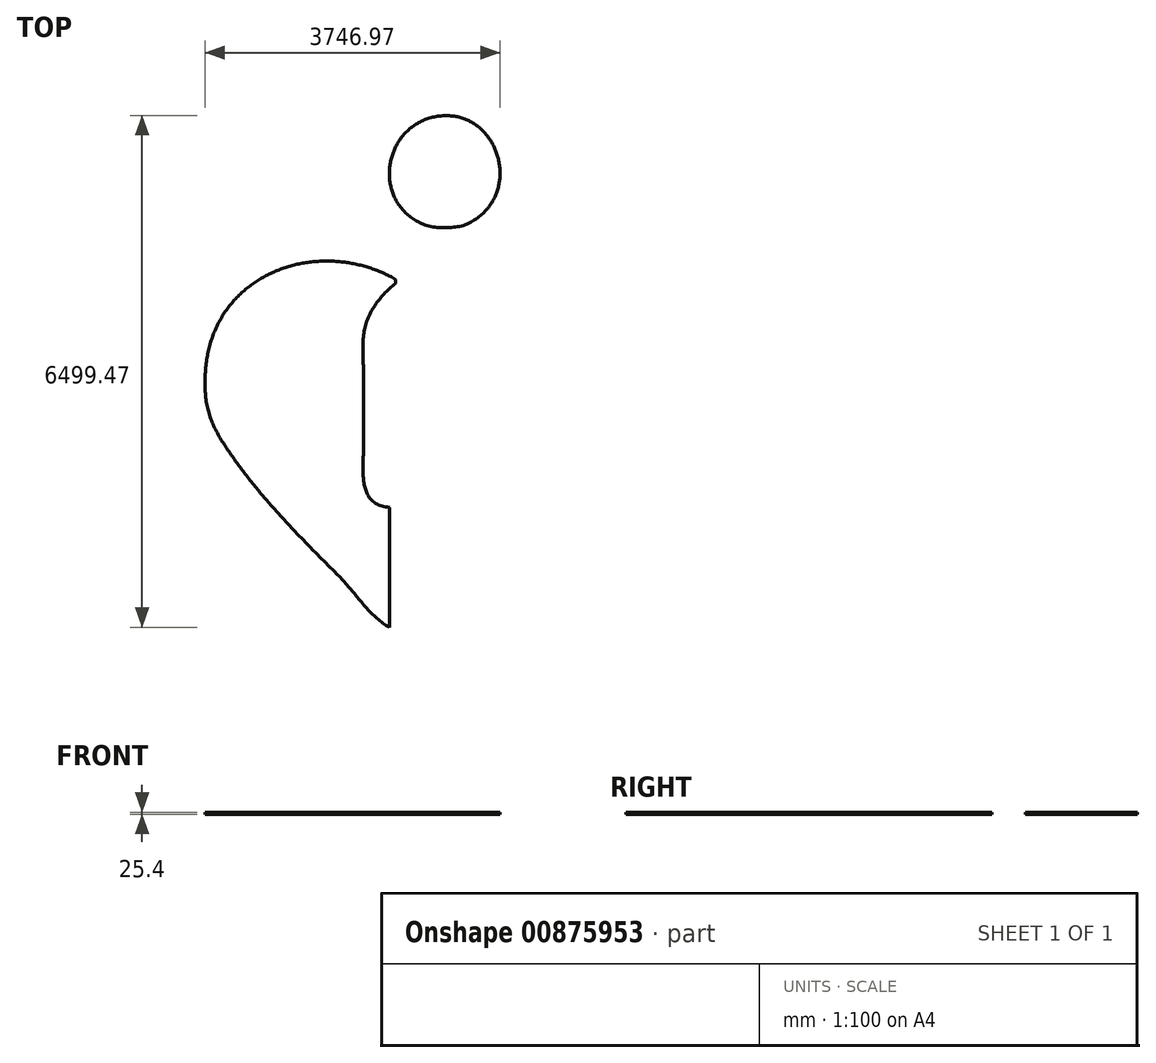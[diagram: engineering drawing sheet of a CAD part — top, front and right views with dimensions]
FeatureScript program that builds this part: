
annotation { "Feature Type Name" : "Feature", "Feature Type Description" : "" }
export const myFeature = defineFeature(function(context is Context, id is Id, definition is map)
    precondition{}
    {
        {
            var Q0;
            Q0=qCreatedBy(makeId("Top.planeOp"),FACE);
            var sketch = newSketch(context, id + "F0", { "sketchPlane" : qUnion([Q0])});
            skLineSegment(sketch, "E0", {"start": v(-84.52, 3774.14) * mm, "end": v(-106.58, 3770.53) * mm});
            skLineSegment(sketch, "E1", {"start": v(-106.58, 3770.53) * mm, "end": v(-128.27, 3766.32) * mm});
            skLineSegment(sketch, "E2", {"start": v(-128.27, 3766.32) * mm, "end": v(-149.6, 3761.53) * mm});
            skLineSegment(sketch, "E3", {"start": v(-149.6, 3761.53) * mm, "end": v(-170.55, 3756.17) * mm});
            skLineSegment(sketch, "E4", {"start": v(-170.55, 3756.17) * mm, "end": v(-191.14, 3750.25) * mm});
            skLineSegment(sketch, "E5", {"start": v(-191.14, 3750.25) * mm, "end": v(-211.36, 3743.78) * mm});
            skLineSegment(sketch, "E6", {"start": v(-211.36, 3743.78) * mm, "end": v(-231.2, 3736.77) * mm});
            skLineSegment(sketch, "E7", {"start": v(-231.2, 3736.77) * mm, "end": v(-250.65, 3729.24) * mm});
            skLineSegment(sketch, "E8", {"start": v(-250.65, 3729.24) * mm, "end": v(-269.73, 3721.19) * mm});
            skLineSegment(sketch, "E9", {"start": v(-269.73, 3721.19) * mm, "end": v(-288.43, 3712.64) * mm});
            skLineSegment(sketch, "E10", {"start": v(-288.43, 3712.64) * mm, "end": v(-306.74, 3703.6) * mm});
            skLineSegment(sketch, "E11", {"start": v(-306.74, 3703.6) * mm, "end": v(-324.67, 3694.08) * mm});
            skLineSegment(sketch, "E12", {"start": v(-324.67, 3694.08) * mm, "end": v(-342.2, 3684.1) * mm});
            skLineSegment(sketch, "E13", {"start": v(-342.2, 3684.1) * mm, "end": v(-359.34, 3673.65) * mm});
            skLineSegment(sketch, "E14", {"start": v(-359.34, 3673.65) * mm, "end": v(-376.09, 3662.76) * mm});
            skLineSegment(sketch, "E15", {"start": v(-376.09, 3662.76) * mm, "end": v(-392.44, 3651.45) * mm});
            skLineSegment(sketch, "E16", {"start": v(-392.44, 3651.45) * mm, "end": v(-408.39, 3639.7) * mm});
            skLineSegment(sketch, "E17", {"start": v(-408.39, 3639.7) * mm, "end": v(-423.94, 3627.56) * mm});
            skLineSegment(sketch, "E18", {"start": v(-423.94, 3627.56) * mm, "end": v(-439.08, 3615.01) * mm});
            skLineSegment(sketch, "E19", {"start": v(-439.08, 3615.01) * mm, "end": v(-453.82, 3602.09) * mm});
            skLineSegment(sketch, "E20", {"start": v(-453.82, 3602.09) * mm, "end": v(-468.14, 3588.78) * mm});
            skLineSegment(sketch, "E21", {"start": v(-468.14, 3588.78) * mm, "end": v(-482.06, 3575.11) * mm});
            skLineSegment(sketch, "E22", {"start": v(-482.06, 3575.11) * mm, "end": v(-495.57, 3561.1) * mm});
            skLineSegment(sketch, "E23", {"start": v(-495.57, 3561.1) * mm, "end": v(-508.65, 3546.74) * mm});
            skLineSegment(sketch, "E24", {"start": v(-508.65, 3546.74) * mm, "end": v(-521.32, 3532.06) * mm});
            skLineSegment(sketch, "E25", {"start": v(-521.32, 3532.06) * mm, "end": v(-533.57, 3517.06) * mm});
            skLineSegment(sketch, "E26", {"start": v(-533.57, 3517.06) * mm, "end": v(-545.4, 3501.75) * mm});
            skLineSegment(sketch, "E27", {"start": v(-545.4, 3501.75) * mm, "end": v(-556.8, 3486.16) * mm});
            skLineSegment(sketch, "E28", {"start": v(-556.8, 3486.16) * mm, "end": v(-567.76, 3470.28) * mm});
            skLineSegment(sketch, "E29", {"start": v(-567.76, 3470.28) * mm, "end": v(-578.3, 3454.14) * mm});
            skLineSegment(sketch, "E30", {"start": v(-578.3, 3454.14) * mm, "end": v(-588.41, 3437.73) * mm});
            skLineSegment(sketch, "E31", {"start": v(-588.41, 3437.73) * mm, "end": v(-598.09, 3421.08) * mm});
            skLineSegment(sketch, "E32", {"start": v(-598.09, 3421.08) * mm, "end": v(-607.32, 3404.2) * mm});
            skLineSegment(sketch, "E33", {"start": v(-607.32, 3404.2) * mm, "end": v(-616.12, 3387.1) * mm});
            skLineSegment(sketch, "E34", {"start": v(-616.12, 3387.1) * mm, "end": v(-624.47, 3369.78) * mm});
            skLineSegment(sketch, "E35", {"start": v(-624.47, 3369.78) * mm, "end": v(-632.38, 3352.26) * mm});
            skLineSegment(sketch, "E36", {"start": v(-632.38, 3352.26) * mm, "end": v(-639.84, 3334.56) * mm});
            skLineSegment(sketch, "E37", {"start": v(-639.84, 3334.56) * mm, "end": v(-646.85, 3316.68) * mm});
            skLineSegment(sketch, "E38", {"start": v(-646.85, 3316.68) * mm, "end": v(-653.41, 3298.64) * mm});
            skLineSegment(sketch, "E39", {"start": v(-653.41, 3298.64) * mm, "end": v(-659.52, 3280.45) * mm});
            skLineSegment(sketch, "E40", {"start": v(-659.52, 3280.45) * mm, "end": v(-665.17, 3262.1) * mm});
            skLineSegment(sketch, "E41", {"start": v(-665.17, 3262.1) * mm, "end": v(-670.36, 3243.65) * mm});
            skLineSegment(sketch, "E42", {"start": v(-670.36, 3243.65) * mm, "end": v(-675.09, 3225.06) * mm});
            skLineSegment(sketch, "E43", {"start": v(-675.09, 3225.06) * mm, "end": v(-679.36, 3206.37) * mm});
            skLineSegment(sketch, "E44", {"start": v(-679.36, 3206.37) * mm, "end": v(-683.16, 3187.6) * mm});
            skLineSegment(sketch, "E45", {"start": v(-683.16, 3187.6) * mm, "end": v(-686.49, 3168.73) * mm});
            skLineSegment(sketch, "E46", {"start": v(-686.49, 3168.73) * mm, "end": v(-689.35, 3149.8) * mm});
            skLineSegment(sketch, "E47", {"start": v(-689.35, 3149.8) * mm, "end": v(-691.74, 3130.8) * mm});
            skLineSegment(sketch, "E48", {"start": v(-691.74, 3130.8) * mm, "end": v(-693.65, 3111.75) * mm});
            skLineSegment(sketch, "E49", {"start": v(-693.65, 3111.75) * mm, "end": v(-695.08, 3092.68) * mm});
            skLineSegment(sketch, "E50", {"start": v(-695.08, 3092.68) * mm, "end": v(-696.04, 3073.57) * mm});
            skLineSegment(sketch, "E51", {"start": v(-696.04, 3073.57) * mm, "end": v(-696.5, 3054.46) * mm});
            skLineSegment(sketch, "E52", {"start": v(-696.5, 3054.46) * mm, "end": v(-696.5, 3035.34) * mm});
            skLineSegment(sketch, "E53", {"start": v(-696.5, 3035.34) * mm, "end": v(-696, 3016.23) * mm});
            skLineSegment(sketch, "E54", {"start": v(-696, 3016.23) * mm, "end": v(-695, 2997.15) * mm});
            skLineSegment(sketch, "E55", {"start": v(-695, 2997.15) * mm, "end": v(-693.52, 2978.1) * mm});
            skLineSegment(sketch, "E56", {"start": v(-693.52, 2978.1) * mm, "end": v(-691.54, 2959.1) * mm});
            skLineSegment(sketch, "E57", {"start": v(-691.54, 2959.1) * mm, "end": v(-689.07, 2940.15) * mm});
            skLineSegment(sketch, "E58", {"start": v(-689.07, 2940.15) * mm, "end": v(-686.1, 2921.28) * mm});
            skLineSegment(sketch, "E59", {"start": v(-686.1, 2921.28) * mm, "end": v(-682.62, 2902.48) * mm});
            skLineSegment(sketch, "E60", {"start": v(-682.62, 2902.48) * mm, "end": v(-678.64, 2883.78) * mm});
            skLineSegment(sketch, "E61", {"start": v(-678.64, 2883.78) * mm, "end": v(-674.15, 2865.18) * mm});
            skLineSegment(sketch, "E62", {"start": v(-674.15, 2865.18) * mm, "end": v(-669.16, 2846.7) * mm});
            skLineSegment(sketch, "E63", {"start": v(-669.16, 2846.7) * mm, "end": v(-663.65, 2828.34) * mm});
            skLineSegment(sketch, "E64", {"start": v(-663.65, 2828.34) * mm, "end": v(-657.63, 2810.12) * mm});
            skLineSegment(sketch, "E65", {"start": v(-657.63, 2810.12) * mm, "end": v(-651.1, 2792.05) * mm});
            skLineSegment(sketch, "E66", {"start": v(-651.1, 2792.05) * mm, "end": v(-644.04, 2774.14) * mm});
            skLineSegment(sketch, "E67", {"start": v(-644.04, 2774.14) * mm, "end": v(-636.47, 2756.41) * mm});
            skLineSegment(sketch, "E68", {"start": v(-636.47, 2756.41) * mm, "end": v(-628.38, 2738.87) * mm});
            skLineSegment(sketch, "E69", {"start": v(-628.38, 2738.87) * mm, "end": v(-619.75, 2721.52) * mm});
            skLineSegment(sketch, "E70", {"start": v(-619.75, 2721.52) * mm, "end": v(-610.6, 2704.38) * mm});
            skLineSegment(sketch, "E71", {"start": v(-610.6, 2704.38) * mm, "end": v(-600.92, 2687.46) * mm});
            skLineSegment(sketch, "E72", {"start": v(-600.92, 2687.46) * mm, "end": v(-590.7, 2670.77) * mm});
            skLineSegment(sketch, "E73", {"start": v(-590.7, 2670.77) * mm, "end": v(-579.96, 2654.33) * mm});
            skLineSegment(sketch, "E74", {"start": v(-579.96, 2654.33) * mm, "end": v(-568.68, 2638.14) * mm});
            skLineSegment(sketch, "E75", {"start": v(-568.68, 2638.14) * mm, "end": v(-556.85, 2622.22) * mm});
            skLineSegment(sketch, "E76", {"start": v(-556.85, 2622.22) * mm, "end": v(-544.48, 2606.58) * mm});
            skLineSegment(sketch, "E77", {"start": v(-544.48, 2606.58) * mm, "end": v(-531.57, 2591.23) * mm});
            skLineSegment(sketch, "E78", {"start": v(-531.57, 2591.23) * mm, "end": v(-518.11, 2576.18) * mm});
            skLineSegment(sketch, "E79", {"start": v(-518.11, 2576.18) * mm, "end": v(-504.1, 2561.45) * mm});
            skLineSegment(sketch, "E80", {"start": v(-504.1, 2561.45) * mm, "end": v(-489.55, 2547.04) * mm});
            skLineSegment(sketch, "E81", {"start": v(-489.55, 2547.04) * mm, "end": v(-474.44, 2532.97) * mm});
            skLineSegment(sketch, "E82", {"start": v(-474.44, 2532.97) * mm, "end": v(-458.77, 2519.24) * mm});
            skLineSegment(sketch, "E83", {"start": v(-458.77, 2519.24) * mm, "end": v(-442.54, 2505.88) * mm});
            skLineSegment(sketch, "E84", {"start": v(-442.54, 2505.88) * mm, "end": v(-425.75, 2492.89) * mm});
            skLineSegment(sketch, "E85", {"start": v(-425.75, 2492.89) * mm, "end": v(-408.4, 2480.28) * mm});
            skLineSegment(sketch, "E86", {"start": v(-408.4, 2480.28) * mm, "end": v(-390.48, 2468.07) * mm});
            skLineSegment(sketch, "E87", {"start": v(-390.48, 2468.07) * mm, "end": v(-372, 2456.26) * mm});
            skLineSegment(sketch, "E88", {"start": v(-372, 2456.26) * mm, "end": v(-352.94, 2444.88) * mm});
            skLineSegment(sketch, "E89", {"start": v(-352.94, 2444.88) * mm, "end": v(-333.3, 2433.92) * mm});
            skLineSegment(sketch, "E90", {"start": v(-333.3, 2433.92) * mm, "end": v(-313.1, 2423.41) * mm});
            skLineSegment(sketch, "E91", {"start": v(-313.1, 2423.41) * mm, "end": v(-290.23, 2412.64) * mm});
            skLineSegment(sketch, "E92", {"start": v(-290.23, 2412.64) * mm, "end": v(-266.73, 2402.93) * mm});
            skLineSegment(sketch, "E93", {"start": v(-266.73, 2402.93) * mm, "end": v(-242.68, 2394.27) * mm});
            skLineSegment(sketch, "E94", {"start": v(-242.68, 2394.27) * mm, "end": v(-218.13, 2386.6) * mm});
            skLineSegment(sketch, "E95", {"start": v(-218.13, 2386.6) * mm, "end": v(-193.14, 2379.92) * mm});
            skLineSegment(sketch, "E96", {"start": v(-193.14, 2379.92) * mm, "end": v(-167.76, 2374.18) * mm});
            skLineSegment(sketch, "E97", {"start": v(-167.76, 2374.18) * mm, "end": v(-142.07, 2369.34) * mm});
            skLineSegment(sketch, "E98", {"start": v(-142.07, 2369.34) * mm, "end": v(-116.12, 2365.39) * mm});
            skLineSegment(sketch, "E99", {"start": v(-116.12, 2365.39) * mm, "end": v(-89.97, 2362.28) * mm});
            skLineSegment(sketch, "E100", {"start": v(-89.97, 2362.28) * mm, "end": v(-63.68, 2359.98) * mm});
            skLineSegment(sketch, "E101", {"start": v(-63.68, 2359.98) * mm, "end": v(-37.3, 2358.47) * mm});
            skLineSegment(sketch, "E102", {"start": v(-37.3, 2358.47) * mm, "end": v(-10.9, 2357.7) * mm});
            skLineSegment(sketch, "E103", {"start": v(-10.9, 2357.7) * mm, "end": v(15.46, 2357.67) * mm});
            skLineSegment(sketch, "E104", {"start": v(15.46, 2357.67) * mm, "end": v(41.72, 2358.31) * mm});
            skLineSegment(sketch, "E105", {"start": v(41.72, 2358.31) * mm, "end": v(67.83, 2359.61) * mm});
            skLineSegment(sketch, "E106", {"start": v(67.83, 2359.61) * mm, "end": v(93.71, 2361.54) * mm});
            skLineSegment(sketch, "E107", {"start": v(93.71, 2361.54) * mm, "end": v(119.33, 2364.05) * mm});
            skLineSegment(sketch, "E108", {"start": v(119.33, 2364.05) * mm, "end": v(144.6, 2367.13) * mm});
            skLineSegment(sketch, "E109", {"start": v(144.6, 2367.13) * mm, "end": v(169.48, 2370.73) * mm});
            skLineSegment(sketch, "E110", {"start": v(169.48, 2370.73) * mm, "end": v(194.99, 2375.43) * mm});
            skLineSegment(sketch, "E111", {"start": v(194.99, 2375.43) * mm, "end": v(219.93, 2381.44) * mm});
            skLineSegment(sketch, "E112", {"start": v(219.93, 2381.44) * mm, "end": v(244.35, 2388.67) * mm});
            skLineSegment(sketch, "E113", {"start": v(244.35, 2388.67) * mm, "end": v(268.25, 2397.1) * mm});
            skLineSegment(sketch, "E114", {"start": v(268.25, 2397.1) * mm, "end": v(291.68, 2406.63) * mm});
            skLineSegment(sketch, "E115", {"start": v(291.68, 2406.63) * mm, "end": v(314.64, 2417.23) * mm});
            skLineSegment(sketch, "E116", {"start": v(314.64, 2417.23) * mm, "end": v(337.17, 2428.83) * mm});
            skLineSegment(sketch, "E117", {"start": v(337.17, 2428.83) * mm, "end": v(359.3, 2441.37) * mm});
            skLineSegment(sketch, "E118", {"start": v(359.3, 2441.37) * mm, "end": v(381.03, 2454.79) * mm});
            skLineSegment(sketch, "E119", {"start": v(381.03, 2454.79) * mm, "end": v(402.41, 2469.03) * mm});
            skLineSegment(sketch, "E120", {"start": v(402.41, 2469.03) * mm, "end": v(423.46, 2484.03) * mm});
            skLineSegment(sketch, "E121", {"start": v(423.46, 2484.03) * mm, "end": v(440.87, 2497.23) * mm});
            skLineSegment(sketch, "E122", {"start": v(440.87, 2497.23) * mm, "end": v(457.7, 2510.77) * mm});
            skLineSegment(sketch, "E123", {"start": v(457.7, 2510.77) * mm, "end": v(473.94, 2524.64) * mm});
            skLineSegment(sketch, "E124", {"start": v(473.94, 2524.64) * mm, "end": v(489.6, 2538.84) * mm});
            skLineSegment(sketch, "E125", {"start": v(489.6, 2538.84) * mm, "end": v(504.7, 2553.35) * mm});
            skLineSegment(sketch, "E126", {"start": v(504.7, 2553.35) * mm, "end": v(519.21, 2568.16) * mm});
            skLineSegment(sketch, "E127", {"start": v(519.21, 2568.16) * mm, "end": v(533.16, 2583.25) * mm});
            skLineSegment(sketch, "E128", {"start": v(533.16, 2583.25) * mm, "end": v(546.55, 2598.63) * mm});
            skLineSegment(sketch, "E129", {"start": v(546.55, 2598.63) * mm, "end": v(559.38, 2614.28) * mm});
            skLineSegment(sketch, "E130", {"start": v(559.38, 2614.28) * mm, "end": v(571.64, 2630.19) * mm});
            skLineSegment(sketch, "E131", {"start": v(571.64, 2630.19) * mm, "end": v(583.36, 2646.34) * mm});
            skLineSegment(sketch, "E132", {"start": v(583.36, 2646.34) * mm, "end": v(594.53, 2662.73) * mm});
            skLineSegment(sketch, "E133", {"start": v(594.53, 2662.73) * mm, "end": v(605.15, 2679.34) * mm});
            skLineSegment(sketch, "E134", {"start": v(605.15, 2679.34) * mm, "end": v(615.23, 2696.16) * mm});
            skLineSegment(sketch, "E135", {"start": v(615.23, 2696.16) * mm, "end": v(624.77, 2713.2) * mm});
            skLineSegment(sketch, "E136", {"start": v(624.77, 2713.2) * mm, "end": v(633.77, 2730.42) * mm});
            skLineSegment(sketch, "E137", {"start": v(633.77, 2730.42) * mm, "end": v(642.24, 2747.83) * mm});
            skLineSegment(sketch, "E138", {"start": v(642.24, 2747.83) * mm, "end": v(650.19, 2765.4) * mm});
            skLineSegment(sketch, "E139", {"start": v(650.19, 2765.4) * mm, "end": v(657.6, 2783.14) * mm});
            skLineSegment(sketch, "E140", {"start": v(657.6, 2783.14) * mm, "end": v(664.5, 2801.03) * mm});
            skLineSegment(sketch, "E141", {"start": v(664.5, 2801.03) * mm, "end": v(670.89, 2819.06) * mm});
            skLineSegment(sketch, "E142", {"start": v(670.89, 2819.06) * mm, "end": v(676.76, 2837.21) * mm});
            skLineSegment(sketch, "E143", {"start": v(676.76, 2837.21) * mm, "end": v(682.11, 2855.49) * mm});
            skLineSegment(sketch, "E144", {"start": v(682.11, 2855.49) * mm, "end": v(686.97, 2873.87) * mm});
            skLineSegment(sketch, "E145", {"start": v(686.97, 2873.87) * mm, "end": v(691.31, 2892.34) * mm});
            skLineSegment(sketch, "E146", {"start": v(691.31, 2892.34) * mm, "end": v(695.16, 2910.9) * mm});
            skLineSegment(sketch, "E147", {"start": v(695.16, 2910.9) * mm, "end": v(698.52, 2929.53) * mm});
            skLineSegment(sketch, "E148", {"start": v(698.52, 2929.53) * mm, "end": v(701.38, 2948.23) * mm});
            skLineSegment(sketch, "E149", {"start": v(701.38, 2948.23) * mm, "end": v(703.75, 2966.98) * mm});
            skLineSegment(sketch, "E150", {"start": v(703.75, 2966.98) * mm, "end": v(705.63, 2985.77) * mm});
            skLineSegment(sketch, "E151", {"start": v(705.63, 2985.77) * mm, "end": v(707.04, 3004.6) * mm});
            skLineSegment(sketch, "E152", {"start": v(707.04, 3004.6) * mm, "end": v(707.97, 3023.44) * mm});
            skLineSegment(sketch, "E153", {"start": v(707.97, 3023.44) * mm, "end": v(708.42, 3042.3) * mm});
            skLineSegment(sketch, "E154", {"start": v(708.42, 3042.3) * mm, "end": v(708.4, 3061.14) * mm});
            skLineSegment(sketch, "E155", {"start": v(708.4, 3061.14) * mm, "end": v(707.92, 3079.98) * mm});
            skLineSegment(sketch, "E156", {"start": v(707.92, 3079.98) * mm, "end": v(706.98, 3098.8) * mm});
            skLineSegment(sketch, "E157", {"start": v(706.98, 3098.8) * mm, "end": v(705.57, 3117.58) * mm});
            skLineSegment(sketch, "E158", {"start": v(705.57, 3117.58) * mm, "end": v(703.7, 3136.31) * mm});
            skLineSegment(sketch, "E159", {"start": v(703.7, 3136.31) * mm, "end": v(701.4, 3155) * mm});
            skLineSegment(sketch, "E160", {"start": v(701.4, 3155) * mm, "end": v(698.62, 3173.6) * mm});
            skLineSegment(sketch, "E161", {"start": v(698.62, 3173.6) * mm, "end": v(695.41, 3192.15) * mm});
            skLineSegment(sketch, "E162", {"start": v(695.41, 3192.15) * mm, "end": v(691.76, 3210.6) * mm});
            skLineSegment(sketch, "E163", {"start": v(691.76, 3210.6) * mm, "end": v(687.67, 3228.95) * mm});
            skLineSegment(sketch, "E164", {"start": v(687.67, 3228.95) * mm, "end": v(683.15, 3247.2) * mm});
            skLineSegment(sketch, "E165", {"start": v(683.15, 3247.2) * mm, "end": v(678.2, 3265.31) * mm});
            skLineSegment(sketch, "E166", {"start": v(678.2, 3265.31) * mm, "end": v(672.8, 3283.3) * mm});
            skLineSegment(sketch, "E167", {"start": v(672.8, 3283.3) * mm, "end": v(667, 3301.15) * mm});
            skLineSegment(sketch, "E168", {"start": v(667, 3301.15) * mm, "end": v(660.77, 3318.85) * mm});
            skLineSegment(sketch, "E169", {"start": v(660.77, 3318.85) * mm, "end": v(654.12, 3336.38) * mm});
            skLineSegment(sketch, "E170", {"start": v(654.12, 3336.38) * mm, "end": v(647.07, 3353.74) * mm});
            skLineSegment(sketch, "E171", {"start": v(647.07, 3353.74) * mm, "end": v(639.6, 3370.92) * mm});
            skLineSegment(sketch, "E172", {"start": v(639.6, 3370.92) * mm, "end": v(631.73, 3387.9) * mm});
            skLineSegment(sketch, "E173", {"start": v(631.73, 3387.9) * mm, "end": v(623.45, 3404.66) * mm});
            skLineSegment(sketch, "E174", {"start": v(623.45, 3404.66) * mm, "end": v(614.77, 3421.22) * mm});
            skLineSegment(sketch, "E175", {"start": v(614.77, 3421.22) * mm, "end": v(605.7, 3437.54) * mm});
            skLineSegment(sketch, "E176", {"start": v(605.7, 3437.54) * mm, "end": v(596.24, 3453.63) * mm});
            skLineSegment(sketch, "E177", {"start": v(596.24, 3453.63) * mm, "end": v(586.4, 3469.47) * mm});
            skLineSegment(sketch, "E178", {"start": v(586.4, 3469.47) * mm, "end": v(576.16, 3485.05) * mm});
            skLineSegment(sketch, "E179", {"start": v(576.16, 3485.05) * mm, "end": v(565.54, 3500.35) * mm});
            skLineSegment(sketch, "E180", {"start": v(565.54, 3500.35) * mm, "end": v(554.55, 3515.37) * mm});
            skLineSegment(sketch, "E181", {"start": v(554.55, 3515.37) * mm, "end": v(543.19, 3530.1) * mm});
            skLineSegment(sketch, "E182", {"start": v(543.19, 3530.1) * mm, "end": v(531.45, 3544.53) * mm});
            skLineSegment(sketch, "E183", {"start": v(531.45, 3544.53) * mm, "end": v(519.35, 3558.64) * mm});
            skLineSegment(sketch, "E184", {"start": v(519.35, 3558.64) * mm, "end": v(506.88, 3572.43) * mm});
            skLineSegment(sketch, "E185", {"start": v(506.88, 3572.43) * mm, "end": v(494.06, 3585.88) * mm});
            skLineSegment(sketch, "E186", {"start": v(494.06, 3585.88) * mm, "end": v(480.88, 3598.98) * mm});
            skLineSegment(sketch, "E187", {"start": v(480.88, 3598.98) * mm, "end": v(467.35, 3611.72) * mm});
            skLineSegment(sketch, "E188", {"start": v(467.35, 3611.72) * mm, "end": v(453.47, 3624.1) * mm});
            skLineSegment(sketch, "E189", {"start": v(453.47, 3624.1) * mm, "end": v(439.24, 3636.1) * mm});
            skLineSegment(sketch, "E190", {"start": v(439.24, 3636.1) * mm, "end": v(424.67, 3647.7) * mm});
            skLineSegment(sketch, "E191", {"start": v(424.67, 3647.7) * mm, "end": v(409.77, 3658.9) * mm});
            skLineSegment(sketch, "E192", {"start": v(409.77, 3658.9) * mm, "end": v(394.53, 3669.7) * mm});
            skLineSegment(sketch, "E193", {"start": v(394.53, 3669.7) * mm, "end": v(378.96, 3680.07) * mm});
            skLineSegment(sketch, "E194", {"start": v(378.96, 3680.07) * mm, "end": v(363.07, 3690.01) * mm});
            skLineSegment(sketch, "E195", {"start": v(363.07, 3690.01) * mm, "end": v(346.84, 3699.5) * mm});
            skLineSegment(sketch, "E196", {"start": v(346.84, 3699.5) * mm, "end": v(330.3, 3708.54) * mm});
            skLineSegment(sketch, "E197", {"start": v(330.3, 3708.54) * mm, "end": v(313.45, 3717.12) * mm});
            skLineSegment(sketch, "E198", {"start": v(313.45, 3717.12) * mm, "end": v(296.28, 3725.21) * mm});
            skLineSegment(sketch, "E199", {"start": v(296.28, 3725.21) * mm, "end": v(278.8, 3732.82) * mm});
            skLineSegment(sketch, "E200", {"start": v(278.8, 3732.82) * mm, "end": v(261.02, 3739.94) * mm});
            skLineSegment(sketch, "E201", {"start": v(261.02, 3739.94) * mm, "end": v(242.94, 3746.54) * mm});
            skLineSegment(sketch, "E202", {"start": v(242.94, 3746.54) * mm, "end": v(224.56, 3752.62) * mm});
            skLineSegment(sketch, "E203", {"start": v(224.56, 3752.62) * mm, "end": v(205.88, 3758.17) * mm});
            skLineSegment(sketch, "E204", {"start": v(205.88, 3758.17) * mm, "end": v(186.91, 3763.18) * mm});
            skLineSegment(sketch, "E205", {"start": v(186.91, 3763.18) * mm, "end": v(167.66, 3767.64) * mm});
            skLineSegment(sketch, "E206", {"start": v(167.66, 3767.64) * mm, "end": v(148.12, 3771.53) * mm});
            skLineSegment(sketch, "E207", {"start": v(148.12, 3771.53) * mm, "end": v(128.3, 3774.86) * mm});
            skLineSegment(sketch, "E208", {"start": v(128.3, 3774.86) * mm, "end": v(108.2, 3777.6) * mm});
            skLineSegment(sketch, "E209", {"start": v(108.2, 3777.6) * mm, "end": v(87.83, 3779.74) * mm});
            skLineSegment(sketch, "E210", {"start": v(87.83, 3779.74) * mm, "end": v(67.2, 3781.27) * mm});
            skLineSegment(sketch, "E211", {"start": v(67.2, 3781.27) * mm, "end": v(46.29, 3782.19) * mm});
            skLineSegment(sketch, "E212", {"start": v(46.29, 3782.19) * mm, "end": v(25.12, 3782.48) * mm});
            skLineSegment(sketch, "E213", {"start": v(25.12, 3782.48) * mm, "end": v(3.7, 3782.13) * mm});
            skLineSegment(sketch, "E214", {"start": v(3.7, 3782.13) * mm, "end": v(-17.98, 3781.14) * mm});
            skLineSegment(sketch, "E215", {"start": v(-17.98, 3781.14) * mm, "end": v(-39.92, 3779.48) * mm});
            skLineSegment(sketch, "E216", {"start": v(-39.92, 3779.48) * mm, "end": v(-62.1, 3777.15) * mm});
            skLineSegment(sketch, "E217", {"start": v(-62.1, 3777.15) * mm, "end": v(-84.52, 3774.14) * mm});
            skLineSegment(sketch, "E218", {"start": v(-33.72, 1931.21) * mm, "end": v(-45.6, 1950.9) * mm});
            skLineSegment(sketch, "E219", {"start": v(-45.6, 1950.9) * mm, "end": v(-58.4, 1970.2) * mm});
            skLineSegment(sketch, "E220", {"start": v(-58.4, 1970.2) * mm, "end": v(-72.05, 1989.14) * mm});
            skLineSegment(sketch, "E221", {"start": v(-72.05, 1989.14) * mm, "end": v(-86.55, 2007.7) * mm});
            skLineSegment(sketch, "E222", {"start": v(-86.55, 2007.7) * mm, "end": v(-101.84, 2025.9) * mm});
            skLineSegment(sketch, "E223", {"start": v(-101.84, 2025.9) * mm, "end": v(-117.9, 2043.72) * mm});
            skLineSegment(sketch, "E224", {"start": v(-117.9, 2043.72) * mm, "end": v(-134.7, 2061.18) * mm});
            skLineSegment(sketch, "E225", {"start": v(-134.7, 2061.18) * mm, "end": v(-152.2, 2078.27) * mm});
            skLineSegment(sketch, "E226", {"start": v(-152.2, 2078.27) * mm, "end": v(-170.36, 2095) * mm});
            skLineSegment(sketch, "E227", {"start": v(-170.36, 2095) * mm, "end": v(-189.15, 2111.37) * mm});
            skLineSegment(sketch, "E228", {"start": v(-189.15, 2111.37) * mm, "end": v(-208.53, 2127.37) * mm});
            skLineSegment(sketch, "E229", {"start": v(-208.53, 2127.37) * mm, "end": v(-228.48, 2143.03) * mm});
            skLineSegment(sketch, "E230", {"start": v(-228.48, 2143.03) * mm, "end": v(-248.96, 2158.32) * mm});
            skLineSegment(sketch, "E231", {"start": v(-248.96, 2158.32) * mm, "end": v(-269.93, 2173.26) * mm});
            skLineSegment(sketch, "E232", {"start": v(-269.93, 2173.26) * mm, "end": v(-291.35, 2187.85) * mm});
            skLineSegment(sketch, "E233", {"start": v(-291.35, 2187.85) * mm, "end": v(-313.2, 2202.09) * mm});
            skLineSegment(sketch, "E234", {"start": v(-313.2, 2202.09) * mm, "end": v(-335.45, 2215.98) * mm});
            skLineSegment(sketch, "E235", {"start": v(-335.45, 2215.98) * mm, "end": v(-358.05, 2229.53) * mm});
            skLineSegment(sketch, "E236", {"start": v(-358.05, 2229.53) * mm, "end": v(-380.97, 2242.73) * mm});
            skLineSegment(sketch, "E237", {"start": v(-380.97, 2242.73) * mm, "end": v(-404.17, 2255.58) * mm});
            skLineSegment(sketch, "E238", {"start": v(-404.17, 2255.58) * mm, "end": v(-427.64, 2268.1) * mm});
            skLineSegment(sketch, "E239", {"start": v(-427.64, 2268.1) * mm, "end": v(-451.32, 2280.28) * mm});
            skLineSegment(sketch, "E240", {"start": v(-451.32, 2280.28) * mm, "end": v(-475.18, 2292.12) * mm});
            skLineSegment(sketch, "E241", {"start": v(-475.18, 2292.12) * mm, "end": v(-499.2, 2303.63) * mm});
            skLineSegment(sketch, "E242", {"start": v(-499.2, 2303.63) * mm, "end": v(-523.33, 2314.8) * mm});
            skLineSegment(sketch, "E243", {"start": v(-523.33, 2314.8) * mm, "end": v(-547.55, 2325.65) * mm});
            skLineSegment(sketch, "E244", {"start": v(-547.55, 2325.65) * mm, "end": v(-571.8, 2336.17) * mm});
            skLineSegment(sketch, "E245", {"start": v(-571.8, 2336.17) * mm, "end": v(-596.08, 2346.35) * mm});
            skLineSegment(sketch, "E246", {"start": v(-596.08, 2346.35) * mm, "end": v(-620.34, 2356.22) * mm});
            skLineSegment(sketch, "E247", {"start": v(-620.34, 2356.22) * mm, "end": v(-644.54, 2365.76) * mm});
            skLineSegment(sketch, "E248", {"start": v(-644.54, 2365.76) * mm, "end": v(-668.65, 2374.97) * mm});
            skLineSegment(sketch, "E249", {"start": v(-668.65, 2374.97) * mm, "end": v(-692.64, 2383.87) * mm});
            skLineSegment(sketch, "E250", {"start": v(-692.64, 2383.87) * mm, "end": v(-716.47, 2392.45) * mm});
            skLineSegment(sketch, "E251", {"start": v(-716.47, 2392.45) * mm, "end": v(-740.1, 2400.72) * mm});
            skLineSegment(sketch, "E252", {"start": v(-740.1, 2400.72) * mm, "end": v(-763.52, 2408.67) * mm});
            skLineSegment(sketch, "E253", {"start": v(-763.52, 2408.67) * mm, "end": v(-786.67, 2416.3) * mm});
            skLineSegment(sketch, "E254", {"start": v(-786.67, 2416.3) * mm, "end": v(-809.53, 2423.64) * mm});
            skLineSegment(sketch, "E255", {"start": v(-809.53, 2423.64) * mm, "end": v(-832.05, 2430.66) * mm});
            skLineSegment(sketch, "E256", {"start": v(-832.05, 2430.66) * mm, "end": v(-854.22, 2437.37) * mm});
            skLineSegment(sketch, "E257", {"start": v(-854.22, 2437.37) * mm, "end": v(-875.99, 2443.78) * mm});
            skLineSegment(sketch, "E258", {"start": v(-875.99, 2443.78) * mm, "end": v(-897.32, 2449.9) * mm});
            skLineSegment(sketch, "E259", {"start": v(-897.32, 2449.9) * mm, "end": v(-920.18, 2456.2) * mm});
            skLineSegment(sketch, "E260", {"start": v(-920.18, 2456.2) * mm, "end": v(-943.07, 2462.22) * mm});
            skLineSegment(sketch, "E261", {"start": v(-943.07, 2462.22) * mm, "end": v(-965.98, 2467.97) * mm});
            skLineSegment(sketch, "E262", {"start": v(-965.98, 2467.97) * mm, "end": v(-988.93, 2473.43) * mm});
            skLineSegment(sketch, "E263", {"start": v(-988.93, 2473.43) * mm, "end": v(-1011.9, 2478.63) * mm});
            skLineSegment(sketch, "E264", {"start": v(-1011.9, 2478.63) * mm, "end": v(-1034.88, 2483.54) * mm});
            skLineSegment(sketch, "E265", {"start": v(-1034.88, 2483.54) * mm, "end": v(-1057.9, 2488.18) * mm});
            skLineSegment(sketch, "E266", {"start": v(-1057.9, 2488.18) * mm, "end": v(-1080.92, 2492.55) * mm});
            skLineSegment(sketch, "E267", {"start": v(-1080.92, 2492.55) * mm, "end": v(-1103.97, 2496.64) * mm});
            skLineSegment(sketch, "E268", {"start": v(-1103.97, 2496.64) * mm, "end": v(-1127.03, 2500.46) * mm});
            skLineSegment(sketch, "E269", {"start": v(-1127.03, 2500.46) * mm, "end": v(-1150.1, 2504.01) * mm});
            skLineSegment(sketch, "E270", {"start": v(-1150.1, 2504.01) * mm, "end": v(-1173.19, 2507.3) * mm});
            skLineSegment(sketch, "E271", {"start": v(-1173.19, 2507.3) * mm, "end": v(-1196.28, 2510.3) * mm});
            skLineSegment(sketch, "E272", {"start": v(-1196.28, 2510.3) * mm, "end": v(-1219.38, 2513.05) * mm});
            skLineSegment(sketch, "E273", {"start": v(-1219.38, 2513.05) * mm, "end": v(-1242.48, 2515.53) * mm});
            skLineSegment(sketch, "E274", {"start": v(-1242.48, 2515.53) * mm, "end": v(-1265.59, 2517.75) * mm});
            skLineSegment(sketch, "E275", {"start": v(-1265.59, 2517.75) * mm, "end": v(-1288.7, 2519.7) * mm});
            skLineSegment(sketch, "E276", {"start": v(-1288.7, 2519.7) * mm, "end": v(-1311.8, 2521.39) * mm});
            skLineSegment(sketch, "E277", {"start": v(-1311.8, 2521.39) * mm, "end": v(-1334.9, 2522.81) * mm});
            skLineSegment(sketch, "E278", {"start": v(-1334.9, 2522.81) * mm, "end": v(-1358, 2523.98) * mm});
            skLineSegment(sketch, "E279", {"start": v(-1358, 2523.98) * mm, "end": v(-1381.09, 2524.89) * mm});
            skLineSegment(sketch, "E280", {"start": v(-1381.09, 2524.89) * mm, "end": v(-1404.17, 2525.53) * mm});
            skLineSegment(sketch, "E281", {"start": v(-1404.17, 2525.53) * mm, "end": v(-1427.23, 2525.93) * mm});
            skLineSegment(sketch, "E282", {"start": v(-1427.23, 2525.93) * mm, "end": v(-1450.29, 2526.06) * mm});
            skLineSegment(sketch, "E283", {"start": v(-1450.29, 2526.06) * mm, "end": v(-1473.33, 2525.94) * mm});
            skLineSegment(sketch, "E284", {"start": v(-1473.33, 2525.94) * mm, "end": v(-1496.35, 2525.57) * mm});
            skLineSegment(sketch, "E285", {"start": v(-1496.35, 2525.57) * mm, "end": v(-1519.35, 2524.94) * mm});
            skLineSegment(sketch, "E286", {"start": v(-1519.35, 2524.94) * mm, "end": v(-1542.33, 2524.06) * mm});
            skLineSegment(sketch, "E287", {"start": v(-1542.33, 2524.06) * mm, "end": v(-1565.29, 2522.93) * mm});
            skLineSegment(sketch, "E288", {"start": v(-1565.29, 2522.93) * mm, "end": v(-1588.22, 2521.55) * mm});
            skLineSegment(sketch, "E289", {"start": v(-1588.22, 2521.55) * mm, "end": v(-1611.12, 2519.93) * mm});
            skLineSegment(sketch, "E290", {"start": v(-1611.12, 2519.93) * mm, "end": v(-1634, 2518.05) * mm});
            skLineSegment(sketch, "E291", {"start": v(-1634, 2518.05) * mm, "end": v(-1656.84, 2515.93) * mm});
            skLineSegment(sketch, "E292", {"start": v(-1656.84, 2515.93) * mm, "end": v(-1679.65, 2513.57) * mm});
            skLineSegment(sketch, "E293", {"start": v(-1679.65, 2513.57) * mm, "end": v(-1702.43, 2510.96) * mm});
            skLineSegment(sketch, "E294", {"start": v(-1702.43, 2510.96) * mm, "end": v(-1725.17, 2508.1) * mm});
            skLineSegment(sketch, "E295", {"start": v(-1725.17, 2508.1) * mm, "end": v(-1747.86, 2505.01) * mm});
            skLineSegment(sketch, "E296", {"start": v(-1747.86, 2505.01) * mm, "end": v(-1770.52, 2501.68) * mm});
            skLineSegment(sketch, "E297", {"start": v(-1770.52, 2501.68) * mm, "end": v(-1793.13, 2498.1) * mm});
            skLineSegment(sketch, "E298", {"start": v(-1793.13, 2498.1) * mm, "end": v(-1815.7, 2494.29) * mm});
            skLineSegment(sketch, "E299", {"start": v(-1815.7, 2494.29) * mm, "end": v(-1838.22, 2490.24) * mm});
            skLineSegment(sketch, "E300", {"start": v(-1838.22, 2490.24) * mm, "end": v(-1860.7, 2485.95) * mm});
            skLineSegment(sketch, "E301", {"start": v(-1860.7, 2485.95) * mm, "end": v(-1883.12, 2481.43) * mm});
            skLineSegment(sketch, "E302", {"start": v(-1883.12, 2481.43) * mm, "end": v(-1905.48, 2476.68) * mm});
            skLineSegment(sketch, "E303", {"start": v(-1905.48, 2476.68) * mm, "end": v(-1927.8, 2471.69) * mm});
            skLineSegment(sketch, "E304", {"start": v(-1927.8, 2471.69) * mm, "end": v(-1950.05, 2466.46) * mm});
            skLineSegment(sketch, "E305", {"start": v(-1950.05, 2466.46) * mm, "end": v(-1972.24, 2461.01) * mm});
            skLineSegment(sketch, "E306", {"start": v(-1972.24, 2461.01) * mm, "end": v(-1994.37, 2455.33) * mm});
            skLineSegment(sketch, "E307", {"start": v(-1994.37, 2455.33) * mm, "end": v(-2016.45, 2449.42) * mm});
            skLineSegment(sketch, "E308", {"start": v(-2016.45, 2449.42) * mm, "end": v(-2038.45, 2443.29) * mm});
            skLineSegment(sketch, "E309", {"start": v(-2038.45, 2443.29) * mm, "end": v(-2060.39, 2436.92) * mm});
            skLineSegment(sketch, "E310", {"start": v(-2060.39, 2436.92) * mm, "end": v(-2082.26, 2430.34) * mm});
            skLineSegment(sketch, "E311", {"start": v(-2082.26, 2430.34) * mm, "end": v(-2104.05, 2423.53) * mm});
            skLineSegment(sketch, "E312", {"start": v(-2104.05, 2423.53) * mm, "end": v(-2125.78, 2416.49) * mm});
            skLineSegment(sketch, "E313", {"start": v(-2125.78, 2416.49) * mm, "end": v(-2147.43, 2409.23) * mm});
            skLineSegment(sketch, "E314", {"start": v(-2147.43, 2409.23) * mm, "end": v(-2169, 2401.76) * mm});
            skLineSegment(sketch, "E315", {"start": v(-2169, 2401.76) * mm, "end": v(-2190.49, 2394.06) * mm});
            skLineSegment(sketch, "E316", {"start": v(-2190.49, 2394.06) * mm, "end": v(-2211.9, 2386.14) * mm});
            skLineSegment(sketch, "E317", {"start": v(-2211.9, 2386.14) * mm, "end": v(-2233.23, 2378) * mm});
            skLineSegment(sketch, "E318", {"start": v(-2233.23, 2378) * mm, "end": v(-2254.47, 2369.66) * mm});
            skLineSegment(sketch, "E319", {"start": v(-2254.47, 2369.66) * mm, "end": v(-2275.62, 2361.1) * mm});
            skLineSegment(sketch, "E320", {"start": v(-2275.62, 2361.1) * mm, "end": v(-2296.69, 2352.31) * mm});
            skLineSegment(sketch, "E321", {"start": v(-2296.69, 2352.31) * mm, "end": v(-2317.66, 2343.32) * mm});
            skLineSegment(sketch, "E322", {"start": v(-2317.66, 2343.32) * mm, "end": v(-2338.54, 2334.12) * mm});
            skLineSegment(sketch, "E323", {"start": v(-2338.54, 2334.12) * mm, "end": v(-2359.33, 2324.7) * mm});
            skLineSegment(sketch, "E324", {"start": v(-2359.33, 2324.7) * mm, "end": v(-2380.02, 2315.08) * mm});
            skLineSegment(sketch, "E325", {"start": v(-2380.02, 2315.08) * mm, "end": v(-2400.6, 2305.25) * mm});
            skLineSegment(sketch, "E326", {"start": v(-2400.6, 2305.25) * mm, "end": v(-2421.1, 2295.2) * mm});
            skLineSegment(sketch, "E327", {"start": v(-2421.1, 2295.2) * mm, "end": v(-2441.48, 2284.96) * mm});
            skLineSegment(sketch, "E328", {"start": v(-2441.48, 2284.96) * mm, "end": v(-2461.76, 2274.5) * mm});
            skLineSegment(sketch, "E329", {"start": v(-2461.76, 2274.5) * mm, "end": v(-2481.93, 2263.85) * mm});
            skLineSegment(sketch, "E330", {"start": v(-2481.93, 2263.85) * mm, "end": v(-2502, 2253) * mm});
            skLineSegment(sketch, "E331", {"start": v(-2502, 2253) * mm, "end": v(-2521.95, 2241.93) * mm});
            skLineSegment(sketch, "E332", {"start": v(-2521.95, 2241.93) * mm, "end": v(-2541.79, 2230.67) * mm});
            skLineSegment(sketch, "E333", {"start": v(-2541.79, 2230.67) * mm, "end": v(-2561.51, 2219.2) * mm});
            skLineSegment(sketch, "E334", {"start": v(-2561.51, 2219.2) * mm, "end": v(-2581.12, 2207.54) * mm});
            skLineSegment(sketch, "E335", {"start": v(-2581.12, 2207.54) * mm, "end": v(-2600.6, 2195.68) * mm});
            skLineSegment(sketch, "E336", {"start": v(-2600.6, 2195.68) * mm, "end": v(-2619.97, 2183.63) * mm});
            skLineSegment(sketch, "E337", {"start": v(-2619.97, 2183.63) * mm, "end": v(-2639.21, 2171.38) * mm});
            skLineSegment(sketch, "E338", {"start": v(-2639.21, 2171.38) * mm, "end": v(-2658.33, 2158.93) * mm});
            skLineSegment(sketch, "E339", {"start": v(-2658.33, 2158.93) * mm, "end": v(-2677.32, 2146.3) * mm});
            skLineSegment(sketch, "E340", {"start": v(-2677.32, 2146.3) * mm, "end": v(-2696.18, 2133.47) * mm});
            skLineSegment(sketch, "E341", {"start": v(-2696.18, 2133.47) * mm, "end": v(-2714.91, 2120.45) * mm});
            skLineSegment(sketch, "E342", {"start": v(-2714.91, 2120.45) * mm, "end": v(-2733.51, 2107.24) * mm});
            skLineSegment(sketch, "E343", {"start": v(-2733.51, 2107.24) * mm, "end": v(-2751.97, 2093.84) * mm});
            skLineSegment(sketch, "E344", {"start": v(-2751.97, 2093.84) * mm, "end": v(-2770.3, 2080.25) * mm});
            skLineSegment(sketch, "E345", {"start": v(-2770.3, 2080.25) * mm, "end": v(-2788.48, 2066.48) * mm});
            skLineSegment(sketch, "E346", {"start": v(-2788.48, 2066.48) * mm, "end": v(-2806.53, 2052.52) * mm});
            skLineSegment(sketch, "E347", {"start": v(-2806.53, 2052.52) * mm, "end": v(-2824.43, 2038.38) * mm});
            skLineSegment(sketch, "E348", {"start": v(-2824.43, 2038.38) * mm, "end": v(-2842.19, 2024.05) * mm});
            skLineSegment(sketch, "E349", {"start": v(-2842.19, 2024.05) * mm, "end": v(-2859.8, 2009.54) * mm});
            skLineSegment(sketch, "E350", {"start": v(-2859.8, 2009.54) * mm, "end": v(-2877.25, 1994.85) * mm});
            skLineSegment(sketch, "E351", {"start": v(-2877.25, 1994.85) * mm, "end": v(-2894.56, 1979.98) * mm});
            skLineSegment(sketch, "E352", {"start": v(-2894.56, 1979.98) * mm, "end": v(-2911.72, 1964.94) * mm});
            skLineSegment(sketch, "E353", {"start": v(-2911.72, 1964.94) * mm, "end": v(-2928.72, 1949.71) * mm});
            skLineSegment(sketch, "E354", {"start": v(-2928.72, 1949.71) * mm, "end": v(-2945.56, 1934.3) * mm});
            skLineSegment(sketch, "E355", {"start": v(-2945.56, 1934.3) * mm, "end": v(-2962.25, 1918.73) * mm});
            skLineSegment(sketch, "E356", {"start": v(-2962.25, 1918.73) * mm, "end": v(-2978.77, 1902.98) * mm});
            skLineSegment(sketch, "E357", {"start": v(-2978.77, 1902.98) * mm, "end": v(-2995.13, 1887.05) * mm});
            skLineSegment(sketch, "E358", {"start": v(-2995.13, 1887.05) * mm, "end": v(-3011.32, 1870.96) * mm});
            skLineSegment(sketch, "E359", {"start": v(-3011.32, 1870.96) * mm, "end": v(-3027.35, 1854.7) * mm});
            skLineSegment(sketch, "E360", {"start": v(-3027.35, 1854.7) * mm, "end": v(-3043.21, 1838.25) * mm});
            skLineSegment(sketch, "E361", {"start": v(-3043.21, 1838.25) * mm, "end": v(-3058.9, 1821.65) * mm});
            skLineSegment(sketch, "E362", {"start": v(-3058.9, 1821.65) * mm, "end": v(-3074.42, 1804.87) * mm});
            skLineSegment(sketch, "E363", {"start": v(-3074.42, 1804.87) * mm, "end": v(-3089.76, 1787.93) * mm});
            skLineSegment(sketch, "E364", {"start": v(-3089.76, 1787.93) * mm, "end": v(-3104.92, 1770.82) * mm});
            skLineSegment(sketch, "E365", {"start": v(-3104.92, 1770.82) * mm, "end": v(-3119.9, 1753.55) * mm});
            skLineSegment(sketch, "E366", {"start": v(-3119.9, 1753.55) * mm, "end": v(-3134.7, 1736.12) * mm});
            skLineSegment(sketch, "E367", {"start": v(-3134.7, 1736.12) * mm, "end": v(-3149.32, 1718.52) * mm});
            skLineSegment(sketch, "E368", {"start": v(-3149.32, 1718.52) * mm, "end": v(-3163.76, 1700.77) * mm});
            skLineSegment(sketch, "E369", {"start": v(-3163.76, 1700.77) * mm, "end": v(-3178, 1682.85) * mm});
            skLineSegment(sketch, "E370", {"start": v(-3178, 1682.85) * mm, "end": v(-3192.06, 1664.77) * mm});
            skLineSegment(sketch, "E371", {"start": v(-3192.06, 1664.77) * mm, "end": v(-3205.93, 1646.54) * mm});
            skLineSegment(sketch, "E372", {"start": v(-3205.93, 1646.54) * mm, "end": v(-3219.6, 1628.15) * mm});
            skLineSegment(sketch, "E373", {"start": v(-3219.6, 1628.15) * mm, "end": v(-3233.08, 1609.6) * mm});
            skLineSegment(sketch, "E374", {"start": v(-3233.08, 1609.6) * mm, "end": v(-3246.37, 1590.9) * mm});
            skLineSegment(sketch, "E375", {"start": v(-3246.37, 1590.9) * mm, "end": v(-3259.45, 1572.05) * mm});
            skLineSegment(sketch, "E376", {"start": v(-3259.45, 1572.05) * mm, "end": v(-3272.33, 1553.04) * mm});
            skLineSegment(sketch, "E377", {"start": v(-3272.33, 1553.04) * mm, "end": v(-3285, 1533.88) * mm});
            skLineSegment(sketch, "E378", {"start": v(-3285, 1533.88) * mm, "end": v(-3297.48, 1514.57) * mm});
            skLineSegment(sketch, "E379", {"start": v(-3297.48, 1514.57) * mm, "end": v(-3309.75, 1495.12) * mm});
            skLineSegment(sketch, "E380", {"start": v(-3309.75, 1495.12) * mm, "end": v(-3321.8, 1475.51) * mm});
            skLineSegment(sketch, "E381", {"start": v(-3321.8, 1475.51) * mm, "end": v(-3333.66, 1455.76) * mm});
            skLineSegment(sketch, "E382", {"start": v(-3333.66, 1455.76) * mm, "end": v(-3345.3, 1435.87) * mm});
            skLineSegment(sketch, "E383", {"start": v(-3345.3, 1435.87) * mm, "end": v(-3356.71, 1415.83) * mm});
            skLineSegment(sketch, "E384", {"start": v(-3356.71, 1415.83) * mm, "end": v(-3367.91, 1395.64) * mm});
            skLineSegment(sketch, "E385", {"start": v(-3367.91, 1395.64) * mm, "end": v(-3378.9, 1375.32) * mm});
            skLineSegment(sketch, "E386", {"start": v(-3378.9, 1375.32) * mm, "end": v(-3389.66, 1354.85) * mm});
            skLineSegment(sketch, "E387", {"start": v(-3389.66, 1354.85) * mm, "end": v(-3400.2, 1334.24) * mm});
            skLineSegment(sketch, "E388", {"start": v(-3400.2, 1334.24) * mm, "end": v(-3410.51, 1313.5) * mm});
            skLineSegment(sketch, "E389", {"start": v(-3410.51, 1313.5) * mm, "end": v(-3420.6, 1292.6) * mm});
            skLineSegment(sketch, "E390", {"start": v(-3420.6, 1292.6) * mm, "end": v(-3430.46, 1271.59) * mm});
            skLineSegment(sketch, "E391", {"start": v(-3430.46, 1271.59) * mm, "end": v(-3440.09, 1250.43) * mm});
            skLineSegment(sketch, "E392", {"start": v(-3440.09, 1250.43) * mm, "end": v(-3449.48, 1229.14) * mm});
            skLineSegment(sketch, "E393", {"start": v(-3449.48, 1229.14) * mm, "end": v(-3458.64, 1207.71) * mm});
            skLineSegment(sketch, "E394", {"start": v(-3458.64, 1207.71) * mm, "end": v(-3467.56, 1186.16) * mm});
            skLineSegment(sketch, "E395", {"start": v(-3467.56, 1186.16) * mm, "end": v(-3476.25, 1164.47) * mm});
            skLineSegment(sketch, "E396", {"start": v(-3476.25, 1164.47) * mm, "end": v(-3484.69, 1142.65) * mm});
            skLineSegment(sketch, "E397", {"start": v(-3484.69, 1142.65) * mm, "end": v(-3492.89, 1120.7) * mm});
            skLineSegment(sketch, "E398", {"start": v(-3492.89, 1120.7) * mm, "end": v(-3500.84, 1098.63) * mm});
            skLineSegment(sketch, "E399", {"start": v(-3500.84, 1098.63) * mm, "end": v(-3508.55, 1076.42) * mm});
            skLineSegment(sketch, "E400", {"start": v(-3508.55, 1076.42) * mm, "end": v(-3516.01, 1054.1) * mm});
            skLineSegment(sketch, "E401", {"start": v(-3516.01, 1054.1) * mm, "end": v(-3523.22, 1031.64) * mm});
            skLineSegment(sketch, "E402", {"start": v(-3523.22, 1031.64) * mm, "end": v(-3530.18, 1009.07) * mm});
            skLineSegment(sketch, "E403", {"start": v(-3530.18, 1009.07) * mm, "end": v(-3536.88, 986.37) * mm});
            skLineSegment(sketch, "E404", {"start": v(-3536.88, 986.37) * mm, "end": v(-3543.32, 963.55) * mm});
            skLineSegment(sketch, "E405", {"start": v(-3543.32, 963.55) * mm, "end": v(-3549.5, 940.61) * mm});
            skLineSegment(sketch, "E406", {"start": v(-3549.5, 940.61) * mm, "end": v(-3555.55, 917.01) * mm});
            skLineSegment(sketch, "E407", {"start": v(-3555.55, 917.01) * mm, "end": v(-3561.27, 893.3) * mm});
            skLineSegment(sketch, "E408", {"start": v(-3561.27, 893.3) * mm, "end": v(-3566.68, 869.5) * mm});
            skLineSegment(sketch, "E409", {"start": v(-3566.68, 869.5) * mm, "end": v(-3571.78, 845.6) * mm});
            skLineSegment(sketch, "E410", {"start": v(-3571.78, 845.6) * mm, "end": v(-3576.57, 821.6) * mm});
            skLineSegment(sketch, "E411", {"start": v(-3576.57, 821.6) * mm, "end": v(-3581.05, 797.5) * mm});
            skLineSegment(sketch, "E412", {"start": v(-3581.05, 797.5) * mm, "end": v(-3585.23, 773.33) * mm});
            skLineSegment(sketch, "E413", {"start": v(-3585.23, 773.33) * mm, "end": v(-3589.1, 749.08) * mm});
            skLineSegment(sketch, "E414", {"start": v(-3589.1, 749.08) * mm, "end": v(-3592.65, 724.75) * mm});
            skLineSegment(sketch, "E415", {"start": v(-3592.65, 724.75) * mm, "end": v(-3595.9, 700.35) * mm});
            skLineSegment(sketch, "E416", {"start": v(-3595.9, 700.35) * mm, "end": v(-3598.85, 675.88) * mm});
            skLineSegment(sketch, "E417", {"start": v(-3598.85, 675.88) * mm, "end": v(-3601.5, 651.35) * mm});
            skLineSegment(sketch, "E418", {"start": v(-3601.5, 651.35) * mm, "end": v(-3603.85, 626.77) * mm});
            skLineSegment(sketch, "E419", {"start": v(-3603.85, 626.77) * mm, "end": v(-3605.9, 602.12) * mm});
            skLineSegment(sketch, "E420", {"start": v(-3605.9, 602.12) * mm, "end": v(-3607.64, 577.43) * mm});
            skLineSegment(sketch, "E421", {"start": v(-3607.64, 577.43) * mm, "end": v(-3609.1, 552.7) * mm});
            skLineSegment(sketch, "E422", {"start": v(-3609.1, 552.7) * mm, "end": v(-3610.25, 527.92) * mm});
            skLineSegment(sketch, "E423", {"start": v(-3610.25, 527.92) * mm, "end": v(-3611.1, 503.11) * mm});
            skLineSegment(sketch, "E424", {"start": v(-3611.1, 503.11) * mm, "end": v(-3611.67, 478.27) * mm});
            skLineSegment(sketch, "E425", {"start": v(-3611.67, 478.27) * mm, "end": v(-3611.94, 453.4) * mm});
            skLineSegment(sketch, "E426", {"start": v(-3611.94, 453.4) * mm, "end": v(-3611.92, 428.5) * mm});
            skLineSegment(sketch, "E427", {"start": v(-3611.92, 428.5) * mm, "end": v(-3611.6, 403.6) * mm});
            skLineSegment(sketch, "E428", {"start": v(-3611.6, 403.6) * mm, "end": v(-3611, 378.67) * mm});
            skLineSegment(sketch, "E429", {"start": v(-3611, 378.67) * mm, "end": v(-3610.12, 353.74) * mm});
            skLineSegment(sketch, "E430", {"start": v(-3610.12, 353.74) * mm, "end": v(-3608.94, 328.8) * mm});
            skLineSegment(sketch, "E431", {"start": v(-3608.94, 328.8) * mm, "end": v(-3607.48, 303.87) * mm});
            skLineSegment(sketch, "E432", {"start": v(-3607.48, 303.87) * mm, "end": v(-3605.74, 278.93) * mm});
            skLineSegment(sketch, "E433", {"start": v(-3605.74, 278.93) * mm, "end": v(-3603.7, 254) * mm});
            skLineSegment(sketch, "E434", {"start": v(-3603.7, 254) * mm, "end": v(-3601.4, 229.1) * mm});
            skLineSegment(sketch, "E435", {"start": v(-3601.4, 229.1) * mm, "end": v(-3598.8, 204.2) * mm});
            skLineSegment(sketch, "E436", {"start": v(-3598.8, 204.2) * mm, "end": v(-3595.93, 179.33) * mm});
            skLineSegment(sketch, "E437", {"start": v(-3595.93, 179.33) * mm, "end": v(-3592.78, 154.48) * mm});
            skLineSegment(sketch, "E438", {"start": v(-3592.78, 154.48) * mm, "end": v(-3589.35, 129.67) * mm});
            skLineSegment(sketch, "E439", {"start": v(-3589.35, 129.67) * mm, "end": v(-3585.65, 104.89) * mm});
            skLineSegment(sketch, "E440", {"start": v(-3585.65, 104.89) * mm, "end": v(-3581.67, 80.14) * mm});
            skLineSegment(sketch, "E441", {"start": v(-3581.67, 80.14) * mm, "end": v(-3577.41, 55.45) * mm});
            skLineSegment(sketch, "E442", {"start": v(-3577.41, 55.45) * mm, "end": v(-3572.89, 30.8) * mm});
            skLineSegment(sketch, "E443", {"start": v(-3572.89, 30.8) * mm, "end": v(-3568.09, 6.2) * mm});
            skLineSegment(sketch, "E444", {"start": v(-3568.09, 6.2) * mm, "end": v(-3563.02, -18.33) * mm});
            skLineSegment(sketch, "E445", {"start": v(-3563.02, -18.33) * mm, "end": v(-3557.68, -42.8) * mm});
            skLineSegment(sketch, "E446", {"start": v(-3557.68, -42.8) * mm, "end": v(-3552.08, -67.22) * mm});
            skLineSegment(sketch, "E447", {"start": v(-3552.08, -67.22) * mm, "end": v(-3546.2, -91.56) * mm});
            skLineSegment(sketch, "E448", {"start": v(-3546.2, -91.56) * mm, "end": v(-3540.07, -115.82) * mm});
            skLineSegment(sketch, "E449", {"start": v(-3540.07, -115.82) * mm, "end": v(-3533.67, -140) * mm});
            skLineSegment(sketch, "E450", {"start": v(-3533.67, -140) * mm, "end": v(-3527, -164.1) * mm});
            skLineSegment(sketch, "E451", {"start": v(-3527, -164.1) * mm, "end": v(-3520.07, -188.11) * mm});
            skLineSegment(sketch, "E452", {"start": v(-3520.07, -188.11) * mm, "end": v(-3512.88, -212.03) * mm});
            skLineSegment(sketch, "E453", {"start": v(-3512.88, -212.03) * mm, "end": v(-3505.44, -235.85) * mm});
            skLineSegment(sketch, "E454", {"start": v(-3505.44, -235.85) * mm, "end": v(-3497.73, -259.57) * mm});
            skLineSegment(sketch, "E455", {"start": v(-3497.73, -259.57) * mm, "end": v(-3489.77, -283.19) * mm});
            skLineSegment(sketch, "E456", {"start": v(-3489.77, -283.19) * mm, "end": v(-3481.55, -306.69) * mm});
            skLineSegment(sketch, "E457", {"start": v(-3481.55, -306.69) * mm, "end": v(-3473.07, -330.08) * mm});
            skLineSegment(sketch, "E458", {"start": v(-3473.07, -330.08) * mm, "end": v(-3464.34, -353.34) * mm});
            skLineSegment(sketch, "E459", {"start": v(-3464.34, -353.34) * mm, "end": v(-3455.37, -376.49) * mm});
            skLineSegment(sketch, "E460", {"start": v(-3455.37, -376.49) * mm, "end": v(-3446.13, -399.5) * mm});
            skLineSegment(sketch, "E461", {"start": v(-3446.13, -399.5) * mm, "end": v(-3436.65, -422.38) * mm});
            skLineSegment(sketch, "E462", {"start": v(-3436.65, -422.38) * mm, "end": v(-3426.92, -445.13) * mm});
            skLineSegment(sketch, "E463", {"start": v(-3426.92, -445.13) * mm, "end": v(-3416.94, -467.73) * mm});
            skLineSegment(sketch, "E464", {"start": v(-3416.94, -467.73) * mm, "end": v(-3406.72, -490.19) * mm});
            skLineSegment(sketch, "E465", {"start": v(-3406.72, -490.19) * mm, "end": v(-3396.25, -512.5) * mm});
            skLineSegment(sketch, "E466", {"start": v(-3396.25, -512.5) * mm, "end": v(-3385.53, -534.65) * mm});
            skLineSegment(sketch, "E467", {"start": v(-3385.53, -534.65) * mm, "end": v(-3374.58, -556.64) * mm});
            skLineSegment(sketch, "E468", {"start": v(-3374.58, -556.64) * mm, "end": v(-3363.38, -578.47) * mm});
            skLineSegment(sketch, "E469", {"start": v(-3363.38, -578.47) * mm, "end": v(-3351.94, -600.13) * mm});
            skLineSegment(sketch, "E470", {"start": v(-3351.94, -600.13) * mm, "end": v(-3340.26, -621.61) * mm});
            skLineSegment(sketch, "E471", {"start": v(-3340.26, -621.61) * mm, "end": v(-3328.34, -642.92) * mm});
            skLineSegment(sketch, "E472", {"start": v(-3328.34, -642.92) * mm, "end": v(-3316.19, -664.05) * mm});
            skLineSegment(sketch, "E473", {"start": v(-3316.19, -664.05) * mm, "end": v(-3303.8, -684.99) * mm});
            skLineSegment(sketch, "E474", {"start": v(-3303.8, -684.99) * mm, "end": v(-3290.21, -707.24) * mm});
            skLineSegment(sketch, "E475", {"start": v(-3290.21, -707.24) * mm, "end": v(-3276.32, -729.25) * mm});
            skLineSegment(sketch, "E476", {"start": v(-3276.32, -729.25) * mm, "end": v(-3262.11, -751.04) * mm});
            skLineSegment(sketch, "E477", {"start": v(-3262.11, -751.04) * mm, "end": v(-3247.62, -772.63) * mm});
            skLineSegment(sketch, "E478", {"start": v(-3247.62, -772.63) * mm, "end": v(-3232.84, -794) * mm});
            skLineSegment(sketch, "E479", {"start": v(-3232.84, -794) * mm, "end": v(-3217.8, -815.2) * mm});
            skLineSegment(sketch, "E480", {"start": v(-3217.8, -815.2) * mm, "end": v(-3202.5, -836.19) * mm});
            skLineSegment(sketch, "E481", {"start": v(-3202.5, -836.19) * mm, "end": v(-3186.96, -857) * mm});
            skLineSegment(sketch, "E482", {"start": v(-3186.96, -857) * mm, "end": v(-3171.18, -877.66) * mm});
            skLineSegment(sketch, "E483", {"start": v(-3171.18, -877.66) * mm, "end": v(-3155.2, -898.14) * mm});
            skLineSegment(sketch, "E484", {"start": v(-3155.2, -898.14) * mm, "end": v(-3139, -918.48) * mm});
            skLineSegment(sketch, "E485", {"start": v(-3139, -918.48) * mm, "end": v(-3122.62, -938.67) * mm});
            skLineSegment(sketch, "E486", {"start": v(-3122.62, -938.67) * mm, "end": v(-3106.06, -958.73) * mm});
            skLineSegment(sketch, "E487", {"start": v(-3106.06, -958.73) * mm, "end": v(-3089.33, -978.65) * mm});
            skLineSegment(sketch, "E488", {"start": v(-3089.33, -978.65) * mm, "end": v(-3072.44, -998.46) * mm});
            skLineSegment(sketch, "E489", {"start": v(-3072.44, -998.46) * mm, "end": v(-3055.42, -1018.16) * mm});
            skLineSegment(sketch, "E490", {"start": v(-3055.42, -1018.16) * mm, "end": v(-3038.26, -1037.76) * mm});
            skLineSegment(sketch, "E491", {"start": v(-3038.26, -1037.76) * mm, "end": v(-3021, -1057.26) * mm});
            skLineSegment(sketch, "E492", {"start": v(-3021, -1057.26) * mm, "end": v(-3003.62, -1076.68) * mm});
            skLineSegment(sketch, "E493", {"start": v(-3003.62, -1076.68) * mm, "end": v(-2986.15, -1096.02) * mm});
            skLineSegment(sketch, "E494", {"start": v(-2986.15, -1096.02) * mm, "end": v(-2968.61, -1115.3) * mm});
            skLineSegment(sketch, "E495", {"start": v(-2968.61, -1115.3) * mm, "end": v(-2951, -1134.51) * mm});
            skLineSegment(sketch, "E496", {"start": v(-2951, -1134.51) * mm, "end": v(-2933.34, -1153.68) * mm});
            skLineSegment(sketch, "E497", {"start": v(-2933.34, -1153.68) * mm, "end": v(-2915.64, -1172.8) * mm});
            skLineSegment(sketch, "E498", {"start": v(-2915.64, -1172.8) * mm, "end": v(-2897.9, -1191.88) * mm});
            skLineSegment(sketch, "E499", {"start": v(-2897.9, -1191.88) * mm, "end": v(-2880.16, -1210.94) * mm});
            skLineSegment(sketch, "E500", {"start": v(-2880.16, -1210.94) * mm, "end": v(-2862.42, -1229.99) * mm});
            skLineSegment(sketch, "E501", {"start": v(-2862.42, -1229.99) * mm, "end": v(-2844.68, -1249.03) * mm});
            skLineSegment(sketch, "E502", {"start": v(-2844.68, -1249.03) * mm, "end": v(-2826.96, -1268.06) * mm});
            skLineSegment(sketch, "E503", {"start": v(-2826.96, -1268.06) * mm, "end": v(-2809.29, -1287.1) * mm});
            skLineSegment(sketch, "E504", {"start": v(-2809.29, -1287.1) * mm, "end": v(-2791.65, -1306.17) * mm});
            skLineSegment(sketch, "E505", {"start": v(-2791.65, -1306.17) * mm, "end": v(-2774.08, -1325.26) * mm});
            skLineSegment(sketch, "E506", {"start": v(-2774.08, -1325.26) * mm, "end": v(-2756.59, -1344.38) * mm});
            skLineSegment(sketch, "E507", {"start": v(-2756.59, -1344.38) * mm, "end": v(-2739.17, -1363.54) * mm});
            skLineSegment(sketch, "E508", {"start": v(-2739.17, -1363.54) * mm, "end": v(-2721.84, -1382.69) * mm});
            skLineSegment(sketch, "E509", {"start": v(-2721.84, -1382.69) * mm, "end": v(-2704.51, -1401.84) * mm});
            skLineSegment(sketch, "E510", {"start": v(-2704.51, -1401.84) * mm, "end": v(-2687.18, -1421) * mm});
            skLineSegment(sketch, "E511", {"start": v(-2687.18, -1421) * mm, "end": v(-2669.84, -1440.15) * mm});
            skLineSegment(sketch, "E512", {"start": v(-2669.84, -1440.15) * mm, "end": v(-2652.5, -1459.31) * mm});
            skLineSegment(sketch, "E513", {"start": v(-2652.5, -1459.31) * mm, "end": v(-2635.17, -1478.48) * mm});
            skLineSegment(sketch, "E514", {"start": v(-2635.17, -1478.48) * mm, "end": v(-2617.84, -1497.64) * mm});
            skLineSegment(sketch, "E515", {"start": v(-2617.84, -1497.64) * mm, "end": v(-2600.5, -1516.8) * mm});
            skLineSegment(sketch, "E516", {"start": v(-2600.5, -1516.8) * mm, "end": v(-2583.16, -1535.98) * mm});
            skLineSegment(sketch, "E517", {"start": v(-2583.16, -1535.98) * mm, "end": v(-2565.82, -1555.16) * mm});
            skLineSegment(sketch, "E518", {"start": v(-2565.82, -1555.16) * mm, "end": v(-2548.48, -1574.33) * mm});
            skLineSegment(sketch, "E519", {"start": v(-2548.48, -1574.33) * mm, "end": v(-2531.14, -1593.51) * mm});
            skLineSegment(sketch, "E520", {"start": v(-2531.14, -1593.51) * mm, "end": v(-2513.8, -1612.7) * mm});
            skLineSegment(sketch, "E521", {"start": v(-2513.8, -1612.7) * mm, "end": v(-2496.46, -1631.88) * mm});
            skLineSegment(sketch, "E522", {"start": v(-2496.46, -1631.88) * mm, "end": v(-2479.12, -1651.07) * mm});
            skLineSegment(sketch, "E523", {"start": v(-2479.12, -1651.07) * mm, "end": v(-2461.79, -1670.26) * mm});
            skLineSegment(sketch, "E524", {"start": v(-2461.79, -1670.26) * mm, "end": v(-2444.45, -1689.45) * mm});
            skLineSegment(sketch, "E525", {"start": v(-2444.45, -1689.45) * mm, "end": v(-2427.11, -1708.65) * mm});
            skLineSegment(sketch, "E526", {"start": v(-2427.11, -1708.65) * mm, "end": v(-2409.78, -1727.85) * mm});
            skLineSegment(sketch, "E527", {"start": v(-2409.78, -1727.85) * mm, "end": v(-2392.45, -1747.05) * mm});
            skLineSegment(sketch, "E528", {"start": v(-2392.45, -1747.05) * mm, "end": v(-2375.12, -1766.26) * mm});
            skLineSegment(sketch, "E529", {"start": v(-2375.12, -1766.26) * mm, "end": v(-2357.79, -1785.46) * mm});
            skLineSegment(sketch, "E530", {"start": v(-2357.79, -1785.46) * mm, "end": v(-2340.46, -1804.67) * mm});
            skLineSegment(sketch, "E531", {"start": v(-2340.46, -1804.67) * mm, "end": v(-2323.13, -1823.89) * mm});
            skLineSegment(sketch, "E532", {"start": v(-2323.13, -1823.89) * mm, "end": v(-2305.8, -1843.1) * mm});
            skLineSegment(sketch, "E533", {"start": v(-2305.8, -1843.1) * mm, "end": v(-2288.49, -1862.32) * mm});
            skLineSegment(sketch, "E534", {"start": v(-2288.49, -1862.32) * mm, "end": v(-2271.17, -1881.54) * mm});
            skLineSegment(sketch, "E535", {"start": v(-2271.17, -1881.54) * mm, "end": v(-2253.85, -1900.76) * mm});
            skLineSegment(sketch, "E536", {"start": v(-2253.85, -1900.76) * mm, "end": v(-2236.54, -1919.99) * mm});
            skLineSegment(sketch, "E537", {"start": v(-2236.54, -1919.99) * mm, "end": v(-2219.23, -1939.21) * mm});
            skLineSegment(sketch, "E538", {"start": v(-2219.23, -1939.21) * mm, "end": v(-2201.93, -1958.44) * mm});
            skLineSegment(sketch, "E539", {"start": v(-2201.93, -1958.44) * mm, "end": v(-2184.62, -1977.68) * mm});
            skLineSegment(sketch, "E540", {"start": v(-2184.62, -1977.68) * mm, "end": v(-2167.33, -1996.91) * mm});
            skLineSegment(sketch, "E541", {"start": v(-2167.33, -1996.91) * mm, "end": v(-2150.03, -2016.15) * mm});
            skLineSegment(sketch, "E542", {"start": v(-2150.03, -2016.15) * mm, "end": v(-2132.74, -2035.4) * mm});
            skLineSegment(sketch, "E543", {"start": v(-2132.74, -2035.4) * mm, "end": v(-2115.46, -2054.63) * mm});
            skLineSegment(sketch, "E544", {"start": v(-2115.46, -2054.63) * mm, "end": v(-2098.17, -2073.88) * mm});
            skLineSegment(sketch, "E545", {"start": v(-2098.17, -2073.88) * mm, "end": v(-2080.9, -2093.13) * mm});
            skLineSegment(sketch, "E546", {"start": v(-2080.9, -2093.13) * mm, "end": v(-2063.63, -2112.38) * mm});
            skLineSegment(sketch, "E547", {"start": v(-2063.63, -2112.38) * mm, "end": v(-2046.36, -2131.63) * mm});
            skLineSegment(sketch, "E548", {"start": v(-2046.36, -2131.63) * mm, "end": v(-2029.1, -2150.88) * mm});
            skLineSegment(sketch, "E549", {"start": v(-2029.1, -2150.88) * mm, "end": v(-2011.84, -2170.14) * mm});
            skLineSegment(sketch, "E550", {"start": v(-2011.84, -2170.14) * mm, "end": v(-1994.6, -2189.4) * mm});
            skLineSegment(sketch, "E551", {"start": v(-1994.6, -2189.4) * mm, "end": v(-1977.34, -2208.66) * mm});
            skLineSegment(sketch, "E552", {"start": v(-1977.34, -2208.66) * mm, "end": v(-1960.1, -2227.93) * mm});
            skLineSegment(sketch, "E553", {"start": v(-1960.1, -2227.93) * mm, "end": v(-1942.87, -2247.2) * mm});
            skLineSegment(sketch, "E554", {"start": v(-1942.87, -2247.2) * mm, "end": v(-1925.65, -2266.46) * mm});
            skLineSegment(sketch, "E555", {"start": v(-1925.65, -2266.46) * mm, "end": v(-1908.43, -2285.74) * mm});
            skLineSegment(sketch, "E556", {"start": v(-1908.43, -2285.74) * mm, "end": v(-1891.21, -2305) * mm});
            skLineSegment(sketch, "E557", {"start": v(-1891.21, -2305) * mm, "end": v(-1874, -2324.29) * mm});
            skLineSegment(sketch, "E558", {"start": v(-1874, -2324.29) * mm, "end": v(-1856.8, -2343.56) * mm});
            skLineSegment(sketch, "E559", {"start": v(-1856.8, -2343.56) * mm, "end": v(-1839.62, -2362.85) * mm});
            skLineSegment(sketch, "E560", {"start": v(-1839.62, -2362.85) * mm, "end": v(-1822.43, -2382.13) * mm});
            skLineSegment(sketch, "E561", {"start": v(-1822.43, -2382.13) * mm, "end": v(-1805.25, -2401.41) * mm});
            skLineSegment(sketch, "E562", {"start": v(-1805.25, -2401.41) * mm, "end": v(-1788.22, -2420.54) * mm});
            skLineSegment(sketch, "E563", {"start": v(-1788.22, -2420.54) * mm, "end": v(-1771.2, -2439.68) * mm});
            skLineSegment(sketch, "E564", {"start": v(-1771.2, -2439.68) * mm, "end": v(-1754.16, -2458.83) * mm});
            skLineSegment(sketch, "E565", {"start": v(-1754.16, -2458.83) * mm, "end": v(-1737.13, -2478) * mm});
            skLineSegment(sketch, "E566", {"start": v(-1737.13, -2478) * mm, "end": v(-1720.1, -2497.16) * mm});
            skLineSegment(sketch, "E567", {"start": v(-1720.1, -2497.16) * mm, "end": v(-1703.05, -2516.34) * mm});
            skLineSegment(sketch, "E568", {"start": v(-1703.05, -2516.34) * mm, "end": v(-1686, -2535.52) * mm});
            skLineSegment(sketch, "E569", {"start": v(-1686, -2535.52) * mm, "end": v(-1668.96, -2554.7) * mm});
            skLineSegment(sketch, "E570", {"start": v(-1668.96, -2554.7) * mm, "end": v(-1651.9, -2573.9) * mm});
            skLineSegment(sketch, "E571", {"start": v(-1651.9, -2573.9) * mm, "end": v(-1634.85, -2593.1) * mm});
            skLineSegment(sketch, "E572", {"start": v(-1634.85, -2593.1) * mm, "end": v(-1617.78, -2612.3) * mm});
            skLineSegment(sketch, "E573", {"start": v(-1617.78, -2612.3) * mm, "end": v(-1600.7, -2631.5) * mm});
            skLineSegment(sketch, "E574", {"start": v(-1600.7, -2631.5) * mm, "end": v(-1583.63, -2650.7) * mm});
            skLineSegment(sketch, "E575", {"start": v(-1583.63, -2650.7) * mm, "end": v(-1566.54, -2669.9) * mm});
            skLineSegment(sketch, "E576", {"start": v(-1566.54, -2669.9) * mm, "end": v(-1549.45, -2689.1) * mm});
            skLineSegment(sketch, "E577", {"start": v(-1549.45, -2689.1) * mm, "end": v(-1532.35, -2708.3) * mm});
            skLineSegment(sketch, "E578", {"start": v(-1532.35, -2708.3) * mm, "end": v(-1515.23, -2727.5) * mm});
            skLineSegment(sketch, "E579", {"start": v(-1515.23, -2727.5) * mm, "end": v(-1498.11, -2746.68) * mm});
            skLineSegment(sketch, "E580", {"start": v(-1498.11, -2746.68) * mm, "end": v(-1480.98, -2765.87) * mm});
            skLineSegment(sketch, "E581", {"start": v(-1480.98, -2765.87) * mm, "end": v(-1463.84, -2785.05) * mm});
            skLineSegment(sketch, "E582", {"start": v(-1463.84, -2785.05) * mm, "end": v(-1446.68, -2804.22) * mm});
            skLineSegment(sketch, "E583", {"start": v(-1446.68, -2804.22) * mm, "end": v(-1429.52, -2823.4) * mm});
            skLineSegment(sketch, "E584", {"start": v(-1429.52, -2823.4) * mm, "end": v(-1412.34, -2842.55) * mm});
            skLineSegment(sketch, "E585", {"start": v(-1412.34, -2842.55) * mm, "end": v(-1395.15, -2861.7) * mm});
            skLineSegment(sketch, "E586", {"start": v(-1395.15, -2861.7) * mm, "end": v(-1377.94, -2880.84) * mm});
            skLineSegment(sketch, "E587", {"start": v(-1377.94, -2880.84) * mm, "end": v(-1360.72, -2899.97) * mm});
            skLineSegment(sketch, "E588", {"start": v(-1360.72, -2899.97) * mm, "end": v(-1343.48, -2919.08) * mm});
            skLineSegment(sketch, "E589", {"start": v(-1343.48, -2919.08) * mm, "end": v(-1326.24, -2938.18) * mm});
            skLineSegment(sketch, "E590", {"start": v(-1326.24, -2938.18) * mm, "end": v(-1308.97, -2957.27) * mm});
            skLineSegment(sketch, "E591", {"start": v(-1308.97, -2957.27) * mm, "end": v(-1291.69, -2976.35) * mm});
            skLineSegment(sketch, "E592", {"start": v(-1291.69, -2976.35) * mm, "end": v(-1274.39, -2995.4) * mm});
            skLineSegment(sketch, "E593", {"start": v(-1274.39, -2995.4) * mm, "end": v(-1257.07, -3014.45) * mm});
            skLineSegment(sketch, "E594", {"start": v(-1257.07, -3014.45) * mm, "end": v(-1239.74, -3033.47) * mm});
            skLineSegment(sketch, "E595", {"start": v(-1239.74, -3033.47) * mm, "end": v(-1222.39, -3052.48) * mm});
            skLineSegment(sketch, "E596", {"start": v(-1222.39, -3052.48) * mm, "end": v(-1205.01, -3071.46) * mm});
            skLineSegment(sketch, "E597", {"start": v(-1205.01, -3071.46) * mm, "end": v(-1187.62, -3090.43) * mm});
            skLineSegment(sketch, "E598", {"start": v(-1187.62, -3090.43) * mm, "end": v(-1170.21, -3109.37) * mm});
            skLineSegment(sketch, "E599", {"start": v(-1170.21, -3109.37) * mm, "end": v(-1152.78, -3128.29) * mm});
            skLineSegment(sketch, "E600", {"start": v(-1152.78, -3128.29) * mm, "end": v(-1135.33, -3147.19) * mm});
            skLineSegment(sketch, "E601", {"start": v(-1135.33, -3147.19) * mm, "end": v(-1117.85, -3166.06) * mm});
            skLineSegment(sketch, "E602", {"start": v(-1117.85, -3166.06) * mm, "end": v(-1100.36, -3184.91) * mm});
            skLineSegment(sketch, "E603", {"start": v(-1100.36, -3184.91) * mm, "end": v(-1082.84, -3203.74) * mm});
            skLineSegment(sketch, "E604", {"start": v(-1082.84, -3203.74) * mm, "end": v(-1065.3, -3222.53) * mm});
            skLineSegment(sketch, "E605", {"start": v(-1065.3, -3222.53) * mm, "end": v(-1047.72, -3241.3) * mm});
            skLineSegment(sketch, "E606", {"start": v(-1047.72, -3241.3) * mm, "end": v(-1030.13, -3260.04) * mm});
            skLineSegment(sketch, "E607", {"start": v(-1030.13, -3260.04) * mm, "end": v(-1012.52, -3278.75) * mm});
            skLineSegment(sketch, "E608", {"start": v(-1012.52, -3278.75) * mm, "end": v(-994.87, -3297.43) * mm});
            skLineSegment(sketch, "E609", {"start": v(-994.87, -3297.43) * mm, "end": v(-977.2, -3316.07) * mm});
            skLineSegment(sketch, "E610", {"start": v(-977.2, -3316.07) * mm, "end": v(-959.51, -3334.69) * mm});
            skLineSegment(sketch, "E611", {"start": v(-959.51, -3334.69) * mm, "end": v(-941.8, -3353.27) * mm});
            skLineSegment(sketch, "E612", {"start": v(-941.8, -3353.27) * mm, "end": v(-924.04, -3371.81) * mm});
            skLineSegment(sketch, "E613", {"start": v(-924.04, -3371.81) * mm, "end": v(-906.26, -3390.33) * mm});
            skLineSegment(sketch, "E614", {"start": v(-906.26, -3390.33) * mm, "end": v(-888.46, -3408.8) * mm});
            skLineSegment(sketch, "E615", {"start": v(-888.46, -3408.8) * mm, "end": v(-870.62, -3427.24) * mm});
            skLineSegment(sketch, "E616", {"start": v(-870.62, -3427.24) * mm, "end": v(-852.75, -3445.64) * mm});
            skLineSegment(sketch, "E617", {"start": v(-852.75, -3445.64) * mm, "end": v(-834.86, -3464) * mm});
            skLineSegment(sketch, "E618", {"start": v(-834.86, -3464) * mm, "end": v(-816.93, -3482.32) * mm});
            skLineSegment(sketch, "E619", {"start": v(-816.93, -3482.32) * mm, "end": v(-798.97, -3500.6) * mm});
            skLineSegment(sketch, "E620", {"start": v(-798.97, -3500.6) * mm, "end": v(-780.98, -3518.84) * mm});
            skLineSegment(sketch, "E621", {"start": v(-780.98, -3518.84) * mm, "end": v(-762.96, -3537.04) * mm});
            skLineSegment(sketch, "E622", {"start": v(-762.96, -3537.04) * mm, "end": v(-744.9, -3555.19) * mm});
            skLineSegment(sketch, "E623", {"start": v(-744.9, -3555.19) * mm, "end": v(-729.57, -3570.5) * mm});
            skLineSegment(sketch, "E624", {"start": v(-729.57, -3570.5) * mm, "end": v(-713.89, -3585.94) * mm});
            skLineSegment(sketch, "E625", {"start": v(-713.89, -3585.94) * mm, "end": v(-697.88, -3601.43) * mm});
            skLineSegment(sketch, "E626", {"start": v(-697.88, -3601.43) * mm, "end": v(-681.56, -3616.85) * mm});
            skLineSegment(sketch, "E627", {"start": v(-681.56, -3616.85) * mm, "end": v(-664.94, -3632.12) * mm});
            skLineSegment(sketch, "E628", {"start": v(-664.94, -3632.12) * mm, "end": v(-648.03, -3647.13) * mm});
            skLineSegment(sketch, "E629", {"start": v(-648.03, -3647.13) * mm, "end": v(-630.85, -3661.8) * mm});
            skLineSegment(sketch, "E630", {"start": v(-630.85, -3661.8) * mm, "end": v(-613.4, -3676) * mm});
            skLineSegment(sketch, "E631", {"start": v(-613.4, -3676) * mm, "end": v(-595.73, -3689.67) * mm});
            skLineSegment(sketch, "E632", {"start": v(-595.73, -3689.67) * mm, "end": v(-577.82, -3702.7) * mm});
            skLineSegment(sketch, "E633", {"start": v(-577.82, -3702.7) * mm, "end": v(-559.7, -3714.97) * mm});
            skLineSegment(sketch, "E634", {"start": v(-559.7, -3714.97) * mm, "end": v(-541.38, -3726.4) * mm});
            skLineSegment(sketch, "E635", {"start": v(-541.38, -3726.4) * mm, "end": v(-522.87, -3736.9) * mm});
            skLineSegment(sketch, "E636", {"start": v(-522.87, -3736.9) * mm, "end": v(-504.2, -3746.35) * mm});
            skLineSegment(sketch, "E637", {"start": v(-504.2, -3746.35) * mm, "end": v(-485.37, -3754.67) * mm});
            skLineSegment(sketch, "E638", {"start": v(-485.37, -3754.67) * mm, "end": v(-466.4, -3761.76) * mm});
            skLineSegment(sketch, "E639", {"start": v(-466.4, -3761.76) * mm, "end": v(-447.3, -3767.52) * mm});
            skLineSegment(sketch, "E640", {"start": v(-447.3, -3767.52) * mm, "end": v(-428.1, -3771.85) * mm});
            skLineSegment(sketch, "E641", {"start": v(-428.1, -3771.85) * mm, "end": v(-408.8, -3774.66) * mm});
            skLineSegment(sketch, "E642", {"start": v(-408.8, -3774.66) * mm, "end": v(-389.4, -3775.84) * mm});
            skLineSegment(sketch, "E643", {"start": v(-389.4, -3775.84) * mm, "end": v(-369.95, -3775.3) * mm});
            skLineSegment(sketch, "E644", {"start": v(-369.95, -3775.3) * mm, "end": v(-350.44, -3772.93) * mm});
            skLineSegment(sketch, "E645", {"start": v(-350.44, -3772.93) * mm, "end": v(-330.9, -3768.65) * mm});
            skLineSegment(sketch, "E646", {"start": v(-330.9, -3768.65) * mm, "end": v(-311.32, -3762.35) * mm});
            skLineSegment(sketch, "E647", {"start": v(-311.32, -3762.35) * mm, "end": v(-291.74, -3753.94) * mm});
            skLineSegment(sketch, "E648", {"start": v(-291.74, -3753.94) * mm, "end": v(-272.16, -3743.32) * mm});
            skLineSegment(sketch, "E649", {"start": v(-272.16, -3743.32) * mm, "end": v(-252.6, -3730.4) * mm});
            skLineSegment(sketch, "E650", {"start": v(-252.6, -3730.4) * mm, "end": v(-233.08, -3715.05) * mm});
            skLineSegment(sketch, "E651", {"start": v(-233.08, -3715.05) * mm, "end": v(-213.6, -3697.2) * mm});
            skLineSegment(sketch, "E652", {"start": v(-213.6, -3697.2) * mm, "end": v(-194.2, -3676.76) * mm});
            skLineSegment(sketch, "E653", {"start": v(-194.2, -3676.76) * mm, "end": v(-177.59, -3655.47) * mm});
            skLineSegment(sketch, "E654", {"start": v(-177.59, -3655.47) * mm, "end": v(-164.3, -3633.01) * mm});
            skLineSegment(sketch, "E655", {"start": v(-164.3, -3633.01) * mm, "end": v(-153.97, -3609.55) * mm});
            skLineSegment(sketch, "E656", {"start": v(-153.97, -3609.55) * mm, "end": v(-146.25, -3585.22) * mm});
            skLineSegment(sketch, "E657", {"start": v(-146.25, -3585.22) * mm, "end": v(-140.77, -3560.18) * mm});
            skLineSegment(sketch, "E658", {"start": v(-140.77, -3560.18) * mm, "end": v(-137.18, -3534.58) * mm});
            skLineSegment(sketch, "E659", {"start": v(-137.18, -3534.58) * mm, "end": v(-135.13, -3508.56) * mm});
            skLineSegment(sketch, "E660", {"start": v(-135.13, -3508.56) * mm, "end": v(-134.24, -3482.27) * mm});
            skLineSegment(sketch, "E661", {"start": v(-134.24, -3482.27) * mm, "end": v(-134.18, -3455.86) * mm});
            skLineSegment(sketch, "E662", {"start": v(-134.18, -3455.86) * mm, "end": v(-134.58, -3429.48) * mm});
            skLineSegment(sketch, "E663", {"start": v(-134.58, -3429.48) * mm, "end": v(-135.07, -3403.27) * mm});
            skLineSegment(sketch, "E664", {"start": v(-135.07, -3403.27) * mm, "end": v(-135.32, -3377.39) * mm});
            skLineSegment(sketch, "E665", {"start": v(-135.32, -3377.39) * mm, "end": v(-135.32, -2742.39) * mm});
            skLineSegment(sketch, "E666", {"start": v(-135.32, -2742.39) * mm, "end": v(-135.32, -1497.79) * mm});
            skLineSegment(sketch, "E667", {"start": v(-135.32, -1497.79) * mm, "end": v(-135.19, -1473.15) * mm});
            skLineSegment(sketch, "E668", {"start": v(-135.19, -1473.15) * mm, "end": v(-134.81, -1448.29) * mm});
            skLineSegment(sketch, "E669", {"start": v(-134.81, -1448.29) * mm, "end": v(-134.23, -1423.23) * mm});
            skLineSegment(sketch, "E670", {"start": v(-134.23, -1423.23) * mm, "end": v(-133.48, -1398) * mm});
            skLineSegment(sketch, "E671", {"start": v(-133.48, -1398) * mm, "end": v(-132.6, -1372.61) * mm});
            skLineSegment(sketch, "E672", {"start": v(-132.6, -1372.61) * mm, "end": v(-131.62, -1347.09) * mm});
            skLineSegment(sketch, "E673", {"start": v(-131.62, -1347.09) * mm, "end": v(-130.57, -1321.45) * mm});
            skLineSegment(sketch, "E674", {"start": v(-130.57, -1321.45) * mm, "end": v(-129.49, -1295.72) * mm});
            skLineSegment(sketch, "E675", {"start": v(-129.49, -1295.72) * mm, "end": v(-128.42, -1269.9) * mm});
            skLineSegment(sketch, "E676", {"start": v(-128.42, -1269.9) * mm, "end": v(-127.39, -1244.04) * mm});
            skLineSegment(sketch, "E677", {"start": v(-127.39, -1244.04) * mm, "end": v(-126.44, -1218.14) * mm});
            skLineSegment(sketch, "E678", {"start": v(-126.44, -1218.14) * mm, "end": v(-125.6, -1192.22) * mm});
            skLineSegment(sketch, "E679", {"start": v(-125.6, -1192.22) * mm, "end": v(-124.9, -1166.3) * mm});
            skLineSegment(sketch, "E680", {"start": v(-124.9, -1166.3) * mm, "end": v(-124.4, -1140.41) * mm});
            skLineSegment(sketch, "E681", {"start": v(-124.4, -1140.41) * mm, "end": v(-124.1, -1114.56) * mm});
            skLineSegment(sketch, "E682", {"start": v(-124.1, -1114.56) * mm, "end": v(-124.07, -1088.78) * mm});
            skLineSegment(sketch, "E683", {"start": v(-124.07, -1088.78) * mm, "end": v(-124.33, -1063.07) * mm});
            skLineSegment(sketch, "E684", {"start": v(-124.33, -1063.07) * mm, "end": v(-124.9, -1037.47) * mm});
            skLineSegment(sketch, "E685", {"start": v(-124.9, -1037.47) * mm, "end": v(-125.84, -1012) * mm});
            skLineSegment(sketch, "E686", {"start": v(-125.84, -1012) * mm, "end": v(-127.18, -986.66) * mm});
            skLineSegment(sketch, "E687", {"start": v(-127.18, -986.66) * mm, "end": v(-128.94, -961.48) * mm});
            skLineSegment(sketch, "E688", {"start": v(-128.94, -961.48) * mm, "end": v(-131.18, -936.5) * mm});
            skLineSegment(sketch, "E689", {"start": v(-131.18, -936.5) * mm, "end": v(-133.9, -911.7) * mm});
            skLineSegment(sketch, "E690", {"start": v(-133.9, -911.7) * mm, "end": v(-137.18, -887.14) * mm});
            skLineSegment(sketch, "E691", {"start": v(-137.18, -887.14) * mm, "end": v(-141.02, -862.81) * mm});
            skLineSegment(sketch, "E692", {"start": v(-141.02, -862.81) * mm, "end": v(-146.7, -836.37) * mm});
            skLineSegment(sketch, "E693", {"start": v(-146.7, -836.37) * mm, "end": v(-154.5, -810.8) * mm});
            skLineSegment(sketch, "E694", {"start": v(-154.5, -810.8) * mm, "end": v(-164.42, -786.25) * mm});
            skLineSegment(sketch, "E695", {"start": v(-164.42, -786.25) * mm, "end": v(-176.4, -762.87) * mm});
            skLineSegment(sketch, "E696", {"start": v(-176.4, -762.87) * mm, "end": v(-190.44, -740.8) * mm});
            skLineSegment(sketch, "E697", {"start": v(-190.44, -740.8) * mm, "end": v(-206.48, -720.2) * mm});
            skLineSegment(sketch, "E698", {"start": v(-206.48, -720.2) * mm, "end": v(-224.5, -701.23) * mm});
            skLineSegment(sketch, "E699", {"start": v(-224.5, -701.23) * mm, "end": v(-244.45, -684.02) * mm});
            skLineSegment(sketch, "E700", {"start": v(-244.45, -684.02) * mm, "end": v(-266.32, -668.72) * mm});
            skLineSegment(sketch, "E701", {"start": v(-266.32, -668.72) * mm, "end": v(-290.07, -655.5) * mm});
            skLineSegment(sketch, "E702", {"start": v(-290.07, -655.5) * mm, "end": v(-312.81, -645.79) * mm});
            skLineSegment(sketch, "E703", {"start": v(-312.81, -645.79) * mm, "end": v(-336.24, -637.63) * mm});
            skLineSegment(sketch, "E704", {"start": v(-336.24, -637.63) * mm, "end": v(-359.66, -629.74) * mm});
            skLineSegment(sketch, "E705", {"start": v(-359.66, -629.74) * mm, "end": v(-382.38, -620.85) * mm});
            skLineSegment(sketch, "E706", {"start": v(-382.38, -620.85) * mm, "end": v(-403.71, -609.67) * mm});
            skLineSegment(sketch, "E707", {"start": v(-403.71, -609.67) * mm, "end": v(-422.96, -594.92) * mm});
            skLineSegment(sketch, "E708", {"start": v(-422.96, -594.92) * mm, "end": v(-439.41, -575.34) * mm});
            skLineSegment(sketch, "E709", {"start": v(-439.41, -575.34) * mm, "end": v(-449.65, -557.55) * mm});
            skLineSegment(sketch, "E710", {"start": v(-449.65, -557.55) * mm, "end": v(-458.25, -537.85) * mm});
            skLineSegment(sketch, "E711", {"start": v(-458.25, -537.85) * mm, "end": v(-465.32, -516.44) * mm});
            skLineSegment(sketch, "E712", {"start": v(-465.32, -516.44) * mm, "end": v(-470.99, -493.49) * mm});
            skLineSegment(sketch, "E713", {"start": v(-470.99, -493.49) * mm, "end": v(-475.36, -469.2) * mm});
            skLineSegment(sketch, "E714", {"start": v(-475.36, -469.2) * mm, "end": v(-478.56, -443.75) * mm});
            skLineSegment(sketch, "E715", {"start": v(-478.56, -443.75) * mm, "end": v(-480.7, -417.33) * mm});
            skLineSegment(sketch, "E716", {"start": v(-480.7, -417.33) * mm, "end": v(-481.92, -390.12) * mm});
            skLineSegment(sketch, "E717", {"start": v(-481.92, -390.12) * mm, "end": v(-482.3, -362.32) * mm});
            skLineSegment(sketch, "E718", {"start": v(-482.3, -362.32) * mm, "end": v(-481.99, -334.1) * mm});
            skLineSegment(sketch, "E719", {"start": v(-481.99, -334.1) * mm, "end": v(-481.08, -305.66) * mm});
            skLineSegment(sketch, "E720", {"start": v(-481.08, -305.66) * mm, "end": v(-479.7, -277.19) * mm});
            skLineSegment(sketch, "E721", {"start": v(-479.7, -277.19) * mm, "end": v(-477.98, -248.86) * mm});
            skLineSegment(sketch, "E722", {"start": v(-477.98, -248.86) * mm, "end": v(-476.01, -220.87) * mm});
            skLineSegment(sketch, "E723", {"start": v(-476.01, -220.87) * mm, "end": v(-473.93, -193.4) * mm});
            skLineSegment(sketch, "E724", {"start": v(-473.93, -193.4) * mm, "end": v(-471.85, -166.63) * mm});
            skLineSegment(sketch, "E725", {"start": v(-471.85, -166.63) * mm, "end": v(-469.88, -140.77) * mm});
            skLineSegment(sketch, "E726", {"start": v(-469.88, -140.77) * mm, "end": v(-468.15, -115.98) * mm});
            skLineSegment(sketch, "E727", {"start": v(-468.15, -115.98) * mm, "end": v(-466.77, -92.47) * mm});
            skLineSegment(sketch, "E728", {"start": v(-466.77, -92.47) * mm, "end": v(-465.85, -70.4) * mm});
            skLineSegment(sketch, "E729", {"start": v(-465.85, -70.4) * mm, "end": v(-465.52, -49.99) * mm});
            skLineSegment(sketch, "E730", {"start": v(-465.52, -49.99) * mm, "end": v(-465.52, 661.21) * mm});
            skLineSegment(sketch, "E731", {"start": v(-465.52, 661.21) * mm, "end": v(-465.44, 686.29) * mm});
            skLineSegment(sketch, "E732", {"start": v(-465.44, 686.29) * mm, "end": v(-465.15, 711.33) * mm});
            skLineSegment(sketch, "E733", {"start": v(-465.15, 711.33) * mm, "end": v(-464.6, 736.3) * mm});
            skLineSegment(sketch, "E734", {"start": v(-464.6, 736.3) * mm, "end": v(-463.7, 761.16) * mm});
            skLineSegment(sketch, "E735", {"start": v(-463.7, 761.16) * mm, "end": v(-462.43, 785.89) * mm});
            skLineSegment(sketch, "E736", {"start": v(-462.43, 785.89) * mm, "end": v(-460.71, 810.44) * mm});
            skLineSegment(sketch, "E737", {"start": v(-460.71, 810.44) * mm, "end": v(-458.47, 834.8) * mm});
            skLineSegment(sketch, "E738", {"start": v(-458.47, 834.8) * mm, "end": v(-455.66, 858.9) * mm});
            skLineSegment(sketch, "E739", {"start": v(-455.66, 858.9) * mm, "end": v(-452.21, 882.75) * mm});
            skLineSegment(sketch, "E740", {"start": v(-452.21, 882.75) * mm, "end": v(-448.07, 906.28) * mm});
            skLineSegment(sketch, "E741", {"start": v(-448.07, 906.28) * mm, "end": v(-443.17, 929.48) * mm});
            skLineSegment(sketch, "E742", {"start": v(-443.17, 929.48) * mm, "end": v(-437.45, 952.3) * mm});
            skLineSegment(sketch, "E743", {"start": v(-437.45, 952.3) * mm, "end": v(-430.85, 974.73) * mm});
            skLineSegment(sketch, "E744", {"start": v(-430.85, 974.73) * mm, "end": v(-423.3, 996.72) * mm});
            skLineSegment(sketch, "E745", {"start": v(-423.3, 996.72) * mm, "end": v(-414.75, 1018.23) * mm});
            skLineSegment(sketch, "E746", {"start": v(-414.75, 1018.23) * mm, "end": v(-405.14, 1039.24) * mm});
            skLineSegment(sketch, "E747", {"start": v(-405.14, 1039.24) * mm, "end": v(-394.4, 1059.7) * mm});
            skLineSegment(sketch, "E748", {"start": v(-394.4, 1059.7) * mm, "end": v(-382.47, 1079.6) * mm});
            skLineSegment(sketch, "E749", {"start": v(-382.47, 1079.6) * mm, "end": v(-369.3, 1098.9) * mm});
            skLineSegment(sketch, "E750", {"start": v(-369.3, 1098.9) * mm, "end": v(-354.8, 1117.55) * mm});
            skLineSegment(sketch, "E751", {"start": v(-354.8, 1117.55) * mm, "end": v(-338.95, 1135.53) * mm});
            skLineSegment(sketch, "E752", {"start": v(-338.95, 1135.53) * mm, "end": v(-321.65, 1152.81) * mm});
            skLineSegment(sketch, "E753", {"start": v(-321.65, 1152.81) * mm, "end": v(-302.86, 1169.35) * mm});
            skLineSegment(sketch, "E754", {"start": v(-302.86, 1169.35) * mm, "end": v(-282.51, 1185.12) * mm});
            skLineSegment(sketch, "E755", {"start": v(-282.51, 1185.12) * mm, "end": v(-260.55, 1200.08) * mm});
            skLineSegment(sketch, "E756", {"start": v(-260.55, 1200.08) * mm, "end": v(-236.9, 1214.2) * mm});
            skLineSegment(sketch, "E757", {"start": v(-236.9, 1214.2) * mm, "end": v(-215.8, 1225.31) * mm});
            skLineSegment(sketch, "E758", {"start": v(-215.8, 1225.31) * mm, "end": v(-194.45, 1235.22) * mm});
            skLineSegment(sketch, "E759", {"start": v(-194.45, 1235.22) * mm, "end": v(-172.86, 1243.94) * mm});
            skLineSegment(sketch, "E760", {"start": v(-172.86, 1243.94) * mm, "end": v(-151.1, 1251.5) * mm});
            skLineSegment(sketch, "E761", {"start": v(-151.1, 1251.5) * mm, "end": v(-129.17, 1257.9) * mm});
            skLineSegment(sketch, "E762", {"start": v(-129.17, 1257.9) * mm, "end": v(-107.12, 1263.18) * mm});
            skLineSegment(sketch, "E763", {"start": v(-107.12, 1263.18) * mm, "end": v(-84.99, 1267.34) * mm});
            skLineSegment(sketch, "E764", {"start": v(-84.99, 1267.34) * mm, "end": v(-62.8, 1270.41) * mm});
            skLineSegment(sketch, "E765", {"start": v(-62.8, 1270.41) * mm, "end": v(-40.6, 1272.4) * mm});
            skLineSegment(sketch, "E766", {"start": v(-40.6, 1272.4) * mm, "end": v(-18.43, 1273.32) * mm});
            skLineSegment(sketch, "E767", {"start": v(-18.43, 1273.32) * mm, "end": v(3.7, 1273.2) * mm});
            skLineSegment(sketch, "E768", {"start": v(3.7, 1273.2) * mm, "end": v(25.73, 1272.05) * mm});
            skLineSegment(sketch, "E769", {"start": v(25.73, 1272.05) * mm, "end": v(47.64, 1269.9) * mm});
            skLineSegment(sketch, "E770", {"start": v(47.64, 1269.9) * mm, "end": v(69.39, 1266.74) * mm});
            skLineSegment(sketch, "E771", {"start": v(69.39, 1266.74) * mm, "end": v(90.94, 1262.62) * mm});
            skLineSegment(sketch, "E772", {"start": v(90.94, 1262.62) * mm, "end": v(112.26, 1257.53) * mm});
            skLineSegment(sketch, "E773", {"start": v(112.26, 1257.53) * mm, "end": v(133.32, 1251.5) * mm});
            skLineSegment(sketch, "E774", {"start": v(133.32, 1251.5) * mm, "end": v(154.08, 1244.54) * mm});
            skLineSegment(sketch, "E775", {"start": v(154.08, 1244.54) * mm, "end": v(174.5, 1236.68) * mm});
            skLineSegment(sketch, "E776", {"start": v(174.5, 1236.68) * mm, "end": v(194.56, 1227.92) * mm});
            skLineSegment(sketch, "E777", {"start": v(194.56, 1227.92) * mm, "end": v(214.21, 1218.3) * mm});
            skLineSegment(sketch, "E778", {"start": v(214.21, 1218.3) * mm, "end": v(233.42, 1207.81) * mm});
            skLineSegment(sketch, "E779", {"start": v(233.42, 1207.81) * mm, "end": v(252.16, 1196.5) * mm});
            skLineSegment(sketch, "E780", {"start": v(252.16, 1196.5) * mm, "end": v(270.38, 1184.35) * mm});
            skLineSegment(sketch, "E781", {"start": v(270.38, 1184.35) * mm, "end": v(288.06, 1171.4) * mm});
            skLineSegment(sketch, "E782", {"start": v(288.06, 1171.4) * mm, "end": v(305.16, 1157.66) * mm});
            skLineSegment(sketch, "E783", {"start": v(305.16, 1157.66) * mm, "end": v(321.65, 1143.15) * mm});
            skLineSegment(sketch, "E784", {"start": v(321.65, 1143.15) * mm, "end": v(337.48, 1127.89) * mm});
            skLineSegment(sketch, "E785", {"start": v(337.48, 1127.89) * mm, "end": v(352.64, 1111.9) * mm});
            skLineSegment(sketch, "E786", {"start": v(352.64, 1111.9) * mm, "end": v(367.07, 1095.18) * mm});
            skLineSegment(sketch, "E787", {"start": v(367.07, 1095.18) * mm, "end": v(380.75, 1077.76) * mm});
            skLineSegment(sketch, "E788", {"start": v(380.75, 1077.76) * mm, "end": v(393.63, 1059.66) * mm});
            skLineSegment(sketch, "E789", {"start": v(393.63, 1059.66) * mm, "end": v(405.7, 1040.89) * mm});
            skLineSegment(sketch, "E790", {"start": v(405.7, 1040.89) * mm, "end": v(416.9, 1021.47) * mm});
            skLineSegment(sketch, "E791", {"start": v(416.9, 1021.47) * mm, "end": v(427.21, 1001.41) * mm});
            skLineSegment(sketch, "E792", {"start": v(427.21, 1001.41) * mm, "end": v(436.59, 980.74) * mm});
            skLineSegment(sketch, "E793", {"start": v(436.59, 980.74) * mm, "end": v(445, 959.47) * mm});
            skLineSegment(sketch, "E794", {"start": v(445, 959.47) * mm, "end": v(452.42, 937.62) * mm});
            skLineSegment(sketch, "E795", {"start": v(452.42, 937.62) * mm, "end": v(458.8, 915.21) * mm});
            skLineSegment(sketch, "E796", {"start": v(458.8, 915.21) * mm, "end": v(464.63, 890.5) * mm});
            skLineSegment(sketch, "E797", {"start": v(464.63, 890.5) * mm, "end": v(469.46, 865.6) * mm});
            skLineSegment(sketch, "E798", {"start": v(469.46, 865.6) * mm, "end": v(473.36, 840.57) * mm});
            skLineSegment(sketch, "E799", {"start": v(473.36, 840.57) * mm, "end": v(476.38, 815.4) * mm});
            skLineSegment(sketch, "E800", {"start": v(476.38, 815.4) * mm, "end": v(478.6, 790.12) * mm});
            skLineSegment(sketch, "E801", {"start": v(478.6, 790.12) * mm, "end": v(480.06, 764.72) * mm});
            skLineSegment(sketch, "E802", {"start": v(480.06, 764.72) * mm, "end": v(480.84, 739.23) * mm});
            skLineSegment(sketch, "E803", {"start": v(480.84, 739.23) * mm, "end": v(481, 713.67) * mm});
            skLineSegment(sketch, "E804", {"start": v(481, 713.67) * mm, "end": v(480.6, 688.04) * mm});
            skLineSegment(sketch, "E805", {"start": v(480.6, 688.04) * mm, "end": v(479.7, 662.35) * mm});
            skLineSegment(sketch, "E806", {"start": v(479.7, 662.35) * mm, "end": v(478.36, 636.64) * mm});
            skLineSegment(sketch, "E807", {"start": v(478.36, 636.64) * mm, "end": v(476.65, 610.9) * mm});
            skLineSegment(sketch, "E808", {"start": v(476.65, 610.9) * mm, "end": v(474.63, 585.16) * mm});
            skLineSegment(sketch, "E809", {"start": v(474.63, 585.16) * mm, "end": v(472.36, 559.42) * mm});
            skLineSegment(sketch, "E810", {"start": v(472.36, 559.42) * mm, "end": v(469.92, 533.7) * mm});
            skLineSegment(sketch, "E811", {"start": v(469.92, 533.7) * mm, "end": v(467.34, 508.03) * mm});
            skLineSegment(sketch, "E812", {"start": v(467.34, 508.03) * mm, "end": v(464.71, 482.4) * mm});
            skLineSegment(sketch, "E813", {"start": v(464.71, 482.4) * mm, "end": v(462.08, 456.83) * mm});
            skLineSegment(sketch, "E814", {"start": v(462.08, 456.83) * mm, "end": v(459.52, 431.35) * mm});
            skLineSegment(sketch, "E815", {"start": v(459.52, 431.35) * mm, "end": v(457.08, 405.96) * mm});
            skLineSegment(sketch, "E816", {"start": v(457.08, 405.96) * mm, "end": v(454.84, 380.67) * mm});
            skLineSegment(sketch, "E817", {"start": v(454.84, 380.67) * mm, "end": v(452.85, 355.51) * mm});
            skLineSegment(sketch, "E818", {"start": v(452.85, 355.51) * mm, "end": v(451.18, 330.48) * mm});
            skLineSegment(sketch, "E819", {"start": v(451.18, 330.48) * mm, "end": v(449.88, 305.61) * mm});
            skLineSegment(sketch, "E820", {"start": v(449.88, 305.61) * mm, "end": v(448.83, 280.3) * mm});
            skLineSegment(sketch, "E821", {"start": v(448.83, 280.3) * mm, "end": v(447.9, 254.97) * mm});
            skLineSegment(sketch, "E822", {"start": v(447.9, 254.97) * mm, "end": v(447.07, 229.64) * mm});
            skLineSegment(sketch, "E823", {"start": v(447.07, 229.64) * mm, "end": v(446.34, 204.29) * mm});
            skLineSegment(sketch, "E824", {"start": v(446.34, 204.29) * mm, "end": v(445.72, 178.93) * mm});
            skLineSegment(sketch, "E825", {"start": v(445.72, 178.93) * mm, "end": v(445.19, 153.55) * mm});
            skLineSegment(sketch, "E826", {"start": v(445.19, 153.55) * mm, "end": v(444.75, 128.17) * mm});
            skLineSegment(sketch, "E827", {"start": v(444.75, 128.17) * mm, "end": v(444.4, 102.78) * mm});
            skLineSegment(sketch, "E828", {"start": v(444.4, 102.78) * mm, "end": v(444.11, 77.38) * mm});
            skLineSegment(sketch, "E829", {"start": v(444.11, 77.38) * mm, "end": v(443.91, 51.97) * mm});
            skLineSegment(sketch, "E830", {"start": v(443.91, 51.97) * mm, "end": v(443.78, 26.56) * mm});
            skLineSegment(sketch, "E831", {"start": v(443.78, 26.56) * mm, "end": v(443.71, 1.14) * mm});
            skLineSegment(sketch, "E832", {"start": v(443.71, 1.14) * mm, "end": v(443.7, -24.3) * mm});
            skLineSegment(sketch, "E833", {"start": v(443.7, -24.3) * mm, "end": v(443.75, -49.72) * mm});
            skLineSegment(sketch, "E834", {"start": v(443.75, -49.72) * mm, "end": v(443.85, -75.16) * mm});
            skLineSegment(sketch, "E835", {"start": v(443.85, -75.16) * mm, "end": v(443.99, -100.6) * mm});
            skLineSegment(sketch, "E836", {"start": v(443.99, -100.6) * mm, "end": v(444.17, -126.03) * mm});
            skLineSegment(sketch, "E837", {"start": v(444.17, -126.03) * mm, "end": v(444.4, -151.48) * mm});
            skLineSegment(sketch, "E838", {"start": v(444.4, -151.48) * mm, "end": v(444.64, -176.92) * mm});
            skLineSegment(sketch, "E839", {"start": v(444.64, -176.92) * mm, "end": v(444.92, -202.36) * mm});
            skLineSegment(sketch, "E840", {"start": v(444.92, -202.36) * mm, "end": v(445.22, -227.8) * mm});
            skLineSegment(sketch, "E841", {"start": v(445.22, -227.8) * mm, "end": v(445.53, -253.24) * mm});
            skLineSegment(sketch, "E842", {"start": v(445.53, -253.24) * mm, "end": v(445.85, -278.68) * mm});
            skLineSegment(sketch, "E843", {"start": v(445.85, -278.68) * mm, "end": v(446.18, -304.11) * mm});
            skLineSegment(sketch, "E844", {"start": v(446.18, -304.11) * mm, "end": v(446.52, -329.54) * mm});
            skLineSegment(sketch, "E845", {"start": v(446.52, -329.54) * mm, "end": v(446.84, -354.97) * mm});
            skLineSegment(sketch, "E846", {"start": v(446.84, -354.97) * mm, "end": v(447.17, -380.39) * mm});
            skLineSegment(sketch, "E847", {"start": v(447.17, -380.39) * mm, "end": v(447.47, -405.8) * mm});
            skLineSegment(sketch, "E848", {"start": v(447.47, -405.8) * mm, "end": v(447.76, -431.2) * mm});
            skLineSegment(sketch, "E849", {"start": v(447.76, -431.2) * mm, "end": v(448.03, -456.6) * mm});
            skLineSegment(sketch, "E850", {"start": v(448.03, -456.6) * mm, "end": v(448.27, -482) * mm});
            skLineSegment(sketch, "E851", {"start": v(448.27, -482) * mm, "end": v(448.48, -507.38) * mm});
            skLineSegment(sketch, "E852", {"start": v(448.48, -507.38) * mm, "end": v(448.65, -532.75) * mm});
            skLineSegment(sketch, "E853", {"start": v(448.65, -532.75) * mm, "end": v(448.77, -558.1) * mm});
            skLineSegment(sketch, "E854", {"start": v(448.77, -558.1) * mm, "end": v(448.85, -583.46) * mm});
            skLineSegment(sketch, "E855", {"start": v(448.85, -583.46) * mm, "end": v(448.88, -608.79) * mm});
            skLineSegment(sketch, "E856", {"start": v(448.88, -608.79) * mm, "end": v(421.1, -613.83) * mm});
            skLineSegment(sketch, "E857", {"start": v(421.1, -613.83) * mm, "end": v(394.92, -620) * mm});
            skLineSegment(sketch, "E858", {"start": v(394.92, -620) * mm, "end": v(370.29, -627.26) * mm});
            skLineSegment(sketch, "E859", {"start": v(370.29, -627.26) * mm, "end": v(347.16, -635.58) * mm});
            skLineSegment(sketch, "E860", {"start": v(347.16, -635.58) * mm, "end": v(325.49, -644.92) * mm});
            skLineSegment(sketch, "E861", {"start": v(325.49, -644.92) * mm, "end": v(305.22, -655.25) * mm});
            skLineSegment(sketch, "E862", {"start": v(305.22, -655.25) * mm, "end": v(286.32, -666.53) * mm});
            skLineSegment(sketch, "E863", {"start": v(286.32, -666.53) * mm, "end": v(268.73, -678.72) * mm});
            skLineSegment(sketch, "E864", {"start": v(268.73, -678.72) * mm, "end": v(252.4, -691.8) * mm});
            skLineSegment(sketch, "E865", {"start": v(252.4, -691.8) * mm, "end": v(237.3, -705.7) * mm});
            skLineSegment(sketch, "E866", {"start": v(237.3, -705.7) * mm, "end": v(223.38, -720.43) * mm});
            skLineSegment(sketch, "E867", {"start": v(223.38, -720.43) * mm, "end": v(210.57, -735.92) * mm});
            skLineSegment(sketch, "E868", {"start": v(210.57, -735.92) * mm, "end": v(198.85, -752.15) * mm});
            skLineSegment(sketch, "E869", {"start": v(198.85, -752.15) * mm, "end": v(188.15, -769.08) * mm});
            skLineSegment(sketch, "E870", {"start": v(188.15, -769.08) * mm, "end": v(178.45, -786.67) * mm});
            skLineSegment(sketch, "E871", {"start": v(178.45, -786.67) * mm, "end": v(169.67, -804.89) * mm});
            skLineSegment(sketch, "E872", {"start": v(169.67, -804.89) * mm, "end": v(161.8, -823.7) * mm});
            skLineSegment(sketch, "E873", {"start": v(161.8, -823.7) * mm, "end": v(154.76, -843.07) * mm});
            skLineSegment(sketch, "E874", {"start": v(154.76, -843.07) * mm, "end": v(148.52, -862.95) * mm});
            skLineSegment(sketch, "E875", {"start": v(148.52, -862.95) * mm, "end": v(143.03, -883.33) * mm});
            skLineSegment(sketch, "E876", {"start": v(143.03, -883.33) * mm, "end": v(138.24, -904.15) * mm});
            skLineSegment(sketch, "E877", {"start": v(138.24, -904.15) * mm, "end": v(134.1, -925.39) * mm});
            skLineSegment(sketch, "E878", {"start": v(134.1, -925.39) * mm, "end": v(130.58, -947) * mm});
            skLineSegment(sketch, "E879", {"start": v(130.58, -947) * mm, "end": v(127.61, -968.96) * mm});
            skLineSegment(sketch, "E880", {"start": v(127.61, -968.96) * mm, "end": v(125.16, -991.22) * mm});
            skLineSegment(sketch, "E881", {"start": v(125.16, -991.22) * mm, "end": v(123.18, -1013.75) * mm});
            skLineSegment(sketch, "E882", {"start": v(123.18, -1013.75) * mm, "end": v(121.61, -1036.52) * mm});
            skLineSegment(sketch, "E883", {"start": v(121.61, -1036.52) * mm, "end": v(120.42, -1059.48) * mm});
            skLineSegment(sketch, "E884", {"start": v(120.42, -1059.48) * mm, "end": v(119.55, -1082.6) * mm});
            skLineSegment(sketch, "E885", {"start": v(119.55, -1082.6) * mm, "end": v(118.96, -1105.86) * mm});
            skLineSegment(sketch, "E886", {"start": v(118.96, -1105.86) * mm, "end": v(118.6, -1129.2) * mm});
            skLineSegment(sketch, "E887", {"start": v(118.6, -1129.2) * mm, "end": v(118.43, -1152.6) * mm});
            skLineSegment(sketch, "E888", {"start": v(118.43, -1152.6) * mm, "end": v(118.4, -1176.03) * mm});
            skLineSegment(sketch, "E889", {"start": v(118.4, -1176.03) * mm, "end": v(118.45, -1199.43) * mm});
            skLineSegment(sketch, "E890", {"start": v(118.45, -1199.43) * mm, "end": v(118.55, -1222.79) * mm});
            skLineSegment(sketch, "E891", {"start": v(118.55, -1222.79) * mm, "end": v(118.64, -1246.05) * mm});
            skLineSegment(sketch, "E892", {"start": v(118.64, -1246.05) * mm, "end": v(118.68, -1269.19) * mm});
            skLineSegment(sketch, "E893", {"start": v(118.68, -1269.19) * mm, "end": v(118.68, -3224.99) * mm});
            skLineSegment(sketch, "E894", {"start": v(118.68, -3224.99) * mm, "end": v(118.71, -3241.8) * mm});
            skLineSegment(sketch, "E895", {"start": v(118.71, -3241.8) * mm, "end": v(118.84, -3259.4) * mm});
            skLineSegment(sketch, "E896", {"start": v(118.84, -3259.4) * mm, "end": v(119.1, -3277.71) * mm});
            skLineSegment(sketch, "E897", {"start": v(119.1, -3277.71) * mm, "end": v(119.5, -3296.65) * mm});
            skLineSegment(sketch, "E898", {"start": v(119.5, -3296.65) * mm, "end": v(120.09, -3316.14) * mm});
            skLineSegment(sketch, "E899", {"start": v(120.09, -3316.14) * mm, "end": v(120.9, -3336.11) * mm});
            skLineSegment(sketch, "E900", {"start": v(120.9, -3336.11) * mm, "end": v(121.95, -3356.49) * mm});
            skLineSegment(sketch, "E901", {"start": v(121.95, -3356.49) * mm, "end": v(123.28, -3377.19) * mm});
            skLineSegment(sketch, "E902", {"start": v(123.28, -3377.19) * mm, "end": v(124.92, -3398.14) * mm});
            skLineSegment(sketch, "E903", {"start": v(124.92, -3398.14) * mm, "end": v(126.91, -3419.27) * mm});
            skLineSegment(sketch, "E904", {"start": v(126.91, -3419.27) * mm, "end": v(129.27, -3440.5) * mm});
            skLineSegment(sketch, "E905", {"start": v(129.27, -3440.5) * mm, "end": v(132.04, -3461.75) * mm});
            skLineSegment(sketch, "E906", {"start": v(132.04, -3461.75) * mm, "end": v(135.24, -3482.95) * mm});
            skLineSegment(sketch, "E907", {"start": v(135.24, -3482.95) * mm, "end": v(138.91, -3504.02) * mm});
            skLineSegment(sketch, "E908", {"start": v(138.91, -3504.02) * mm, "end": v(143.08, -3524.9) * mm});
            skLineSegment(sketch, "E909", {"start": v(143.08, -3524.9) * mm, "end": v(147.78, -3545.48) * mm});
            skLineSegment(sketch, "E910", {"start": v(147.78, -3545.48) * mm, "end": v(153.04, -3565.71) * mm});
            skLineSegment(sketch, "E911", {"start": v(153.04, -3565.71) * mm, "end": v(158.9, -3585.5) * mm});
            skLineSegment(sketch, "E912", {"start": v(158.9, -3585.5) * mm, "end": v(165.37, -3604.8) * mm});
            skLineSegment(sketch, "E913", {"start": v(165.37, -3604.8) * mm, "end": v(172.5, -3623.51) * mm});
            skLineSegment(sketch, "E914", {"start": v(172.5, -3623.51) * mm, "end": v(180.32, -3641.56) * mm});
            skLineSegment(sketch, "E915", {"start": v(180.32, -3641.56) * mm, "end": v(188.86, -3658.87) * mm});
            skLineSegment(sketch, "E916", {"start": v(188.86, -3658.87) * mm, "end": v(198.15, -3675.37) * mm});
            skLineSegment(sketch, "E917", {"start": v(198.15, -3675.37) * mm, "end": v(208.22, -3691) * mm});
            skLineSegment(sketch, "E918", {"start": v(208.22, -3691) * mm, "end": v(219.1, -3705.64) * mm});
            skLineSegment(sketch, "E919", {"start": v(219.1, -3705.64) * mm, "end": v(230.83, -3719.25) * mm});
            skLineSegment(sketch, "E920", {"start": v(230.83, -3719.25) * mm, "end": v(243.43, -3731.75) * mm});
            skLineSegment(sketch, "E921", {"start": v(243.43, -3731.75) * mm, "end": v(256.93, -3743.06) * mm});
            skLineSegment(sketch, "E922", {"start": v(256.93, -3743.06) * mm, "end": v(271.38, -3753.1) * mm});
            skLineSegment(sketch, "E923", {"start": v(271.38, -3753.1) * mm, "end": v(286.79, -3761.8) * mm});
            skLineSegment(sketch, "E924", {"start": v(286.79, -3761.8) * mm, "end": v(303.2, -3769.07) * mm});
            skLineSegment(sketch, "E925", {"start": v(303.2, -3769.07) * mm, "end": v(320.65, -3774.86) * mm});
            skLineSegment(sketch, "E926", {"start": v(320.65, -3774.86) * mm, "end": v(339.16, -3779.07) * mm});
            skLineSegment(sketch, "E927", {"start": v(339.16, -3779.07) * mm, "end": v(358.76, -3781.64) * mm});
            skLineSegment(sketch, "E928", {"start": v(358.76, -3781.64) * mm, "end": v(379.49, -3782.48) * mm});
            skLineSegment(sketch, "E929", {"start": v(379.49, -3782.48) * mm, "end": v(401.37, -3781.52) * mm});
            skLineSegment(sketch, "E930", {"start": v(401.37, -3781.52) * mm, "end": v(424.44, -3778.7) * mm});
            skLineSegment(sketch, "E931", {"start": v(424.44, -3778.7) * mm, "end": v(448.74, -3773.92) * mm});
            skLineSegment(sketch, "E932", {"start": v(448.74, -3773.92) * mm, "end": v(474.28, -3767.11) * mm});
            skLineSegment(sketch, "E933", {"start": v(474.28, -3767.11) * mm, "end": v(497.02, -3759.49) * mm});
            skLineSegment(sketch, "E934", {"start": v(497.02, -3759.49) * mm, "end": v(519.3, -3750.43) * mm});
            skLineSegment(sketch, "E935", {"start": v(519.3, -3750.43) * mm, "end": v(541.15, -3740.03) * mm});
            skLineSegment(sketch, "E936", {"start": v(541.15, -3740.03) * mm, "end": v(562.57, -3728.38) * mm});
            skLineSegment(sketch, "E937", {"start": v(562.57, -3728.38) * mm, "end": v(583.58, -3715.56) * mm});
            skLineSegment(sketch, "E938", {"start": v(583.58, -3715.56) * mm, "end": v(604.19, -3701.66) * mm});
            skLineSegment(sketch, "E939", {"start": v(604.19, -3701.66) * mm, "end": v(624.4, -3686.78) * mm});
            skLineSegment(sketch, "E940", {"start": v(624.4, -3686.78) * mm, "end": v(644.25, -3671) * mm});
            skLineSegment(sketch, "E941", {"start": v(644.25, -3671) * mm, "end": v(663.72, -3654.43) * mm});
            skLineSegment(sketch, "E942", {"start": v(663.72, -3654.43) * mm, "end": v(682.84, -3637.12) * mm});
            skLineSegment(sketch, "E943", {"start": v(682.84, -3637.12) * mm, "end": v(701.63, -3619.2) * mm});
            skLineSegment(sketch, "E944", {"start": v(701.63, -3619.2) * mm, "end": v(720.08, -3600.72) * mm});
            skLineSegment(sketch, "E945", {"start": v(720.08, -3600.72) * mm, "end": v(738.22, -3581.8) * mm});
            skLineSegment(sketch, "E946", {"start": v(738.22, -3581.8) * mm, "end": v(756.05, -3562.5) * mm});
            skLineSegment(sketch, "E947", {"start": v(756.05, -3562.5) * mm, "end": v(773.6, -3542.95) * mm});
            skLineSegment(sketch, "E948", {"start": v(773.6, -3542.95) * mm, "end": v(790.86, -3523.2) * mm});
            skLineSegment(sketch, "E949", {"start": v(790.86, -3523.2) * mm, "end": v(807.86, -3503.37) * mm});
            skLineSegment(sketch, "E950", {"start": v(807.86, -3503.37) * mm, "end": v(824.6, -3483.53) * mm});
            skLineSegment(sketch, "E951", {"start": v(824.6, -3483.53) * mm, "end": v(841.1, -3463.78) * mm});
            skLineSegment(sketch, "E952", {"start": v(841.1, -3463.78) * mm, "end": v(857.37, -3444.2) * mm});
            skLineSegment(sketch, "E953", {"start": v(857.37, -3444.2) * mm, "end": v(873.42, -3424.87) * mm});
            skLineSegment(sketch, "E954", {"start": v(873.42, -3424.87) * mm, "end": v(889.27, -3405.9) * mm});
            skLineSegment(sketch, "E955", {"start": v(889.27, -3405.9) * mm, "end": v(904.92, -3387.37) * mm});
            skLineSegment(sketch, "E956", {"start": v(904.92, -3387.37) * mm, "end": v(920.4, -3369.37) * mm});
            skLineSegment(sketch, "E957", {"start": v(920.4, -3369.37) * mm, "end": v(935.7, -3351.99) * mm});
            skLineSegment(sketch, "E958", {"start": v(935.7, -3351.99) * mm, "end": v(952.75, -3332.94) * mm});
            skLineSegment(sketch, "E959", {"start": v(952.75, -3332.94) * mm, "end": v(969.85, -3313.93) * mm});
            skLineSegment(sketch, "E960", {"start": v(969.85, -3313.93) * mm, "end": v(986.99, -3294.96) * mm});
            skLineSegment(sketch, "E961", {"start": v(986.99, -3294.96) * mm, "end": v(1004.17, -3276.02) * mm});
            skLineSegment(sketch, "E962", {"start": v(1004.17, -3276.02) * mm, "end": v(1021.39, -3257.12) * mm});
            skLineSegment(sketch, "E963", {"start": v(1021.39, -3257.12) * mm, "end": v(1038.64, -3238.24) * mm});
            skLineSegment(sketch, "E964", {"start": v(1038.64, -3238.24) * mm, "end": v(1055.93, -3219.4) * mm});
            skLineSegment(sketch, "E965", {"start": v(1055.93, -3219.4) * mm, "end": v(1073.25, -3200.59) * mm});
            skLineSegment(sketch, "E966", {"start": v(1073.25, -3200.59) * mm, "end": v(1090.6, -3181.8) * mm});
            skLineSegment(sketch, "E967", {"start": v(1090.6, -3181.8) * mm, "end": v(1107.97, -3163.04) * mm});
            skLineSegment(sketch, "E968", {"start": v(1107.97, -3163.04) * mm, "end": v(1125.37, -3144.3) * mm});
            skLineSegment(sketch, "E969", {"start": v(1125.37, -3144.3) * mm, "end": v(1142.8, -3125.58) * mm});
            skLineSegment(sketch, "E970", {"start": v(1142.8, -3125.58) * mm, "end": v(1160.24, -3106.88) * mm});
            skLineSegment(sketch, "E971", {"start": v(1160.24, -3106.88) * mm, "end": v(1177.7, -3088.2) * mm});
            skLineSegment(sketch, "E972", {"start": v(1177.7, -3088.2) * mm, "end": v(1195.18, -3069.53) * mm});
            skLineSegment(sketch, "E973", {"start": v(1195.18, -3069.53) * mm, "end": v(1212.68, -3050.88) * mm});
            skLineSegment(sketch, "E974", {"start": v(1212.68, -3050.88) * mm, "end": v(1230.2, -3032.24) * mm});
            skLineSegment(sketch, "E975", {"start": v(1230.2, -3032.24) * mm, "end": v(1247.71, -3013.61) * mm});
            skLineSegment(sketch, "E976", {"start": v(1247.71, -3013.61) * mm, "end": v(1265.24, -2995) * mm});
            skLineSegment(sketch, "E977", {"start": v(1265.24, -2995) * mm, "end": v(1282.78, -2976.38) * mm});
            skLineSegment(sketch, "E978", {"start": v(1282.78, -2976.38) * mm, "end": v(1300.32, -2957.77) * mm});
            skLineSegment(sketch, "E979", {"start": v(1300.32, -2957.77) * mm, "end": v(1317.87, -2939.16) * mm});
            skLineSegment(sketch, "E980", {"start": v(1317.87, -2939.16) * mm, "end": v(1335.42, -2920.56) * mm});
            skLineSegment(sketch, "E981", {"start": v(1335.42, -2920.56) * mm, "end": v(1352.96, -2901.95) * mm});
            skLineSegment(sketch, "E982", {"start": v(1352.96, -2901.95) * mm, "end": v(1370.5, -2883.35) * mm});
            skLineSegment(sketch, "E983", {"start": v(1370.5, -2883.35) * mm, "end": v(1388.04, -2864.74) * mm});
            skLineSegment(sketch, "E984", {"start": v(1388.04, -2864.74) * mm, "end": v(1405.57, -2846.12) * mm});
            skLineSegment(sketch, "E985", {"start": v(1405.57, -2846.12) * mm, "end": v(1423.1, -2827.5) * mm});
            skLineSegment(sketch, "E986", {"start": v(1423.1, -2827.5) * mm, "end": v(1440.6, -2808.86) * mm});
            skLineSegment(sketch, "E987", {"start": v(1440.6, -2808.86) * mm, "end": v(1458.1, -2790.22) * mm});
            skLineSegment(sketch, "E988", {"start": v(1458.1, -2790.22) * mm, "end": v(1475.59, -2771.56) * mm});
            skLineSegment(sketch, "E989", {"start": v(1475.59, -2771.56) * mm, "end": v(1493.06, -2752.88) * mm});
            skLineSegment(sketch, "E990", {"start": v(1493.06, -2752.88) * mm, "end": v(1510.5, -2734.2) * mm});
            skLineSegment(sketch, "E991", {"start": v(1510.5, -2734.2) * mm, "end": v(1527.93, -2715.49) * mm});
            skLineSegment(sketch, "E992", {"start": v(1527.93, -2715.49) * mm, "end": v(1545.33, -2696.76) * mm});
            skLineSegment(sketch, "E993", {"start": v(1545.33, -2696.76) * mm, "end": v(1562.7, -2678) * mm});
            skLineSegment(sketch, "E994", {"start": v(1562.7, -2678) * mm, "end": v(1580.06, -2659.23) * mm});
            skLineSegment(sketch, "E995", {"start": v(1580.06, -2659.23) * mm, "end": v(1597.38, -2640.43) * mm});
            skLineSegment(sketch, "E996", {"start": v(1597.38, -2640.43) * mm, "end": v(1614.67, -2621.6) * mm});
            skLineSegment(sketch, "E997", {"start": v(1614.67, -2621.6) * mm, "end": v(1631.93, -2602.75) * mm});
            skLineSegment(sketch, "E998", {"start": v(1631.93, -2602.75) * mm, "end": v(1649.15, -2583.86) * mm});
            skLineSegment(sketch, "E999", {"start": v(1649.15, -2583.86) * mm, "end": v(1666.34, -2564.94) * mm});
            skLineSegment(sketch, "E1000", {"start": v(1666.34, -2564.94) * mm, "end": v(1683.48, -2545.99) * mm});
            skLineSegment(sketch, "E1001", {"start": v(1683.48, -2545.99) * mm, "end": v(1700.59, -2527) * mm});
            skLineSegment(sketch, "E1002", {"start": v(1700.59, -2527) * mm, "end": v(1717.65, -2507.97) * mm});
            skLineSegment(sketch, "E1003", {"start": v(1717.65, -2507.97) * mm, "end": v(1734.66, -2488.9) * mm});
            skLineSegment(sketch, "E1004", {"start": v(1734.66, -2488.9) * mm, "end": v(1751.63, -2469.8) * mm});
            skLineSegment(sketch, "E1005", {"start": v(1751.63, -2469.8) * mm, "end": v(1768.55, -2450.64) * mm});
            skLineSegment(sketch, "E1006", {"start": v(1768.55, -2450.64) * mm, "end": v(1785.42, -2431.44) * mm});
            skLineSegment(sketch, "E1007", {"start": v(1785.42, -2431.44) * mm, "end": v(1802.23, -2412.19) * mm});
            skLineSegment(sketch, "E1008", {"start": v(1802.23, -2412.19) * mm, "end": v(1819.08, -2392.88) * mm});
            skLineSegment(sketch, "E1009", {"start": v(1819.08, -2392.88) * mm, "end": v(1835.96, -2373.6) * mm});
            skLineSegment(sketch, "E1010", {"start": v(1835.96, -2373.6) * mm, "end": v(1852.88, -2354.33) * mm});
            skLineSegment(sketch, "E1011", {"start": v(1852.88, -2354.33) * mm, "end": v(1869.83, -2335.1) * mm});
            skLineSegment(sketch, "E1012", {"start": v(1869.83, -2335.1) * mm, "end": v(1886.8, -2315.87) * mm});
            skLineSegment(sketch, "E1013", {"start": v(1886.8, -2315.87) * mm, "end": v(1903.81, -2296.68) * mm});
            skLineSegment(sketch, "E1014", {"start": v(1903.81, -2296.68) * mm, "end": v(1920.85, -2277.5) * mm});
            skLineSegment(sketch, "E1015", {"start": v(1920.85, -2277.5) * mm, "end": v(1937.92, -2258.34) * mm});
            skLineSegment(sketch, "E1016", {"start": v(1937.92, -2258.34) * mm, "end": v(1955.02, -2239.2) * mm});
            skLineSegment(sketch, "E1017", {"start": v(1955.02, -2239.2) * mm, "end": v(1972.14, -2220.09) * mm});
            skLineSegment(sketch, "E1018", {"start": v(1972.14, -2220.09) * mm, "end": v(1989.28, -2201) * mm});
            skLineSegment(sketch, "E1019", {"start": v(1989.28, -2201) * mm, "end": v(2006.46, -2181.91) * mm});
            skLineSegment(sketch, "E1020", {"start": v(2006.46, -2181.91) * mm, "end": v(2023.66, -2162.85) * mm});
            skLineSegment(sketch, "E1021", {"start": v(2023.66, -2162.85) * mm, "end": v(2040.87, -2143.8) * mm});
            skLineSegment(sketch, "E1022", {"start": v(2040.87, -2143.8) * mm, "end": v(2058.12, -2124.78) * mm});
            skLineSegment(sketch, "E1023", {"start": v(2058.12, -2124.78) * mm, "end": v(2075.38, -2105.77) * mm});
            skLineSegment(sketch, "E1024", {"start": v(2075.38, -2105.77) * mm, "end": v(2092.67, -2086.78) * mm});
            skLineSegment(sketch, "E1025", {"start": v(2092.67, -2086.78) * mm, "end": v(2109.97, -2067.8) * mm});
            skLineSegment(sketch, "E1026", {"start": v(2109.97, -2067.8) * mm, "end": v(2127.3, -2048.84) * mm});
            skLineSegment(sketch, "E1027", {"start": v(2127.3, -2048.84) * mm, "end": v(2144.64, -2029.88) * mm});
            skLineSegment(sketch, "E1028", {"start": v(2144.64, -2029.88) * mm, "end": v(2162, -2010.95) * mm});
            skLineSegment(sketch, "E1029", {"start": v(2162, -2010.95) * mm, "end": v(2179.37, -1992.03) * mm});
            skLineSegment(sketch, "E1030", {"start": v(2179.37, -1992.03) * mm, "end": v(2196.76, -1973.12) * mm});
            skLineSegment(sketch, "E1031", {"start": v(2196.76, -1973.12) * mm, "end": v(2214.17, -1954.22) * mm});
            skLineSegment(sketch, "E1032", {"start": v(2214.17, -1954.22) * mm, "end": v(2231.59, -1935.34) * mm});
            skLineSegment(sketch, "E1033", {"start": v(2231.59, -1935.34) * mm, "end": v(2249.02, -1916.47) * mm});
            skLineSegment(sketch, "E1034", {"start": v(2249.02, -1916.47) * mm, "end": v(2266.46, -1897.6) * mm});
            skLineSegment(sketch, "E1035", {"start": v(2266.46, -1897.6) * mm, "end": v(2283.91, -1878.75) * mm});
            skLineSegment(sketch, "E1036", {"start": v(2283.91, -1878.75) * mm, "end": v(2301.38, -1859.91) * mm});
            skLineSegment(sketch, "E1037", {"start": v(2301.38, -1859.91) * mm, "end": v(2318.85, -1841.08) * mm});
            skLineSegment(sketch, "E1038", {"start": v(2318.85, -1841.08) * mm, "end": v(2336.33, -1822.26) * mm});
            skLineSegment(sketch, "E1039", {"start": v(2336.33, -1822.26) * mm, "end": v(2353.82, -1803.45) * mm});
            skLineSegment(sketch, "E1040", {"start": v(2353.82, -1803.45) * mm, "end": v(2371.32, -1784.64) * mm});
            skLineSegment(sketch, "E1041", {"start": v(2371.32, -1784.64) * mm, "end": v(2388.82, -1765.85) * mm});
            skLineSegment(sketch, "E1042", {"start": v(2388.82, -1765.85) * mm, "end": v(2406.32, -1747.06) * mm});
            skLineSegment(sketch, "E1043", {"start": v(2406.32, -1747.06) * mm, "end": v(2423.84, -1728.27) * mm});
            skLineSegment(sketch, "E1044", {"start": v(2423.84, -1728.27) * mm, "end": v(2441.35, -1709.5) * mm});
            skLineSegment(sketch, "E1045", {"start": v(2441.35, -1709.5) * mm, "end": v(2458.86, -1690.73) * mm});
            skLineSegment(sketch, "E1046", {"start": v(2458.86, -1690.73) * mm, "end": v(2476.38, -1671.96) * mm});
            skLineSegment(sketch, "E1047", {"start": v(2476.38, -1671.96) * mm, "end": v(2493.9, -1653.2) * mm});
            skLineSegment(sketch, "E1048", {"start": v(2493.9, -1653.2) * mm, "end": v(2511.41, -1634.44) * mm});
            skLineSegment(sketch, "E1049", {"start": v(2511.41, -1634.44) * mm, "end": v(2528.93, -1615.69) * mm});
            skLineSegment(sketch, "E1050", {"start": v(2528.93, -1615.69) * mm, "end": v(2546.44, -1596.94) * mm});
            skLineSegment(sketch, "E1051", {"start": v(2546.44, -1596.94) * mm, "end": v(2563.95, -1578.19) * mm});
            skLineSegment(sketch, "E1052", {"start": v(2563.95, -1578.19) * mm, "end": v(2581.46, -1559.44) * mm});
            skLineSegment(sketch, "E1053", {"start": v(2581.46, -1559.44) * mm, "end": v(2598.96, -1540.7) * mm});
            skLineSegment(sketch, "E1054", {"start": v(2598.96, -1540.7) * mm, "end": v(2616.45, -1521.96) * mm});
            skLineSegment(sketch, "E1055", {"start": v(2616.45, -1521.96) * mm, "end": v(2633.94, -1503.22) * mm});
            skLineSegment(sketch, "E1056", {"start": v(2633.94, -1503.22) * mm, "end": v(2651.42, -1484.48) * mm});
            skLineSegment(sketch, "E1057", {"start": v(2651.42, -1484.48) * mm, "end": v(2668.89, -1465.73) * mm});
            skLineSegment(sketch, "E1058", {"start": v(2668.89, -1465.73) * mm, "end": v(2686.35, -1446.99) * mm});
            skLineSegment(sketch, "E1059", {"start": v(2686.35, -1446.99) * mm, "end": v(2703.68, -1428.37) * mm});
            skLineSegment(sketch, "E1060", {"start": v(2703.68, -1428.37) * mm, "end": v(2720.97, -1409.73) * mm});
            skLineSegment(sketch, "E1061", {"start": v(2720.97, -1409.73) * mm, "end": v(2738.21, -1391.09) * mm});
            skLineSegment(sketch, "E1062", {"start": v(2738.21, -1391.09) * mm, "end": v(2755.4, -1372.43) * mm});
            skLineSegment(sketch, "E1063", {"start": v(2755.4, -1372.43) * mm, "end": v(2772.56, -1353.76) * mm});
            skLineSegment(sketch, "E1064", {"start": v(2772.56, -1353.76) * mm, "end": v(2789.65, -1335.06) * mm});
            skLineSegment(sketch, "E1065", {"start": v(2789.65, -1335.06) * mm, "end": v(2806.68, -1316.35) * mm});
            skLineSegment(sketch, "E1066", {"start": v(2806.68, -1316.35) * mm, "end": v(2823.65, -1297.6) * mm});
            skLineSegment(sketch, "E1067", {"start": v(2823.65, -1297.6) * mm, "end": v(2840.55, -1278.84) * mm});
            skLineSegment(sketch, "E1068", {"start": v(2840.55, -1278.84) * mm, "end": v(2857.38, -1260.04) * mm});
            skLineSegment(sketch, "E1069", {"start": v(2857.38, -1260.04) * mm, "end": v(2874.13, -1241.2) * mm});
            skLineSegment(sketch, "E1070", {"start": v(2874.13, -1241.2) * mm, "end": v(2890.8, -1222.34) * mm});
            skLineSegment(sketch, "E1071", {"start": v(2890.8, -1222.34) * mm, "end": v(2907.39, -1203.44) * mm});
            skLineSegment(sketch, "E1072", {"start": v(2907.39, -1203.44) * mm, "end": v(2923.89, -1184.5) * mm});
            skLineSegment(sketch, "E1073", {"start": v(2923.89, -1184.5) * mm, "end": v(2940.3, -1165.5) * mm});
            skLineSegment(sketch, "E1074", {"start": v(2940.3, -1165.5) * mm, "end": v(2956.6, -1146.47) * mm});
            skLineSegment(sketch, "E1075", {"start": v(2956.6, -1146.47) * mm, "end": v(2972.8, -1127.39) * mm});
            skLineSegment(sketch, "E1076", {"start": v(2972.8, -1127.39) * mm, "end": v(2988.9, -1108.25) * mm});
            skLineSegment(sketch, "E1077", {"start": v(2988.9, -1108.25) * mm, "end": v(3004.9, -1089.06) * mm});
            skLineSegment(sketch, "E1078", {"start": v(3004.9, -1089.06) * mm, "end": v(3020.78, -1069.81) * mm});
            skLineSegment(sketch, "E1079", {"start": v(3020.78, -1069.81) * mm, "end": v(3036.54, -1050.5) * mm});
            skLineSegment(sketch, "E1080", {"start": v(3036.54, -1050.5) * mm, "end": v(3052.18, -1031.14) * mm});
            skLineSegment(sketch, "E1081", {"start": v(3052.18, -1031.14) * mm, "end": v(3067.7, -1011.7) * mm});
            skLineSegment(sketch, "E1082", {"start": v(3067.7, -1011.7) * mm, "end": v(3083.08, -992.2) * mm});
            skLineSegment(sketch, "E1083", {"start": v(3083.08, -992.2) * mm, "end": v(3098.33, -972.63) * mm});
            skLineSegment(sketch, "E1084", {"start": v(3098.33, -972.63) * mm, "end": v(3113.44, -953) * mm});
            skLineSegment(sketch, "E1085", {"start": v(3113.44, -953) * mm, "end": v(3128.4, -933.27) * mm});
            skLineSegment(sketch, "E1086", {"start": v(3128.4, -933.27) * mm, "end": v(3143.23, -913.47) * mm});
            skLineSegment(sketch, "E1087", {"start": v(3143.23, -913.47) * mm, "end": v(3157.9, -893.59) * mm});
            skLineSegment(sketch, "E1088", {"start": v(3157.9, -893.59) * mm, "end": v(3172.41, -873.63) * mm});
            skLineSegment(sketch, "E1089", {"start": v(3172.41, -873.63) * mm, "end": v(3186.77, -853.57) * mm});
            skLineSegment(sketch, "E1090", {"start": v(3186.77, -853.57) * mm, "end": v(3200.96, -833.43) * mm});
            skLineSegment(sketch, "E1091", {"start": v(3200.96, -833.43) * mm, "end": v(3214.98, -813.2) * mm});
            skLineSegment(sketch, "E1092", {"start": v(3214.98, -813.2) * mm, "end": v(3228.84, -792.87) * mm});
            skLineSegment(sketch, "E1093", {"start": v(3228.84, -792.87) * mm, "end": v(3242.52, -772.45) * mm});
            skLineSegment(sketch, "E1094", {"start": v(3242.52, -772.45) * mm, "end": v(3256.01, -751.93) * mm});
            skLineSegment(sketch, "E1095", {"start": v(3256.01, -751.93) * mm, "end": v(3269.33, -731.3) * mm});
            skLineSegment(sketch, "E1096", {"start": v(3269.33, -731.3) * mm, "end": v(3282.45, -710.57) * mm});
            skLineSegment(sketch, "E1097", {"start": v(3282.45, -710.57) * mm, "end": v(3295.38, -689.73) * mm});
            skLineSegment(sketch, "E1098", {"start": v(3295.38, -689.73) * mm, "end": v(3308.12, -668.77) * mm});
            skLineSegment(sketch, "E1099", {"start": v(3308.12, -668.77) * mm, "end": v(3320.65, -647.71) * mm});
            skLineSegment(sketch, "E1100", {"start": v(3320.65, -647.71) * mm, "end": v(3332.98, -626.53) * mm});
            skLineSegment(sketch, "E1101", {"start": v(3332.98, -626.53) * mm, "end": v(3345.1, -605.23) * mm});
            skLineSegment(sketch, "E1102", {"start": v(3345.1, -605.23) * mm, "end": v(3357, -583.8) * mm});
            skLineSegment(sketch, "E1103", {"start": v(3357, -583.8) * mm, "end": v(3368.7, -562.26) * mm});
            skLineSegment(sketch, "E1104", {"start": v(3368.7, -562.26) * mm, "end": v(3380.16, -540.59) * mm});
            skLineSegment(sketch, "E1105", {"start": v(3380.16, -540.59) * mm, "end": v(3391.4, -518.78) * mm});
            skLineSegment(sketch, "E1106", {"start": v(3391.4, -518.78) * mm, "end": v(3402.42, -496.85) * mm});
            skLineSegment(sketch, "E1107", {"start": v(3402.42, -496.85) * mm, "end": v(3413.2, -474.78) * mm});
            skLineSegment(sketch, "E1108", {"start": v(3413.2, -474.78) * mm, "end": v(3423.74, -452.57) * mm});
            skLineSegment(sketch, "E1109", {"start": v(3423.74, -452.57) * mm, "end": v(3434.03, -430.23) * mm});
            skLineSegment(sketch, "E1110", {"start": v(3434.03, -430.23) * mm, "end": v(3444.09, -407.73) * mm});
            skLineSegment(sketch, "E1111", {"start": v(3444.09, -407.73) * mm, "end": v(3453.89, -385.1) * mm});
            skLineSegment(sketch, "E1112", {"start": v(3453.89, -385.1) * mm, "end": v(3463.43, -362.31) * mm});
            skLineSegment(sketch, "E1113", {"start": v(3463.43, -362.31) * mm, "end": v(3472.72, -339.37) * mm});
            skLineSegment(sketch, "E1114", {"start": v(3472.72, -339.37) * mm, "end": v(3481.74, -316.29) * mm});
            skLineSegment(sketch, "E1115", {"start": v(3481.74, -316.29) * mm, "end": v(3490.5, -293.04) * mm});
            skLineSegment(sketch, "E1116", {"start": v(3490.5, -293.04) * mm, "end": v(3498.98, -269.63) * mm});
            skLineSegment(sketch, "E1117", {"start": v(3498.98, -269.63) * mm, "end": v(3507.2, -246.06) * mm});
            skLineSegment(sketch, "E1118", {"start": v(3507.2, -246.06) * mm, "end": v(3515.12, -222.33) * mm});
            skLineSegment(sketch, "E1119", {"start": v(3515.12, -222.33) * mm, "end": v(3522.77, -198.43) * mm});
            skLineSegment(sketch, "E1120", {"start": v(3522.77, -198.43) * mm, "end": v(3530.13, -174.36) * mm});
            skLineSegment(sketch, "E1121", {"start": v(3530.13, -174.36) * mm, "end": v(3537.19, -150.12) * mm});
            skLineSegment(sketch, "E1122", {"start": v(3537.19, -150.12) * mm, "end": v(3543.96, -125.7) * mm});
            skLineSegment(sketch, "E1123", {"start": v(3543.96, -125.7) * mm, "end": v(3550.43, -101.1) * mm});
            skLineSegment(sketch, "E1124", {"start": v(3550.43, -101.1) * mm, "end": v(3556.6, -76.32) * mm});
            skLineSegment(sketch, "E1125", {"start": v(3556.6, -76.32) * mm, "end": v(3562.45, -51.36) * mm});
            skLineSegment(sketch, "E1126", {"start": v(3562.45, -51.36) * mm, "end": v(3567.99, -26.22) * mm});
            skLineSegment(sketch, "E1127", {"start": v(3567.99, -26.22) * mm, "end": v(3573.21, -0.88) * mm});
            skLineSegment(sketch, "E1128", {"start": v(3573.21, -0.88) * mm, "end": v(3578.12, 24.65) * mm});
            skLineSegment(sketch, "E1129", {"start": v(3578.12, 24.65) * mm, "end": v(3582.7, 50.37) * mm});
            skLineSegment(sketch, "E1130", {"start": v(3582.7, 50.37) * mm, "end": v(3586.94, 76.3) * mm});
            skLineSegment(sketch, "E1131", {"start": v(3586.94, 76.3) * mm, "end": v(3590.86, 102.41) * mm});
            skLineSegment(sketch, "E1132", {"start": v(3590.86, 102.41) * mm, "end": v(3594.16, 126.58) * mm});
            skLineSegment(sketch, "E1133", {"start": v(3594.16, 126.58) * mm, "end": v(3597.18, 150.84) * mm});
            skLineSegment(sketch, "E1134", {"start": v(3597.18, 150.84) * mm, "end": v(3599.92, 175.2) * mm});
            skLineSegment(sketch, "E1135", {"start": v(3599.92, 175.2) * mm, "end": v(3602.38, 199.64) * mm});
            skLineSegment(sketch, "E1136", {"start": v(3602.38, 199.64) * mm, "end": v(3604.56, 224.17) * mm});
            skLineSegment(sketch, "E1137", {"start": v(3604.56, 224.17) * mm, "end": v(3606.45, 248.78) * mm});
            skLineSegment(sketch, "E1138", {"start": v(3606.45, 248.78) * mm, "end": v(3608.07, 273.45) * mm});
            skLineSegment(sketch, "E1139", {"start": v(3608.07, 273.45) * mm, "end": v(3609.4, 298.2) * mm});
            skLineSegment(sketch, "E1140", {"start": v(3609.4, 298.2) * mm, "end": v(3610.46, 323) * mm});
            skLineSegment(sketch, "E1141", {"start": v(3610.46, 323) * mm, "end": v(3611.23, 347.87) * mm});
            skLineSegment(sketch, "E1142", {"start": v(3611.23, 347.87) * mm, "end": v(3611.73, 372.78) * mm});
            skLineSegment(sketch, "E1143", {"start": v(3611.73, 372.78) * mm, "end": v(3611.94, 397.75) * mm});
            skLineSegment(sketch, "E1144", {"start": v(3611.94, 397.75) * mm, "end": v(3611.88, 422.75) * mm});
            skLineSegment(sketch, "E1145", {"start": v(3611.88, 422.75) * mm, "end": v(3611.54, 447.8) * mm});
            skLineSegment(sketch, "E1146", {"start": v(3611.54, 447.8) * mm, "end": v(3610.92, 472.86) * mm});
            skLineSegment(sketch, "E1147", {"start": v(3610.92, 472.86) * mm, "end": v(3610.02, 497.96) * mm});
            skLineSegment(sketch, "E1148", {"start": v(3610.02, 497.96) * mm, "end": v(3608.85, 523.08) * mm});
            skLineSegment(sketch, "E1149", {"start": v(3608.85, 523.08) * mm, "end": v(3607.4, 548.22) * mm});
            skLineSegment(sketch, "E1150", {"start": v(3607.4, 548.22) * mm, "end": v(3605.66, 573.36) * mm});
            skLineSegment(sketch, "E1151", {"start": v(3605.66, 573.36) * mm, "end": v(3603.66, 598.51) * mm});
            skLineSegment(sketch, "E1152", {"start": v(3603.66, 598.51) * mm, "end": v(3601.38, 623.66) * mm});
            skLineSegment(sketch, "E1153", {"start": v(3601.38, 623.66) * mm, "end": v(3598.82, 648.81) * mm});
            skLineSegment(sketch, "E1154", {"start": v(3598.82, 648.81) * mm, "end": v(3595.99, 673.95) * mm});
            skLineSegment(sketch, "E1155", {"start": v(3595.99, 673.95) * mm, "end": v(3592.88, 699.07) * mm});
            skLineSegment(sketch, "E1156", {"start": v(3592.88, 699.07) * mm, "end": v(3589.5, 724.17) * mm});
            skLineSegment(sketch, "E1157", {"start": v(3589.5, 724.17) * mm, "end": v(3585.84, 749.25) * mm});
            skLineSegment(sketch, "E1158", {"start": v(3585.84, 749.25) * mm, "end": v(3581.9, 774.3) * mm});
            skLineSegment(sketch, "E1159", {"start": v(3581.9, 774.3) * mm, "end": v(3577.7, 799.31) * mm});
            skLineSegment(sketch, "E1160", {"start": v(3577.7, 799.31) * mm, "end": v(3573.22, 824.29) * mm});
            skLineSegment(sketch, "E1161", {"start": v(3573.22, 824.29) * mm, "end": v(3568.47, 849.21) * mm});
            skLineSegment(sketch, "E1162", {"start": v(3568.47, 849.21) * mm, "end": v(3563.44, 874.09) * mm});
            skLineSegment(sketch, "E1163", {"start": v(3563.44, 874.09) * mm, "end": v(3558.15, 898.9) * mm});
            skLineSegment(sketch, "E1164", {"start": v(3558.15, 898.9) * mm, "end": v(3552.58, 923.67) * mm});
            skLineSegment(sketch, "E1165", {"start": v(3552.58, 923.67) * mm, "end": v(3546.73, 948.36) * mm});
            skLineSegment(sketch, "E1166", {"start": v(3546.73, 948.36) * mm, "end": v(3540.62, 972.98) * mm});
            skLineSegment(sketch, "E1167", {"start": v(3540.62, 972.98) * mm, "end": v(3534.23, 997.52) * mm});
            skLineSegment(sketch, "E1168", {"start": v(3534.23, 997.52) * mm, "end": v(3527.58, 1021.99) * mm});
            skLineSegment(sketch, "E1169", {"start": v(3527.58, 1021.99) * mm, "end": v(3520.65, 1046.36) * mm});
            skLineSegment(sketch, "E1170", {"start": v(3520.65, 1046.36) * mm, "end": v(3513.45, 1070.65) * mm});
            skLineSegment(sketch, "E1171", {"start": v(3513.45, 1070.65) * mm, "end": v(3505.99, 1094.84) * mm});
            skLineSegment(sketch, "E1172", {"start": v(3505.99, 1094.84) * mm, "end": v(3498.25, 1118.92) * mm});
            skLineSegment(sketch, "E1173", {"start": v(3498.25, 1118.92) * mm, "end": v(3490.24, 1142.9) * mm});
            skLineSegment(sketch, "E1174", {"start": v(3490.24, 1142.9) * mm, "end": v(3481.97, 1166.77) * mm});
            skLineSegment(sketch, "E1175", {"start": v(3481.97, 1166.77) * mm, "end": v(3473.42, 1190.52) * mm});
            skLineSegment(sketch, "E1176", {"start": v(3473.42, 1190.52) * mm, "end": v(3464.61, 1214.14) * mm});
            skLineSegment(sketch, "E1177", {"start": v(3464.61, 1214.14) * mm, "end": v(3455.53, 1237.64) * mm});
            skLineSegment(sketch, "E1178", {"start": v(3455.53, 1237.64) * mm, "end": v(3446.18, 1261) * mm});
            skLineSegment(sketch, "E1179", {"start": v(3446.18, 1261) * mm, "end": v(3436.57, 1284.23) * mm});
            skLineSegment(sketch, "E1180", {"start": v(3436.57, 1284.23) * mm, "end": v(3426.68, 1307.32) * mm});
            skLineSegment(sketch, "E1181", {"start": v(3426.68, 1307.32) * mm, "end": v(3416.53, 1330.25) * mm});
            skLineSegment(sketch, "E1182", {"start": v(3416.53, 1330.25) * mm, "end": v(3406.12, 1353.04) * mm});
            skLineSegment(sketch, "E1183", {"start": v(3406.12, 1353.04) * mm, "end": v(3395.43, 1375.66) * mm});
            skLineSegment(sketch, "E1184", {"start": v(3395.43, 1375.66) * mm, "end": v(3384.49, 1398.12) * mm});
            skLineSegment(sketch, "E1185", {"start": v(3384.49, 1398.12) * mm, "end": v(3373.27, 1420.42) * mm});
            skLineSegment(sketch, "E1186", {"start": v(3373.27, 1420.42) * mm, "end": v(3361.8, 1442.53) * mm});
            skLineSegment(sketch, "E1187", {"start": v(3361.8, 1442.53) * mm, "end": v(3350.05, 1464.48) * mm});
            skLineSegment(sketch, "E1188", {"start": v(3350.05, 1464.48) * mm, "end": v(3338.05, 1486.23) * mm});
            skLineSegment(sketch, "E1189", {"start": v(3338.05, 1486.23) * mm, "end": v(3325.77, 1507.8) * mm});
            skLineSegment(sketch, "E1190", {"start": v(3325.77, 1507.8) * mm, "end": v(3313.24, 1529.17) * mm});
            skLineSegment(sketch, "E1191", {"start": v(3313.24, 1529.17) * mm, "end": v(3300.44, 1550.34) * mm});
            skLineSegment(sketch, "E1192", {"start": v(3300.44, 1550.34) * mm, "end": v(3287.37, 1571.3) * mm});
            skLineSegment(sketch, "E1193", {"start": v(3287.37, 1571.3) * mm, "end": v(3274.05, 1592.06) * mm});
            skLineSegment(sketch, "E1194", {"start": v(3274.05, 1592.06) * mm, "end": v(3260.46, 1612.6) * mm});
            skLineSegment(sketch, "E1195", {"start": v(3260.46, 1612.6) * mm, "end": v(3246.61, 1632.93) * mm});
            skLineSegment(sketch, "E1196", {"start": v(3246.61, 1632.93) * mm, "end": v(3232.5, 1653.03) * mm});
            skLineSegment(sketch, "E1197", {"start": v(3232.5, 1653.03) * mm, "end": v(3218.13, 1672.9) * mm});
            skLineSegment(sketch, "E1198", {"start": v(3218.13, 1672.9) * mm, "end": v(3204.24, 1691.54) * mm});
            skLineSegment(sketch, "E1199", {"start": v(3204.24, 1691.54) * mm, "end": v(3190.05, 1710.04) * mm});
            skLineSegment(sketch, "E1200", {"start": v(3190.05, 1710.04) * mm, "end": v(3175.56, 1728.4) * mm});
            skLineSegment(sketch, "E1201", {"start": v(3175.56, 1728.4) * mm, "end": v(3160.8, 1746.61) * mm});
            skLineSegment(sketch, "E1202", {"start": v(3160.8, 1746.61) * mm, "end": v(3145.74, 1764.68) * mm});
            skLineSegment(sketch, "E1203", {"start": v(3145.74, 1764.68) * mm, "end": v(3130.4, 1782.6) * mm});
            skLineSegment(sketch, "E1204", {"start": v(3130.4, 1782.6) * mm, "end": v(3114.79, 1800.37) * mm});
            skLineSegment(sketch, "E1205", {"start": v(3114.79, 1800.37) * mm, "end": v(3098.9, 1818) * mm});
            skLineSegment(sketch, "E1206", {"start": v(3098.9, 1818) * mm, "end": v(3082.75, 1835.45) * mm});
            skLineSegment(sketch, "E1207", {"start": v(3082.75, 1835.45) * mm, "end": v(3066.33, 1852.76) * mm});
            skLineSegment(sketch, "E1208", {"start": v(3066.33, 1852.76) * mm, "end": v(3049.66, 1869.9) * mm});
            skLineSegment(sketch, "E1209", {"start": v(3049.66, 1869.9) * mm, "end": v(3032.73, 1886.9) * mm});
            skLineSegment(sketch, "E1210", {"start": v(3032.73, 1886.9) * mm, "end": v(3015.55, 1903.71) * mm});
            skLineSegment(sketch, "E1211", {"start": v(3015.55, 1903.71) * mm, "end": v(2998.13, 1920.37) * mm});
            skLineSegment(sketch, "E1212", {"start": v(2998.13, 1920.37) * mm, "end": v(2980.47, 1936.86) * mm});
            skLineSegment(sketch, "E1213", {"start": v(2980.47, 1936.86) * mm, "end": v(2962.57, 1953.18) * mm});
            skLineSegment(sketch, "E1214", {"start": v(2962.57, 1953.18) * mm, "end": v(2944.43, 1969.32) * mm});
            skLineSegment(sketch, "E1215", {"start": v(2944.43, 1969.32) * mm, "end": v(2926.07, 1985.3) * mm});
            skLineSegment(sketch, "E1216", {"start": v(2926.07, 1985.3) * mm, "end": v(2907.5, 2001.09) * mm});
            skLineSegment(sketch, "E1217", {"start": v(2907.5, 2001.09) * mm, "end": v(2888.7, 2016.7) * mm});
            skLineSegment(sketch, "E1218", {"start": v(2888.7, 2016.7) * mm, "end": v(2869.68, 2032.13) * mm});
            skLineSegment(sketch, "E1219", {"start": v(2869.68, 2032.13) * mm, "end": v(2850.45, 2047.38) * mm});
            skLineSegment(sketch, "E1220", {"start": v(2850.45, 2047.38) * mm, "end": v(2831.02, 2062.44) * mm});
            skLineSegment(sketch, "E1221", {"start": v(2831.02, 2062.44) * mm, "end": v(2811.4, 2077.32) * mm});
            skLineSegment(sketch, "E1222", {"start": v(2811.4, 2077.32) * mm, "end": v(2791.56, 2092) * mm});
            skLineSegment(sketch, "E1223", {"start": v(2791.56, 2092) * mm, "end": v(2771.54, 2106.5) * mm});
            skLineSegment(sketch, "E1224", {"start": v(2771.54, 2106.5) * mm, "end": v(2751.34, 2120.8) * mm});
            skLineSegment(sketch, "E1225", {"start": v(2751.34, 2120.8) * mm, "end": v(2730.95, 2134.9) * mm});
            skLineSegment(sketch, "E1226", {"start": v(2730.95, 2134.9) * mm, "end": v(2710.38, 2148.8) * mm});
            skLineSegment(sketch, "E1227", {"start": v(2710.38, 2148.8) * mm, "end": v(2689.64, 2162.5) * mm});
            skLineSegment(sketch, "E1228", {"start": v(2689.64, 2162.5) * mm, "end": v(2668.72, 2176) * mm});
            skLineSegment(sketch, "E1229", {"start": v(2668.72, 2176) * mm, "end": v(2647.65, 2189.28) * mm});
            skLineSegment(sketch, "E1230", {"start": v(2647.65, 2189.28) * mm, "end": v(2626.4, 2202.37) * mm});
            skLineSegment(sketch, "E1231", {"start": v(2626.4, 2202.37) * mm, "end": v(2605, 2215.24) * mm});
            skLineSegment(sketch, "E1232", {"start": v(2605, 2215.24) * mm, "end": v(2583.46, 2227.9) * mm});
            skLineSegment(sketch, "E1233", {"start": v(2583.46, 2227.9) * mm, "end": v(2561.77, 2240.34) * mm});
            skLineSegment(sketch, "E1234", {"start": v(2561.77, 2240.34) * mm, "end": v(2539.93, 2252.57) * mm});
            skLineSegment(sketch, "E1235", {"start": v(2539.93, 2252.57) * mm, "end": v(2517.95, 2264.58) * mm});
            skLineSegment(sketch, "E1236", {"start": v(2517.95, 2264.58) * mm, "end": v(2495.84, 2276.37) * mm});
            skLineSegment(sketch, "E1237", {"start": v(2495.84, 2276.37) * mm, "end": v(2473.6, 2287.93) * mm});
            skLineSegment(sketch, "E1238", {"start": v(2473.6, 2287.93) * mm, "end": v(2451.23, 2299.27) * mm});
            skLineSegment(sketch, "E1239", {"start": v(2451.23, 2299.27) * mm, "end": v(2428.74, 2310.38) * mm});
            skLineSegment(sketch, "E1240", {"start": v(2428.74, 2310.38) * mm, "end": v(2406.13, 2321.27) * mm});
            skLineSegment(sketch, "E1241", {"start": v(2406.13, 2321.27) * mm, "end": v(2383.42, 2331.91) * mm});
            skLineSegment(sketch, "E1242", {"start": v(2383.42, 2331.91) * mm, "end": v(2360.59, 2342.33) * mm});
            skLineSegment(sketch, "E1243", {"start": v(2360.59, 2342.33) * mm, "end": v(2337.66, 2352.5) * mm});
            skLineSegment(sketch, "E1244", {"start": v(2337.66, 2352.5) * mm, "end": v(2314.63, 2362.44) * mm});
            skLineSegment(sketch, "E1245", {"start": v(2314.63, 2362.44) * mm, "end": v(2291.51, 2372.14) * mm});
            skLineSegment(sketch, "E1246", {"start": v(2291.51, 2372.14) * mm, "end": v(2268.3, 2381.6) * mm});
            skLineSegment(sketch, "E1247", {"start": v(2268.3, 2381.6) * mm, "end": v(2245, 2390.8) * mm});
            skLineSegment(sketch, "E1248", {"start": v(2245, 2390.8) * mm, "end": v(2221.62, 2399.76) * mm});
            skLineSegment(sketch, "E1249", {"start": v(2221.62, 2399.76) * mm, "end": v(2198.17, 2408.47) * mm});
            skLineSegment(sketch, "E1250", {"start": v(2198.17, 2408.47) * mm, "end": v(2174.64, 2416.93) * mm});
            skLineSegment(sketch, "E1251", {"start": v(2174.64, 2416.93) * mm, "end": v(2151.04, 2425.13) * mm});
            skLineSegment(sketch, "E1252", {"start": v(2151.04, 2425.13) * mm, "end": v(2127.38, 2433.08) * mm});
            skLineSegment(sketch, "E1253", {"start": v(2127.38, 2433.08) * mm, "end": v(2103.66, 2440.76) * mm});
            skLineSegment(sketch, "E1254", {"start": v(2103.66, 2440.76) * mm, "end": v(2079.9, 2448.19) * mm});
            skLineSegment(sketch, "E1255", {"start": v(2079.9, 2448.19) * mm, "end": v(2056.07, 2455.35) * mm});
            skLineSegment(sketch, "E1256", {"start": v(2056.07, 2455.35) * mm, "end": v(2032.2, 2462.25) * mm});
            skLineSegment(sketch, "E1257", {"start": v(2032.2, 2462.25) * mm, "end": v(2008.29, 2468.88) * mm});
            skLineSegment(sketch, "E1258", {"start": v(2008.29, 2468.88) * mm, "end": v(1984.34, 2475.24) * mm});
            skLineSegment(sketch, "E1259", {"start": v(1984.34, 2475.24) * mm, "end": v(1960.36, 2481.32) * mm});
            skLineSegment(sketch, "E1260", {"start": v(1960.36, 2481.32) * mm, "end": v(1936.35, 2487.13) * mm});
            skLineSegment(sketch, "E1261", {"start": v(1936.35, 2487.13) * mm, "end": v(1912.32, 2492.67) * mm});
            skLineSegment(sketch, "E1262", {"start": v(1912.32, 2492.67) * mm, "end": v(1888.27, 2497.93) * mm});
            skLineSegment(sketch, "E1263", {"start": v(1888.27, 2497.93) * mm, "end": v(1864.2, 2502.9) * mm});
            skLineSegment(sketch, "E1264", {"start": v(1864.2, 2502.9) * mm, "end": v(1840.13, 2507.6) * mm});
            skLineSegment(sketch, "E1265", {"start": v(1840.13, 2507.6) * mm, "end": v(1816.05, 2512) * mm});
            skLineSegment(sketch, "E1266", {"start": v(1816.05, 2512) * mm, "end": v(1791.96, 2516.12) * mm});
            skLineSegment(sketch, "E1267", {"start": v(1791.96, 2516.12) * mm, "end": v(1767.89, 2519.95) * mm});
            skLineSegment(sketch, "E1268", {"start": v(1767.89, 2519.95) * mm, "end": v(1743.81, 2523.49) * mm});
            skLineSegment(sketch, "E1269", {"start": v(1743.81, 2523.49) * mm, "end": v(1719.75, 2526.73) * mm});
            skLineSegment(sketch, "E1270", {"start": v(1719.75, 2526.73) * mm, "end": v(1695.7, 2529.68) * mm});
            skLineSegment(sketch, "E1271", {"start": v(1695.7, 2529.68) * mm, "end": v(1671.69, 2532.32) * mm});
            skLineSegment(sketch, "E1272", {"start": v(1671.69, 2532.32) * mm, "end": v(1647.69, 2534.67) * mm});
            skLineSegment(sketch, "E1273", {"start": v(1647.69, 2534.67) * mm, "end": v(1623.72, 2536.71) * mm});
            skLineSegment(sketch, "E1274", {"start": v(1623.72, 2536.71) * mm, "end": v(1599.78, 2538.45) * mm});
            skLineSegment(sketch, "E1275", {"start": v(1599.78, 2538.45) * mm, "end": v(1575.89, 2539.88) * mm});
            skLineSegment(sketch, "E1276", {"start": v(1575.89, 2539.88) * mm, "end": v(1552.03, 2541) * mm});
            skLineSegment(sketch, "E1277", {"start": v(1552.03, 2541) * mm, "end": v(1528.23, 2541.8) * mm});
            skLineSegment(sketch, "E1278", {"start": v(1528.23, 2541.8) * mm, "end": v(1504.47, 2542.3) * mm});
            skLineSegment(sketch, "E1279", {"start": v(1504.47, 2542.3) * mm, "end": v(1480.77, 2542.48) * mm});
            skLineSegment(sketch, "E1280", {"start": v(1480.77, 2542.48) * mm, "end": v(1457.14, 2542.34) * mm});
            skLineSegment(sketch, "E1281", {"start": v(1457.14, 2542.34) * mm, "end": v(1433.56, 2541.87) * mm});
            skLineSegment(sketch, "E1282", {"start": v(1433.56, 2541.87) * mm, "end": v(1410.06, 2541.09) * mm});
            skLineSegment(sketch, "E1283", {"start": v(1410.06, 2541.09) * mm, "end": v(1386.63, 2539.97) * mm});
            skLineSegment(sketch, "E1284", {"start": v(1386.63, 2539.97) * mm, "end": v(1363.28, 2538.54) * mm});
            skLineSegment(sketch, "E1285", {"start": v(1363.28, 2538.53) * mm, "end": v(1337.9, 2536.62) * mm});
            skLineSegment(sketch, "E1286", {"start": v(1337.9, 2536.62) * mm, "end": v(1312.52, 2534.38) * mm});
            skLineSegment(sketch, "E1287", {"start": v(1312.52, 2534.38) * mm, "end": v(1287.13, 2531.81) * mm});
            skLineSegment(sketch, "E1288", {"start": v(1287.13, 2531.81) * mm, "end": v(1261.75, 2528.92) * mm});
            skLineSegment(sketch, "E1289", {"start": v(1261.75, 2528.92) * mm, "end": v(1236.37, 2525.7) * mm});
            skLineSegment(sketch, "E1290", {"start": v(1236.37, 2525.7) * mm, "end": v(1211, 2522.17) * mm});
            skLineSegment(sketch, "E1291", {"start": v(1211, 2522.17) * mm, "end": v(1185.65, 2518.32) * mm});
            skLineSegment(sketch, "E1292", {"start": v(1185.65, 2518.32) * mm, "end": v(1160.33, 2514.16) * mm});
            skLineSegment(sketch, "E1293", {"start": v(1160.33, 2514.16) * mm, "end": v(1135.03, 2509.7) * mm});
            skLineSegment(sketch, "E1294", {"start": v(1135.03, 2509.7) * mm, "end": v(1109.76, 2504.91) * mm});
            skLineSegment(sketch, "E1295", {"start": v(1109.76, 2504.91) * mm, "end": v(1084.53, 2499.83) * mm});
            skLineSegment(sketch, "E1296", {"start": v(1084.53, 2499.83) * mm, "end": v(1059.34, 2494.44) * mm});
            skLineSegment(sketch, "E1297", {"start": v(1059.34, 2494.44) * mm, "end": v(1034.2, 2488.76) * mm});
            skLineSegment(sketch, "E1298", {"start": v(1034.2, 2488.76) * mm, "end": v(1009.1, 2482.77) * mm});
            skLineSegment(sketch, "E1299", {"start": v(1009.1, 2482.77) * mm, "end": v(984.07, 2476.5) * mm});
            skLineSegment(sketch, "E1300", {"start": v(984.07, 2476.5) * mm, "end": v(959.1, 2469.93) * mm});
            skLineSegment(sketch, "E1301", {"start": v(959.1, 2469.93) * mm, "end": v(934.18, 2463.08) * mm});
            skLineSegment(sketch, "E1302", {"start": v(934.18, 2463.08) * mm, "end": v(909.35, 2455.94) * mm});
            skLineSegment(sketch, "E1303", {"start": v(909.35, 2455.94) * mm, "end": v(884.59, 2448.52) * mm});
            skLineSegment(sketch, "E1304", {"start": v(884.59, 2448.52) * mm, "end": v(859.9, 2440.82) * mm});
            skLineSegment(sketch, "E1305", {"start": v(859.9, 2440.82) * mm, "end": v(835.3, 2432.84) * mm});
            skLineSegment(sketch, "E1306", {"start": v(835.3, 2432.84) * mm, "end": v(810.8, 2424.59) * mm});
            skLineSegment(sketch, "E1307", {"start": v(810.8, 2424.59) * mm, "end": v(786.4, 2416.06) * mm});
            skLineSegment(sketch, "E1308", {"start": v(786.4, 2416.06) * mm, "end": v(762.09, 2407.27) * mm});
            skLineSegment(sketch, "E1309", {"start": v(762.09, 2407.27) * mm, "end": v(737.88, 2398.21) * mm});
            skLineSegment(sketch, "E1310", {"start": v(737.88, 2398.21) * mm, "end": v(713.8, 2388.9) * mm});
            skLineSegment(sketch, "E1311", {"start": v(713.8, 2388.9) * mm, "end": v(689.81, 2379.31) * mm});
            skLineSegment(sketch, "E1312", {"start": v(689.81, 2379.31) * mm, "end": v(665.95, 2369.47) * mm});
            skLineSegment(sketch, "E1313", {"start": v(665.95, 2369.47) * mm, "end": v(642.22, 2359.38) * mm});
            skLineSegment(sketch, "E1314", {"start": v(642.22, 2359.38) * mm, "end": v(618.62, 2349.04) * mm});
            skLineSegment(sketch, "E1315", {"start": v(618.62, 2349.04) * mm, "end": v(595.15, 2338.44) * mm});
            skLineSegment(sketch, "E1316", {"start": v(595.15, 2338.44) * mm, "end": v(571.82, 2327.6) * mm});
            skLineSegment(sketch, "E1317", {"start": v(571.82, 2327.6) * mm, "end": v(548.63, 2316.52) * mm});
            skLineSegment(sketch, "E1318", {"start": v(548.63, 2316.52) * mm, "end": v(525.6, 2305.2) * mm});
            skLineSegment(sketch, "E1319", {"start": v(525.6, 2305.2) * mm, "end": v(502.72, 2293.63) * mm});
            skLineSegment(sketch, "E1320", {"start": v(502.72, 2293.63) * mm, "end": v(480, 2281.84) * mm});
            skLineSegment(sketch, "E1321", {"start": v(480, 2281.84) * mm, "end": v(457.44, 2269.8) * mm});
            skLineSegment(sketch, "E1322", {"start": v(457.44, 2269.8) * mm, "end": v(435.05, 2257.55) * mm});
            skLineSegment(sketch, "E1323", {"start": v(435.05, 2257.55) * mm, "end": v(412.83, 2245.07) * mm});
            skLineSegment(sketch, "E1324", {"start": v(412.83, 2245.07) * mm, "end": v(390.8, 2232.36) * mm});
            skLineSegment(sketch, "E1325", {"start": v(390.8, 2232.36) * mm, "end": v(368.95, 2219.42) * mm});
            skLineSegment(sketch, "E1326", {"start": v(368.95, 2219.42) * mm, "end": v(347.28, 2206.28) * mm});
            skLineSegment(sketch, "E1327", {"start": v(347.28, 2206.28) * mm, "end": v(325.12, 2192.25) * mm});
            skLineSegment(sketch, "E1328", {"start": v(325.12, 2192.25) * mm, "end": v(303.35, 2177.7) * mm});
            skLineSegment(sketch, "E1329", {"start": v(303.35, 2177.7) * mm, "end": v(281.92, 2162.72) * mm});
            skLineSegment(sketch, "E1330", {"start": v(281.92, 2162.72) * mm, "end": v(260.78, 2147.36) * mm});
            skLineSegment(sketch, "E1331", {"start": v(260.78, 2147.36) * mm, "end": v(239.88, 2131.7) * mm});
            skLineSegment(sketch, "E1332", {"start": v(239.88, 2131.7) * mm, "end": v(219.16, 2115.8) * mm});
            skLineSegment(sketch, "E1333", {"start": v(219.16, 2115.8) * mm, "end": v(198.57, 2099.72) * mm});
            skLineSegment(sketch, "E1334", {"start": v(198.57, 2099.72) * mm, "end": v(178.07, 2083.55) * mm});
            skLineSegment(sketch, "E1335", {"start": v(178.07, 2083.55) * mm, "end": v(157.6, 2067.34) * mm});
            skLineSegment(sketch, "E1336", {"start": v(157.6, 2067.34) * mm, "end": v(137.11, 2051.17) * mm});
            skLineSegment(sketch, "E1337", {"start": v(137.11, 2051.17) * mm, "end": v(116.55, 2035.1) * mm});
            skLineSegment(sketch, "E1338", {"start": v(116.55, 2035.1) * mm, "end": v(95.86, 2019.2) * mm});
            skLineSegment(sketch, "E1339", {"start": v(95.86, 2019.2) * mm, "end": v(75, 2003.54) * mm});
            skLineSegment(sketch, "E1340", {"start": v(75, 2003.54) * mm, "end": v(53.92, 1988.19) * mm});
            skLineSegment(sketch, "E1341", {"start": v(53.92, 1988.19) * mm, "end": v(32.56, 1973.2) * mm});
            skLineSegment(sketch, "E1342", {"start": v(32.56, 1973.2) * mm, "end": v(10.86, 1958.67) * mm});
            skLineSegment(sketch, "E1343", {"start": v(10.86, 1958.67) * mm, "end": v(-11.21, 1944.65) * mm});
            skLineSegment(sketch, "E1344", {"start": v(-11.21, 1944.65) * mm, "end": v(-33.72, 1931.21) * mm});
            skLineSegment(sketch, "E1345", {"start": v(-617.92, 1702.61) * mm, "end": v(-617.92, 1651.81) * mm});
            skLineSegment(sketch, "E1346", {"start": v(-617.92, 1651.81) * mm, "end": v(-637.24, 1636.22) * mm});
            skLineSegment(sketch, "E1347", {"start": v(-637.24, 1636.22) * mm, "end": v(-656.42, 1620.13) * mm});
            skLineSegment(sketch, "E1348", {"start": v(-656.42, 1620.13) * mm, "end": v(-675.43, 1603.56) * mm});
            skLineSegment(sketch, "E1349", {"start": v(-675.43, 1603.56) * mm, "end": v(-694.25, 1586.52) * mm});
            skLineSegment(sketch, "E1350", {"start": v(-694.25, 1586.52) * mm, "end": v(-712.85, 1569.01) * mm});
            skLineSegment(sketch, "E1351", {"start": v(-712.85, 1569.01) * mm, "end": v(-731.19, 1551.06) * mm});
            skLineSegment(sketch, "E1352", {"start": v(-731.19, 1551.06) * mm, "end": v(-749.25, 1532.68) * mm});
            skLineSegment(sketch, "E1353", {"start": v(-749.25, 1532.68) * mm, "end": v(-767, 1513.87) * mm});
            skLineSegment(sketch, "E1354", {"start": v(-767, 1513.87) * mm, "end": v(-784.42, 1494.65) * mm});
            skLineSegment(sketch, "E1355", {"start": v(-784.42, 1494.65) * mm, "end": v(-801.46, 1475.03) * mm});
            skLineSegment(sketch, "E1356", {"start": v(-801.46, 1475.03) * mm, "end": v(-818.1, 1455.02) * mm});
            skLineSegment(sketch, "E1357", {"start": v(-818.1, 1455.02) * mm, "end": v(-834.32, 1434.64) * mm});
            skLineSegment(sketch, "E1358", {"start": v(-834.32, 1434.64) * mm, "end": v(-850.08, 1413.9) * mm});
            skLineSegment(sketch, "E1359", {"start": v(-850.08, 1413.9) * mm, "end": v(-865.37, 1392.8) * mm});
            skLineSegment(sketch, "E1360", {"start": v(-865.37, 1392.8) * mm, "end": v(-880.13, 1371.38) * mm});
            skLineSegment(sketch, "E1361", {"start": v(-880.13, 1371.38) * mm, "end": v(-894.35, 1349.62) * mm});
            skLineSegment(sketch, "E1362", {"start": v(-894.35, 1349.62) * mm, "end": v(-908, 1327.55) * mm});
            skLineSegment(sketch, "E1363", {"start": v(-908, 1327.55) * mm, "end": v(-921.06, 1305.18) * mm});
            skLineSegment(sketch, "E1364", {"start": v(-921.06, 1305.18) * mm, "end": v(-933.48, 1282.52) * mm});
            skLineSegment(sketch, "E1365", {"start": v(-933.48, 1282.52) * mm, "end": v(-945.24, 1259.59) * mm});
            skLineSegment(sketch, "E1366", {"start": v(-945.24, 1259.59) * mm, "end": v(-956.32, 1236.39) * mm});
            skLineSegment(sketch, "E1367", {"start": v(-956.32, 1236.39) * mm, "end": v(-966.68, 1212.93) * mm});
            skLineSegment(sketch, "E1368", {"start": v(-966.68, 1212.93) * mm, "end": v(-976.3, 1189.24) * mm});
            skLineSegment(sketch, "E1369", {"start": v(-976.3, 1189.24) * mm, "end": v(-985.13, 1165.32) * mm});
            skLineSegment(sketch, "E1370", {"start": v(-985.13, 1165.32) * mm, "end": v(-993.17, 1141.19) * mm});
            skLineSegment(sketch, "E1371", {"start": v(-993.17, 1141.19) * mm, "end": v(-1000.37, 1116.85) * mm});
            skLineSegment(sketch, "E1372", {"start": v(-1000.37, 1116.85) * mm, "end": v(-1006.72, 1092.32) * mm});
            skLineSegment(sketch, "E1373", {"start": v(-1006.72, 1092.32) * mm, "end": v(-1012.17, 1067.61) * mm});
            skLineSegment(sketch, "E1374", {"start": v(-1012.17, 1067.61) * mm, "end": v(-1016.7, 1043.3) * mm});
            skLineSegment(sketch, "E1375", {"start": v(-1016.7, 1043.3) * mm, "end": v(-1020.6, 1018.74) * mm});
            skLineSegment(sketch, "E1376", {"start": v(-1020.6, 1018.74) * mm, "end": v(-1023.89, 993.95) * mm});
            skLineSegment(sketch, "E1377", {"start": v(-1023.89, 993.95) * mm, "end": v(-1026.6, 968.95) * mm});
            skLineSegment(sketch, "E1378", {"start": v(-1026.6, 968.95) * mm, "end": v(-1028.8, 943.77) * mm});
            skLineSegment(sketch, "E1379", {"start": v(-1028.8, 943.77) * mm, "end": v(-1030.52, 918.42) * mm});
            skLineSegment(sketch, "E1380", {"start": v(-1030.52, 918.42) * mm, "end": v(-1031.79, 892.93) * mm});
            skLineSegment(sketch, "E1381", {"start": v(-1031.79, 892.93) * mm, "end": v(-1032.65, 867.31) * mm});
            skLineSegment(sketch, "E1382", {"start": v(-1032.65, 867.31) * mm, "end": v(-1033.15, 841.6) * mm});
            skLineSegment(sketch, "E1383", {"start": v(-1033.15, 841.6) * mm, "end": v(-1033.33, 815.8) * mm});
            skLineSegment(sketch, "E1384", {"start": v(-1033.33, 815.8) * mm, "end": v(-1033.22, 789.94) * mm});
            skLineSegment(sketch, "E1385", {"start": v(-1033.22, 789.94) * mm, "end": v(-1032.87, 764.04) * mm});
            skLineSegment(sketch, "E1386", {"start": v(-1032.87, 764.04) * mm, "end": v(-1032.31, 738.13) * mm});
            skLineSegment(sketch, "E1387", {"start": v(-1032.31, 738.13) * mm, "end": v(-1031.6, 712.22) * mm});
            skLineSegment(sketch, "E1388", {"start": v(-1031.6, 712.22) * mm, "end": v(-1030.75, 686.34) * mm});
            skLineSegment(sketch, "E1389", {"start": v(-1030.75, 686.34) * mm, "end": v(-1029.84, 660.5) * mm});
            skLineSegment(sketch, "E1390", {"start": v(-1029.84, 660.5) * mm, "end": v(-1028.87, 634.73) * mm});
            skLineSegment(sketch, "E1391", {"start": v(-1028.87, 634.73) * mm, "end": v(-1027.9, 609.05) * mm});
            skLineSegment(sketch, "E1392", {"start": v(-1027.9, 609.05) * mm, "end": v(-1026.98, 583.47) * mm});
            skLineSegment(sketch, "E1393", {"start": v(-1026.98, 583.47) * mm, "end": v(-1026.13, 558.04) * mm});
            skLineSegment(sketch, "E1394", {"start": v(-1026.13, 558.04) * mm, "end": v(-1025.4, 532.75) * mm});
            skLineSegment(sketch, "E1395", {"start": v(-1025.4, 532.75) * mm, "end": v(-1024.83, 507.63) * mm});
            skLineSegment(sketch, "E1396", {"start": v(-1024.83, 507.63) * mm, "end": v(-1024.45, 482.71) * mm});
            skLineSegment(sketch, "E1397", {"start": v(-1024.45, 482.71) * mm, "end": v(-1024.32, 458.01) * mm});
            skLineSegment(sketch, "E1398", {"start": v(-1024.32, 458.01) * mm, "end": v(-1024.32, -405.59) * mm});
            skLineSegment(sketch, "E1399", {"start": v(-1024.32, -405.59) * mm, "end": v(-1024.44, -425.6) * mm});
            skLineSegment(sketch, "E1400", {"start": v(-1024.44, -425.6) * mm, "end": v(-1024.78, -446.01) * mm});
            skLineSegment(sketch, "E1401", {"start": v(-1024.78, -446.01) * mm, "end": v(-1025.3, -466.78) * mm});
            skLineSegment(sketch, "E1402", {"start": v(-1025.3, -466.78) * mm, "end": v(-1025.95, -487.88) * mm});
            skLineSegment(sketch, "E1403", {"start": v(-1025.95, -487.88) * mm, "end": v(-1026.72, -509.27) * mm});
            skLineSegment(sketch, "E1404", {"start": v(-1026.72, -509.27) * mm, "end": v(-1027.55, -530.92) * mm});
            skLineSegment(sketch, "E1405", {"start": v(-1027.55, -530.92) * mm, "end": v(-1028.42, -552.78) * mm});
            skLineSegment(sketch, "E1406", {"start": v(-1028.42, -552.78) * mm, "end": v(-1029.28, -574.82) * mm});
            skLineSegment(sketch, "E1407", {"start": v(-1029.28, -574.82) * mm, "end": v(-1030.1, -597.01) * mm});
            skLineSegment(sketch, "E1408", {"start": v(-1030.1, -597.01) * mm, "end": v(-1030.84, -619.32) * mm});
            skLineSegment(sketch, "E1409", {"start": v(-1030.84, -619.32) * mm, "end": v(-1031.47, -641.7) * mm});
            skLineSegment(sketch, "E1410", {"start": v(-1031.47, -641.7) * mm, "end": v(-1031.94, -664.12) * mm});
            skLineSegment(sketch, "E1411", {"start": v(-1031.94, -664.12) * mm, "end": v(-1032.23, -686.54) * mm});
            skLineSegment(sketch, "E1412", {"start": v(-1032.23, -686.54) * mm, "end": v(-1032.29, -708.92) * mm});
            skLineSegment(sketch, "E1413", {"start": v(-1032.29, -708.92) * mm, "end": v(-1032.08, -731.24) * mm});
            skLineSegment(sketch, "E1414", {"start": v(-1032.08, -731.24) * mm, "end": v(-1031.58, -753.46) * mm});
            skLineSegment(sketch, "E1415", {"start": v(-1031.58, -753.46) * mm, "end": v(-1030.74, -775.53) * mm});
            skLineSegment(sketch, "E1416", {"start": v(-1030.74, -775.53) * mm, "end": v(-1029.52, -797.43) * mm});
            skLineSegment(sketch, "E1417", {"start": v(-1029.52, -797.43) * mm, "end": v(-1027.9, -819.12) * mm});
            skLineSegment(sketch, "E1418", {"start": v(-1027.9, -819.12) * mm, "end": v(-1025.82, -840.55) * mm});
            skLineSegment(sketch, "E1419", {"start": v(-1025.82, -840.55) * mm, "end": v(-1023.27, -861.7) * mm});
            skLineSegment(sketch, "E1420", {"start": v(-1023.27, -861.7) * mm, "end": v(-1020.2, -882.54) * mm});
            skLineSegment(sketch, "E1421", {"start": v(-1020.2, -882.54) * mm, "end": v(-1016.56, -903.01) * mm});
            skLineSegment(sketch, "E1422", {"start": v(-1016.56, -903.01) * mm, "end": v(-1012.32, -923.1) * mm});
            skLineSegment(sketch, "E1423", {"start": v(-1012.32, -923.1) * mm, "end": v(-1007.46, -942.75) * mm});
            skLineSegment(sketch, "E1424", {"start": v(-1007.46, -942.75) * mm, "end": v(-1001.93, -961.95) * mm});
            skLineSegment(sketch, "E1425", {"start": v(-1001.93, -961.95) * mm, "end": v(-995.7, -980.64) * mm});
            skLineSegment(sketch, "E1426", {"start": v(-995.7, -980.64) * mm, "end": v(-988.72, -998.8) * mm});
            skLineSegment(sketch, "E1427", {"start": v(-988.72, -998.8) * mm, "end": v(-980.96, -1016.38) * mm});
            skLineSegment(sketch, "E1428", {"start": v(-980.96, -1016.38) * mm, "end": v(-972.39, -1033.35) * mm});
            skLineSegment(sketch, "E1429", {"start": v(-972.39, -1033.35) * mm, "end": v(-962.96, -1049.69) * mm});
            skLineSegment(sketch, "E1430", {"start": v(-962.96, -1049.69) * mm, "end": v(-952.64, -1065.34) * mm});
            skLineSegment(sketch, "E1431", {"start": v(-952.64, -1065.34) * mm, "end": v(-941.4, -1080.28) * mm});
            skLineSegment(sketch, "E1432", {"start": v(-941.4, -1080.28) * mm, "end": v(-929.2, -1094.46) * mm});
            skLineSegment(sketch, "E1433", {"start": v(-929.2, -1094.46) * mm, "end": v(-915.98, -1107.86) * mm});
            skLineSegment(sketch, "E1434", {"start": v(-915.98, -1107.86) * mm, "end": v(-901.74, -1120.43) * mm});
            skLineSegment(sketch, "E1435", {"start": v(-901.74, -1120.43) * mm, "end": v(-886.42, -1132.15) * mm});
            skLineSegment(sketch, "E1436", {"start": v(-886.42, -1132.15) * mm, "end": v(-870, -1142.97) * mm});
            skLineSegment(sketch, "E1437", {"start": v(-870, -1142.97) * mm, "end": v(-852.41, -1152.86) * mm});
            skLineSegment(sketch, "E1438", {"start": v(-852.41, -1152.86) * mm, "end": v(-833.65, -1161.78) * mm});
            skLineSegment(sketch, "E1439", {"start": v(-833.65, -1161.78) * mm, "end": v(-813.66, -1169.7) * mm});
            skLineSegment(sketch, "E1440", {"start": v(-813.66, -1169.7) * mm, "end": v(-792.42, -1176.58) * mm});
            skLineSegment(sketch, "E1441", {"start": v(-792.42, -1176.58) * mm, "end": v(-769.88, -1182.39) * mm});
            skLineSegment(sketch, "E1442", {"start": v(-769.88, -1182.39) * mm, "end": v(-746, -1187.08) * mm});
            skLineSegment(sketch, "E1443", {"start": v(-746, -1187.08) * mm, "end": v(-720.77, -1190.63) * mm});
            skLineSegment(sketch, "E1444", {"start": v(-720.77, -1190.63) * mm, "end": v(-694.12, -1192.99) * mm});
            skLineSegment(sketch, "E1445", {"start": v(-694.12, -1192.99) * mm, "end": v(-694.12, -2716.99) * mm});
            skLineSegment(sketch, "E1446", {"start": v(-694.12, -2716.99) * mm, "end": v(-715.33, -2705.18) * mm});
            skLineSegment(sketch, "E1447", {"start": v(-715.33, -2705.18) * mm, "end": v(-736.2, -2692.62) * mm});
            skLineSegment(sketch, "E1448", {"start": v(-736.2, -2692.62) * mm, "end": v(-756.74, -2679.33) * mm});
            skLineSegment(sketch, "E1449", {"start": v(-756.74, -2679.33) * mm, "end": v(-776.98, -2665.34) * mm});
            skLineSegment(sketch, "E1450", {"start": v(-776.98, -2665.34) * mm, "end": v(-796.9, -2650.7) * mm});
            skLineSegment(sketch, "E1451", {"start": v(-796.9, -2650.7) * mm, "end": v(-816.56, -2635.45) * mm});
            skLineSegment(sketch, "E1452", {"start": v(-816.56, -2635.45) * mm, "end": v(-835.93, -2619.62) * mm});
            skLineSegment(sketch, "E1453", {"start": v(-835.93, -2619.62) * mm, "end": v(-855.04, -2603.23) * mm});
            skLineSegment(sketch, "E1454", {"start": v(-855.04, -2603.23) * mm, "end": v(-873.9, -2586.34) * mm});
            skLineSegment(sketch, "E1455", {"start": v(-873.9, -2586.34) * mm, "end": v(-892.53, -2568.97) * mm});
            skLineSegment(sketch, "E1456", {"start": v(-892.53, -2568.97) * mm, "end": v(-910.94, -2551.16) * mm});
            skLineSegment(sketch, "E1457", {"start": v(-910.94, -2551.16) * mm, "end": v(-929.14, -2532.94) * mm});
            skLineSegment(sketch, "E1458", {"start": v(-929.14, -2532.94) * mm, "end": v(-947.14, -2514.36) * mm});
            skLineSegment(sketch, "E1459", {"start": v(-947.14, -2514.36) * mm, "end": v(-964.95, -2495.44) * mm});
            skLineSegment(sketch, "E1460", {"start": v(-964.95, -2495.44) * mm, "end": v(-982.6, -2476.23) * mm});
            skLineSegment(sketch, "E1461", {"start": v(-982.6, -2476.23) * mm, "end": v(-1000.08, -2456.75) * mm});
            skLineSegment(sketch, "E1462", {"start": v(-1000.08, -2456.75) * mm, "end": v(-1017.42, -2437.05) * mm});
            skLineSegment(sketch, "E1463", {"start": v(-1017.42, -2437.05) * mm, "end": v(-1034.63, -2417.16) * mm});
            skLineSegment(sketch, "E1464", {"start": v(-1034.63, -2417.16) * mm, "end": v(-1051.72, -2397.12) * mm});
            skLineSegment(sketch, "E1465", {"start": v(-1051.72, -2397.12) * mm, "end": v(-1068.7, -2376.96) * mm});
            skLineSegment(sketch, "E1466", {"start": v(-1068.7, -2376.96) * mm, "end": v(-1085.6, -2356.71) * mm});
            skLineSegment(sketch, "E1467", {"start": v(-1085.6, -2356.71) * mm, "end": v(-1102.4, -2336.42) * mm});
            skLineSegment(sketch, "E1468", {"start": v(-1102.4, -2336.42) * mm, "end": v(-1119.14, -2316.12) * mm});
            skLineSegment(sketch, "E1469", {"start": v(-1119.14, -2316.12) * mm, "end": v(-1135.82, -2295.84) * mm});
            skLineSegment(sketch, "E1470", {"start": v(-1135.82, -2295.84) * mm, "end": v(-1152.46, -2275.62) * mm});
            skLineSegment(sketch, "E1471", {"start": v(-1152.46, -2275.62) * mm, "end": v(-1169.07, -2255.5) * mm});
            skLineSegment(sketch, "E1472", {"start": v(-1169.07, -2255.5) * mm, "end": v(-1185.67, -2235.5) * mm});
            skLineSegment(sketch, "E1473", {"start": v(-1185.67, -2235.5) * mm, "end": v(-1202.26, -2215.68) * mm});
            skLineSegment(sketch, "E1474", {"start": v(-1202.26, -2215.68) * mm, "end": v(-1218.85, -2196.05) * mm});
            skLineSegment(sketch, "E1475", {"start": v(-1218.85, -2196.05) * mm, "end": v(-1235.48, -2176.67) * mm});
            skLineSegment(sketch, "E1476", {"start": v(-1235.48, -2176.67) * mm, "end": v(-1252.13, -2157.56) * mm});
            skLineSegment(sketch, "E1477", {"start": v(-1252.13, -2157.56) * mm, "end": v(-1268.83, -2138.76) * mm});
            skLineSegment(sketch, "E1478", {"start": v(-1268.83, -2138.76) * mm, "end": v(-1285.6, -2120.3) * mm});
            skLineSegment(sketch, "E1479", {"start": v(-1285.6, -2120.3) * mm, "end": v(-1302.43, -2102.23) * mm});
            skLineSegment(sketch, "E1480", {"start": v(-1302.43, -2102.23) * mm, "end": v(-1319.35, -2084.58) * mm});
            skLineSegment(sketch, "E1481", {"start": v(-1319.35, -2084.58) * mm, "end": v(-1336.37, -2067.37) * mm});
            skLineSegment(sketch, "E1482", {"start": v(-1336.37, -2067.37) * mm, "end": v(-1354.16, -2049.7) * mm});
            skLineSegment(sketch, "E1483", {"start": v(-1354.16, -2049.7) * mm, "end": v(-1371.96, -2032) * mm});
            skLineSegment(sketch, "E1484", {"start": v(-1371.96, -2032) * mm, "end": v(-1389.79, -2014.26) * mm});
            skLineSegment(sketch, "E1485", {"start": v(-1389.79, -2014.26) * mm, "end": v(-1407.63, -1996.5) * mm});
            skLineSegment(sketch, "E1486", {"start": v(-1407.63, -1996.5) * mm, "end": v(-1425.5, -1978.7) * mm});
            skLineSegment(sketch, "E1487", {"start": v(-1425.5, -1978.7) * mm, "end": v(-1443.38, -1960.88) * mm});
            skLineSegment(sketch, "E1488", {"start": v(-1443.38, -1960.88) * mm, "end": v(-1461.27, -1943.03) * mm});
            skLineSegment(sketch, "E1489", {"start": v(-1461.27, -1943.03) * mm, "end": v(-1479.18, -1925.14) * mm});
            skLineSegment(sketch, "E1490", {"start": v(-1479.18, -1925.14) * mm, "end": v(-1497.1, -1907.23) * mm});
            skLineSegment(sketch, "E1491", {"start": v(-1497.1, -1907.23) * mm, "end": v(-1515.02, -1889.28) * mm});
            skLineSegment(sketch, "E1492", {"start": v(-1515.02, -1889.28) * mm, "end": v(-1532.96, -1871.3) * mm});
            skLineSegment(sketch, "E1493", {"start": v(-1532.96, -1871.3) * mm, "end": v(-1550.9, -1853.3) * mm});
            skLineSegment(sketch, "E1494", {"start": v(-1550.9, -1853.3) * mm, "end": v(-1568.84, -1835.26) * mm});
            skLineSegment(sketch, "E1495", {"start": v(-1568.84, -1835.26) * mm, "end": v(-1586.78, -1817.19) * mm});
            skLineSegment(sketch, "E1496", {"start": v(-1586.78, -1817.19) * mm, "end": v(-1604.73, -1799.09) * mm});
            skLineSegment(sketch, "E1497", {"start": v(-1604.73, -1799.09) * mm, "end": v(-1622.67, -1780.95) * mm});
            skLineSegment(sketch, "E1498", {"start": v(-1622.67, -1780.95) * mm, "end": v(-1640.61, -1762.79) * mm});
            skLineSegment(sketch, "E1499", {"start": v(-1640.61, -1762.79) * mm, "end": v(-1658.55, -1744.6) * mm});
            skLineSegment(sketch, "E1500", {"start": v(-1658.55, -1744.6) * mm, "end": v(-1676.48, -1726.36) * mm});
            skLineSegment(sketch, "E1501", {"start": v(-1676.48, -1726.36) * mm, "end": v(-1694.4, -1708.1) * mm});
            skLineSegment(sketch, "E1502", {"start": v(-1694.4, -1708.1) * mm, "end": v(-1712.31, -1689.8) * mm});
            skLineSegment(sketch, "E1503", {"start": v(-1712.31, -1689.8) * mm, "end": v(-1730.21, -1671.48) * mm});
            skLineSegment(sketch, "E1504", {"start": v(-1730.21, -1671.48) * mm, "end": v(-1748.1, -1653.12) * mm});
            skLineSegment(sketch, "E1505", {"start": v(-1748.1, -1653.12) * mm, "end": v(-1765.98, -1634.73) * mm});
            skLineSegment(sketch, "E1506", {"start": v(-1765.98, -1634.73) * mm, "end": v(-1783.83, -1616.3) * mm});
            skLineSegment(sketch, "E1507", {"start": v(-1783.83, -1616.3) * mm, "end": v(-1801.67, -1597.84) * mm});
            skLineSegment(sketch, "E1508", {"start": v(-1801.67, -1597.84) * mm, "end": v(-1819.5, -1579.35) * mm});
            skLineSegment(sketch, "E1509", {"start": v(-1819.5, -1579.35) * mm, "end": v(-1837.29, -1560.82) * mm});
            skLineSegment(sketch, "E1510", {"start": v(-1837.29, -1560.82) * mm, "end": v(-1855.06, -1542.26) * mm});
            skLineSegment(sketch, "E1511", {"start": v(-1855.06, -1542.26) * mm, "end": v(-1872.81, -1523.67) * mm});
            skLineSegment(sketch, "E1512", {"start": v(-1872.81, -1523.67) * mm, "end": v(-1890.53, -1505.04) * mm});
            skLineSegment(sketch, "E1513", {"start": v(-1890.53, -1505.04) * mm, "end": v(-1908.23, -1486.38) * mm});
            skLineSegment(sketch, "E1514", {"start": v(-1908.23, -1486.38) * mm, "end": v(-1925.9, -1467.69) * mm});
            skLineSegment(sketch, "E1515", {"start": v(-1925.9, -1467.69) * mm, "end": v(-1943.52, -1448.96) * mm});
            skLineSegment(sketch, "E1516", {"start": v(-1943.52, -1448.96) * mm, "end": v(-1961.12, -1430.2) * mm});
            skLineSegment(sketch, "E1517", {"start": v(-1961.12, -1430.2) * mm, "end": v(-1978.69, -1411.4) * mm});
            skLineSegment(sketch, "E1518", {"start": v(-1978.69, -1411.4) * mm, "end": v(-1996.21, -1392.56) * mm});
            skLineSegment(sketch, "E1519", {"start": v(-1996.21, -1392.56) * mm, "end": v(-2013.7, -1373.69) * mm});
            skLineSegment(sketch, "E1520", {"start": v(-2013.7, -1373.69) * mm, "end": v(-2031.15, -1354.78) * mm});
            skLineSegment(sketch, "E1521", {"start": v(-2031.15, -1354.78) * mm, "end": v(-2048.56, -1335.84) * mm});
            skLineSegment(sketch, "E1522", {"start": v(-2048.56, -1335.84) * mm, "end": v(-2065.92, -1316.87) * mm});
            skLineSegment(sketch, "E1523", {"start": v(-2065.92, -1316.87) * mm, "end": v(-2083.24, -1297.86) * mm});
            skLineSegment(sketch, "E1524", {"start": v(-2083.24, -1297.86) * mm, "end": v(-2100.5, -1278.8) * mm});
            skLineSegment(sketch, "E1525", {"start": v(-2100.5, -1278.8) * mm, "end": v(-2117.73, -1259.73) * mm});
            skLineSegment(sketch, "E1526", {"start": v(-2117.73, -1259.73) * mm, "end": v(-2134.9, -1240.6) * mm});
            skLineSegment(sketch, "E1527", {"start": v(-2134.9, -1240.6) * mm, "end": v(-2152.02, -1221.45) * mm});
            skLineSegment(sketch, "E1528", {"start": v(-2152.02, -1221.45) * mm, "end": v(-2169.08, -1202.26) * mm});
            skLineSegment(sketch, "E1529", {"start": v(-2169.08, -1202.26) * mm, "end": v(-2186.1, -1183.03) * mm});
            skLineSegment(sketch, "E1530", {"start": v(-2186.1, -1183.03) * mm, "end": v(-2203.05, -1163.76) * mm});
            skLineSegment(sketch, "E1531", {"start": v(-2203.05, -1163.76) * mm, "end": v(-2219.94, -1144.46) * mm});
            skLineSegment(sketch, "E1532", {"start": v(-2219.94, -1144.46) * mm, "end": v(-2236.77, -1125.12) * mm});
            skLineSegment(sketch, "E1533", {"start": v(-2236.77, -1125.12) * mm, "end": v(-2253.54, -1105.75) * mm});
            skLineSegment(sketch, "E1534", {"start": v(-2253.54, -1105.75) * mm, "end": v(-2270.25, -1086.33) * mm});
            skLineSegment(sketch, "E1535", {"start": v(-2270.25, -1086.33) * mm, "end": v(-2286.9, -1066.88) * mm});
            skLineSegment(sketch, "E1536", {"start": v(-2286.9, -1066.88) * mm, "end": v(-2303.47, -1047.4) * mm});
            skLineSegment(sketch, "E1537", {"start": v(-2303.47, -1047.4) * mm, "end": v(-2319.97, -1027.86) * mm});
            skLineSegment(sketch, "E1538", {"start": v(-2319.97, -1027.86) * mm, "end": v(-2336.4, -1008.3) * mm});
            skLineSegment(sketch, "E1539", {"start": v(-2336.4, -1008.3) * mm, "end": v(-2352.76, -988.7) * mm});
            skLineSegment(sketch, "E1540", {"start": v(-2352.76, -988.7) * mm, "end": v(-2369.05, -969.06) * mm});
            skLineSegment(sketch, "E1541", {"start": v(-2369.05, -969.06) * mm, "end": v(-2385.26, -949.38) * mm});
            skLineSegment(sketch, "E1542", {"start": v(-2385.26, -949.38) * mm, "end": v(-2401.4, -929.66) * mm});
            skLineSegment(sketch, "E1543", {"start": v(-2401.4, -929.66) * mm, "end": v(-2417.45, -909.9) * mm});
            skLineSegment(sketch, "E1544", {"start": v(-2417.45, -909.9) * mm, "end": v(-2433.43, -890.1) * mm});
            skLineSegment(sketch, "E1545", {"start": v(-2433.43, -890.1) * mm, "end": v(-2449.32, -870.27) * mm});
            skLineSegment(sketch, "E1546", {"start": v(-2449.32, -870.27) * mm, "end": v(-2465.12, -850.4) * mm});
            skLineSegment(sketch, "E1547", {"start": v(-2465.12, -850.4) * mm, "end": v(-2480.84, -830.48) * mm});
            skLineSegment(sketch, "E1548", {"start": v(-2480.84, -830.48) * mm, "end": v(-2496.48, -810.53) * mm});
            skLineSegment(sketch, "E1549", {"start": v(-2496.48, -810.53) * mm, "end": v(-2512.02, -790.54) * mm});
            skLineSegment(sketch, "E1550", {"start": v(-2512.02, -790.54) * mm, "end": v(-2527.47, -770.5) * mm});
            skLineSegment(sketch, "E1551", {"start": v(-2527.47, -770.5) * mm, "end": v(-2542.83, -750.43) * mm});
            skLineSegment(sketch, "E1552", {"start": v(-2542.83, -750.43) * mm, "end": v(-2558.1, -730.32) * mm});
            skLineSegment(sketch, "E1553", {"start": v(-2558.1, -730.32) * mm, "end": v(-2573.27, -710.17) * mm});
            skLineSegment(sketch, "E1554", {"start": v(-2573.27, -710.17) * mm, "end": v(-2588.34, -689.97) * mm});
            skLineSegment(sketch, "E1555", {"start": v(-2588.34, -689.97) * mm, "end": v(-2603.3, -669.74) * mm});
            skLineSegment(sketch, "E1556", {"start": v(-2603.3, -669.74) * mm, "end": v(-2618.18, -649.46) * mm});
            skLineSegment(sketch, "E1557", {"start": v(-2618.18, -649.46) * mm, "end": v(-2632.95, -629.15) * mm});
            skLineSegment(sketch, "E1558", {"start": v(-2632.95, -629.15) * mm, "end": v(-2647.6, -608.79) * mm});
            skLineSegment(sketch, "E1559", {"start": v(-2647.6, -608.79) * mm, "end": v(-2662.42, -588.1) * mm});
            skLineSegment(sketch, "E1560", {"start": v(-2662.42, -588.1) * mm, "end": v(-2677.2, -567.4) * mm});
            skLineSegment(sketch, "E1561", {"start": v(-2677.2, -567.4) * mm, "end": v(-2691.92, -546.68) * mm});
            skLineSegment(sketch, "E1562", {"start": v(-2691.92, -546.68) * mm, "end": v(-2706.58, -525.93) * mm});
            skLineSegment(sketch, "E1563", {"start": v(-2706.58, -525.93) * mm, "end": v(-2721.14, -505.13) * mm});
            skLineSegment(sketch, "E1564", {"start": v(-2721.14, -505.13) * mm, "end": v(-2735.6, -484.29) * mm});
            skLineSegment(sketch, "E1565", {"start": v(-2735.6, -484.29) * mm, "end": v(-2749.92, -463.39) * mm});
            skLineSegment(sketch, "E1566", {"start": v(-2749.92, -463.39) * mm, "end": v(-2764.1, -442.42) * mm});
            skLineSegment(sketch, "E1567", {"start": v(-2764.1, -442.42) * mm, "end": v(-2778.12, -421.38) * mm});
            skLineSegment(sketch, "E1568", {"start": v(-2778.12, -421.38) * mm, "end": v(-2791.96, -400.26) * mm});
            skLineSegment(sketch, "E1569", {"start": v(-2791.96, -400.26) * mm, "end": v(-2805.6, -379.05) * mm});
            skLineSegment(sketch, "E1570", {"start": v(-2805.6, -379.05) * mm, "end": v(-2819.02, -357.74) * mm});
            skLineSegment(sketch, "E1571", {"start": v(-2819.02, -357.74) * mm, "end": v(-2832.2, -336.32) * mm});
            skLineSegment(sketch, "E1572", {"start": v(-2832.2, -336.32) * mm, "end": v(-2845.15, -314.79) * mm});
            skLineSegment(sketch, "E1573", {"start": v(-2845.15, -314.79) * mm, "end": v(-2857.8, -293.13) * mm});
            skLineSegment(sketch, "E1574", {"start": v(-2857.8, -293.13) * mm, "end": v(-2870.18, -271.34) * mm});
            skLineSegment(sketch, "E1575", {"start": v(-2870.18, -271.34) * mm, "end": v(-2882.25, -249.42) * mm});
            skLineSegment(sketch, "E1576", {"start": v(-2882.25, -249.42) * mm, "end": v(-2893.99, -227.34) * mm});
            skLineSegment(sketch, "E1577", {"start": v(-2893.99, -227.34) * mm, "end": v(-2905.39, -205.11) * mm});
            skLineSegment(sketch, "E1578", {"start": v(-2905.39, -205.11) * mm, "end": v(-2916.43, -182.71) * mm});
            skLineSegment(sketch, "E1579", {"start": v(-2916.43, -182.71) * mm, "end": v(-2927.08, -160.15) * mm});
            skLineSegment(sketch, "E1580", {"start": v(-2927.08, -160.15) * mm, "end": v(-2937.34, -137.4) * mm});
            skLineSegment(sketch, "E1581", {"start": v(-2937.34, -137.4) * mm, "end": v(-2947.18, -114.46) * mm});
            skLineSegment(sketch, "E1582", {"start": v(-2947.18, -114.46) * mm, "end": v(-2956.59, -91.32) * mm});
            skLineSegment(sketch, "E1583", {"start": v(-2956.59, -91.32) * mm, "end": v(-2965.54, -67.98) * mm});
            skLineSegment(sketch, "E1584", {"start": v(-2965.54, -67.98) * mm, "end": v(-2974.03, -44.42) * mm});
            skLineSegment(sketch, "E1585", {"start": v(-2974.03, -44.42) * mm, "end": v(-2982.03, -20.64) * mm});
            skLineSegment(sketch, "E1586", {"start": v(-2982.03, -20.64) * mm, "end": v(-2989.51, 3.37) * mm});
            skLineSegment(sketch, "E1587", {"start": v(-2989.51, 3.37) * mm, "end": v(-2996.48, 27.62) * mm});
            skLineSegment(sketch, "E1588", {"start": v(-2996.48, 27.62) * mm, "end": v(-3002.9, 52.12) * mm});
            skLineSegment(sketch, "E1589", {"start": v(-3002.9, 52.12) * mm, "end": v(-3008.76, 76.87) * mm});
            skLineSegment(sketch, "E1590", {"start": v(-3008.76, 76.87) * mm, "end": v(-3014.05, 101.89) * mm});
            skLineSegment(sketch, "E1591", {"start": v(-3014.05, 101.89) * mm, "end": v(-3018.73, 127.18) * mm});
            skLineSegment(sketch, "E1592", {"start": v(-3018.73, 127.18) * mm, "end": v(-3022.8, 152.75) * mm});
            skLineSegment(sketch, "E1593", {"start": v(-3022.8, 152.75) * mm, "end": v(-3026.23, 178.61) * mm});
            skLineSegment(sketch, "E1594", {"start": v(-3026.23, 178.61) * mm, "end": v(-3028.92, 202.52) * mm});
            skLineSegment(sketch, "E1595", {"start": v(-3028.92, 202.52) * mm, "end": v(-3031.28, 226.66) * mm});
            skLineSegment(sketch, "E1596", {"start": v(-3031.28, 226.66) * mm, "end": v(-3033.31, 251.03) * mm});
            skLineSegment(sketch, "E1597", {"start": v(-3033.31, 251.03) * mm, "end": v(-3035.02, 275.58) * mm});
            skLineSegment(sketch, "E1598", {"start": v(-3035.02, 275.58) * mm, "end": v(-3036.39, 300.33) * mm});
            skLineSegment(sketch, "E1599", {"start": v(-3036.39, 300.33) * mm, "end": v(-3037.43, 325.23) * mm});
            skLineSegment(sketch, "E1600", {"start": v(-3037.43, 325.23) * mm, "end": v(-3038.14, 350.29) * mm});
            skLineSegment(sketch, "E1601", {"start": v(-3038.14, 350.29) * mm, "end": v(-3038.52, 375.47) * mm});
            skLineSegment(sketch, "E1602", {"start": v(-3038.52, 375.47) * mm, "end": v(-3038.55, 400.77) * mm});
            skLineSegment(sketch, "E1603", {"start": v(-3038.55, 400.77) * mm, "end": v(-3038.26, 426.16) * mm});
            skLineSegment(sketch, "E1604", {"start": v(-3038.26, 426.16) * mm, "end": v(-3037.62, 451.63) * mm});
            skLineSegment(sketch, "E1605", {"start": v(-3037.62, 451.63) * mm, "end": v(-3036.65, 477.17) * mm});
            skLineSegment(sketch, "E1606", {"start": v(-3036.65, 477.17) * mm, "end": v(-3035.33, 502.74) * mm});
            skLineSegment(sketch, "E1607", {"start": v(-3035.33, 502.74) * mm, "end": v(-3033.67, 528.35) * mm});
            skLineSegment(sketch, "E1608", {"start": v(-3033.67, 528.35) * mm, "end": v(-3031.68, 553.97) * mm});
            skLineSegment(sketch, "E1609", {"start": v(-3031.68, 553.97) * mm, "end": v(-3029.33, 579.58) * mm});
            skLineSegment(sketch, "E1610", {"start": v(-3029.33, 579.58) * mm, "end": v(-3026.64, 605.17) * mm});
            skLineSegment(sketch, "E1611", {"start": v(-3026.64, 605.17) * mm, "end": v(-3023.6, 630.72) * mm});
            skLineSegment(sketch, "E1612", {"start": v(-3023.6, 630.72) * mm, "end": v(-3020.21, 656.2) * mm});
            skLineSegment(sketch, "E1613", {"start": v(-3020.21, 656.2) * mm, "end": v(-3016.47, 681.62) * mm});
            skLineSegment(sketch, "E1614", {"start": v(-3016.47, 681.62) * mm, "end": v(-3012.39, 706.94) * mm});
            skLineSegment(sketch, "E1615", {"start": v(-3012.39, 706.94) * mm, "end": v(-3007.94, 732.15) * mm});
            skLineSegment(sketch, "E1616", {"start": v(-3007.94, 732.15) * mm, "end": v(-3003.15, 757.24) * mm});
            skLineSegment(sketch, "E1617", {"start": v(-3003.15, 757.24) * mm, "end": v(-2998, 782.18) * mm});
            skLineSegment(sketch, "E1618", {"start": v(-2998, 782.18) * mm, "end": v(-2992.5, 806.97) * mm});
            skLineSegment(sketch, "E1619", {"start": v(-2992.5, 806.97) * mm, "end": v(-2986.63, 831.57) * mm});
            skLineSegment(sketch, "E1620", {"start": v(-2986.63, 831.57) * mm, "end": v(-2980.4, 855.98) * mm});
            skLineSegment(sketch, "E1621", {"start": v(-2980.4, 855.98) * mm, "end": v(-2973.82, 880.18) * mm});
            skLineSegment(sketch, "E1622", {"start": v(-2973.82, 880.18) * mm, "end": v(-2966.87, 904.15) * mm});
            skLineSegment(sketch, "E1623", {"start": v(-2966.87, 904.15) * mm, "end": v(-2959.56, 927.87) * mm});
            skLineSegment(sketch, "E1624", {"start": v(-2959.56, 927.87) * mm, "end": v(-2951.89, 951.34) * mm});
            skLineSegment(sketch, "E1625", {"start": v(-2951.89, 951.34) * mm, "end": v(-2943.85, 974.52) * mm});
            skLineSegment(sketch, "E1626", {"start": v(-2943.85, 974.52) * mm, "end": v(-2935.44, 997.4) * mm});
            skLineSegment(sketch, "E1627", {"start": v(-2935.44, 997.4) * mm, "end": v(-2926.67, 1019.97) * mm});
            skLineSegment(sketch, "E1628", {"start": v(-2926.67, 1019.97) * mm, "end": v(-2917.52, 1042.21) * mm});
            skLineSegment(sketch, "E1629", {"start": v(-2917.52, 1042.21) * mm, "end": v(-2907.8, 1064.67) * mm});
            skLineSegment(sketch, "E1630", {"start": v(-2907.8, 1064.67) * mm, "end": v(-2897.77, 1086.85) * mm});
            skLineSegment(sketch, "E1631", {"start": v(-2897.77, 1086.85) * mm, "end": v(-2887.43, 1108.74) * mm});
            skLineSegment(sketch, "E1632", {"start": v(-2887.43, 1108.74) * mm, "end": v(-2876.78, 1130.34) * mm});
            skLineSegment(sketch, "E1633", {"start": v(-2876.78, 1130.34) * mm, "end": v(-2865.82, 1151.66) * mm});
            skLineSegment(sketch, "E1634", {"start": v(-2865.82, 1151.66) * mm, "end": v(-2854.57, 1172.7) * mm});
            skLineSegment(sketch, "E1635", {"start": v(-2854.57, 1172.7) * mm, "end": v(-2843.02, 1193.45) * mm});
            skLineSegment(sketch, "E1636", {"start": v(-2843.02, 1193.45) * mm, "end": v(-2831.17, 1213.91) * mm});
            skLineSegment(sketch, "E1637", {"start": v(-2831.17, 1213.91) * mm, "end": v(-2819.04, 1234.1) * mm});
            skLineSegment(sketch, "E1638", {"start": v(-2819.04, 1234.1) * mm, "end": v(-2806.63, 1253.99) * mm});
            skLineSegment(sketch, "E1639", {"start": v(-2806.63, 1253.99) * mm, "end": v(-2793.93, 1273.6) * mm});
            skLineSegment(sketch, "E1640", {"start": v(-2793.93, 1273.6) * mm, "end": v(-2780.96, 1292.91) * mm});
            skLineSegment(sketch, "E1641", {"start": v(-2780.96, 1292.91) * mm, "end": v(-2767.72, 1311.95) * mm});
            skLineSegment(sketch, "E1642", {"start": v(-2767.72, 1311.95) * mm, "end": v(-2754.2, 1330.7) * mm});
            skLineSegment(sketch, "E1643", {"start": v(-2754.2, 1330.7) * mm, "end": v(-2740.43, 1349.17) * mm});
            skLineSegment(sketch, "E1644", {"start": v(-2740.43, 1349.17) * mm, "end": v(-2726.4, 1367.35) * mm});
            skLineSegment(sketch, "E1645", {"start": v(-2726.4, 1367.35) * mm, "end": v(-2712.1, 1385.24) * mm});
            skLineSegment(sketch, "E1646", {"start": v(-2712.1, 1385.24) * mm, "end": v(-2697.55, 1402.85) * mm});
            skLineSegment(sketch, "E1647", {"start": v(-2697.55, 1402.85) * mm, "end": v(-2682.76, 1420.17) * mm});
            skLineSegment(sketch, "E1648", {"start": v(-2682.76, 1420.17) * mm, "end": v(-2667.71, 1437.2) * mm});
            skLineSegment(sketch, "E1649", {"start": v(-2667.71, 1437.2) * mm, "end": v(-2652.43, 1453.95) * mm});
            skLineSegment(sketch, "E1650", {"start": v(-2652.43, 1453.95) * mm, "end": v(-2636.91, 1470.42) * mm});
            skLineSegment(sketch, "E1651", {"start": v(-2636.91, 1470.42) * mm, "end": v(-2621.16, 1486.6) * mm});
            skLineSegment(sketch, "E1652", {"start": v(-2621.16, 1486.6) * mm, "end": v(-2605.18, 1502.49) * mm});
            skLineSegment(sketch, "E1653", {"start": v(-2605.18, 1502.49) * mm, "end": v(-2588.97, 1518.1) * mm});
            skLineSegment(sketch, "E1654", {"start": v(-2588.97, 1518.1) * mm, "end": v(-2572.55, 1533.41) * mm});
            skLineSegment(sketch, "E1655", {"start": v(-2572.55, 1533.41) * mm, "end": v(-2555.9, 1548.45) * mm});
            skLineSegment(sketch, "E1656", {"start": v(-2555.9, 1548.45) * mm, "end": v(-2539.04, 1563.2) * mm});
            skLineSegment(sketch, "E1657", {"start": v(-2539.04, 1563.2) * mm, "end": v(-2521.97, 1577.65) * mm});
            skLineSegment(sketch, "E1658", {"start": v(-2521.97, 1577.65) * mm, "end": v(-2504.7, 1591.83) * mm});
            skLineSegment(sketch, "E1659", {"start": v(-2504.7, 1591.83) * mm, "end": v(-2487.22, 1605.72) * mm});
            skLineSegment(sketch, "E1660", {"start": v(-2487.22, 1605.72) * mm, "end": v(-2469.54, 1619.32) * mm});
            skLineSegment(sketch, "E1661", {"start": v(-2469.54, 1619.32) * mm, "end": v(-2451.67, 1632.64) * mm});
            skLineSegment(sketch, "E1662", {"start": v(-2451.67, 1632.64) * mm, "end": v(-2433.61, 1645.67) * mm});
            skLineSegment(sketch, "E1663", {"start": v(-2433.61, 1645.67) * mm, "end": v(-2415.36, 1658.41) * mm});
            skLineSegment(sketch, "E1664", {"start": v(-2415.36, 1658.41) * mm, "end": v(-2396.94, 1670.87) * mm});
            skLineSegment(sketch, "E1665", {"start": v(-2396.94, 1670.87) * mm, "end": v(-2378.33, 1683.04) * mm});
            skLineSegment(sketch, "E1666", {"start": v(-2378.33, 1683.04) * mm, "end": v(-2359.55, 1694.92) * mm});
            skLineSegment(sketch, "E1667", {"start": v(-2359.55, 1694.92) * mm, "end": v(-2340.6, 1706.52) * mm});
            skLineSegment(sketch, "E1668", {"start": v(-2340.6, 1706.52) * mm, "end": v(-2321.48, 1717.83) * mm});
            skLineSegment(sketch, "E1669", {"start": v(-2321.48, 1717.83) * mm, "end": v(-2302.2, 1728.85) * mm});
            skLineSegment(sketch, "E1670", {"start": v(-2302.2, 1728.85) * mm, "end": v(-2282.75, 1739.6) * mm});
            skLineSegment(sketch, "E1671", {"start": v(-2282.75, 1739.6) * mm, "end": v(-2263.16, 1750.04) * mm});
            skLineSegment(sketch, "E1672", {"start": v(-2263.16, 1750.04) * mm, "end": v(-2243.41, 1760.2) * mm});
            skLineSegment(sketch, "E1673", {"start": v(-2243.41, 1760.2) * mm, "end": v(-2223.52, 1770.08) * mm});
            skLineSegment(sketch, "E1674", {"start": v(-2223.52, 1770.08) * mm, "end": v(-2203.48, 1779.67) * mm});
            skLineSegment(sketch, "E1675", {"start": v(-2203.48, 1779.67) * mm, "end": v(-2183.3, 1788.98) * mm});
            skLineSegment(sketch, "E1676", {"start": v(-2183.3, 1788.98) * mm, "end": v(-2163, 1798) * mm});
            skLineSegment(sketch, "E1677", {"start": v(-2163, 1798) * mm, "end": v(-2142.55, 1806.72) * mm});
            skLineSegment(sketch, "E1678", {"start": v(-2142.55, 1806.72) * mm, "end": v(-2121.97, 1815.17) * mm});
            skLineSegment(sketch, "E1679", {"start": v(-2121.97, 1815.17) * mm, "end": v(-2101.28, 1823.32) * mm});
            skLineSegment(sketch, "E1680", {"start": v(-2101.28, 1823.32) * mm, "end": v(-2080.47, 1831.2) * mm});
            skLineSegment(sketch, "E1681", {"start": v(-2080.47, 1831.2) * mm, "end": v(-2059.53, 1838.77) * mm});
            skLineSegment(sketch, "E1682", {"start": v(-2059.53, 1838.77) * mm, "end": v(-2038.5, 1846.06) * mm});
            skLineSegment(sketch, "E1683", {"start": v(-2038.5, 1846.06) * mm, "end": v(-2017.34, 1853.07) * mm});
            skLineSegment(sketch, "E1684", {"start": v(-2017.34, 1853.07) * mm, "end": v(-1996.08, 1859.8) * mm});
            skLineSegment(sketch, "E1685", {"start": v(-1996.08, 1859.8) * mm, "end": v(-1974.73, 1866.22) * mm});
            skLineSegment(sketch, "E1686", {"start": v(-1974.73, 1866.22) * mm, "end": v(-1953.28, 1872.37) * mm});
            skLineSegment(sketch, "E1687", {"start": v(-1953.28, 1872.37) * mm, "end": v(-1931.73, 1878.23) * mm});
            skLineSegment(sketch, "E1688", {"start": v(-1931.73, 1878.23) * mm, "end": v(-1910.1, 1883.8) * mm});
            skLineSegment(sketch, "E1689", {"start": v(-1910.1, 1883.8) * mm, "end": v(-1888.39, 1889.08) * mm});
            skLineSegment(sketch, "E1690", {"start": v(-1888.39, 1889.08) * mm, "end": v(-1866.59, 1894.08) * mm});
            skLineSegment(sketch, "E1691", {"start": v(-1866.59, 1894.08) * mm, "end": v(-1844.71, 1898.79) * mm});
            skLineSegment(sketch, "E1692", {"start": v(-1844.71, 1898.79) * mm, "end": v(-1822.76, 1903.2) * mm});
            skLineSegment(sketch, "E1693", {"start": v(-1822.76, 1903.2) * mm, "end": v(-1800.75, 1907.34) * mm});
            skLineSegment(sketch, "E1694", {"start": v(-1800.75, 1907.34) * mm, "end": v(-1778.67, 1911.19) * mm});
            skLineSegment(sketch, "E1695", {"start": v(-1778.67, 1911.19) * mm, "end": v(-1756.52, 1914.75) * mm});
            skLineSegment(sketch, "E1696", {"start": v(-1756.52, 1914.75) * mm, "end": v(-1734.32, 1918.02) * mm});
            skLineSegment(sketch, "E1697", {"start": v(-1734.32, 1918.02) * mm, "end": v(-1712.07, 1921) * mm});
            skLineSegment(sketch, "E1698", {"start": v(-1712.07, 1921) * mm, "end": v(-1689.77, 1923.7) * mm});
            skLineSegment(sketch, "E1699", {"start": v(-1689.77, 1923.7) * mm, "end": v(-1667.42, 1926.1) * mm});
            skLineSegment(sketch, "E1700", {"start": v(-1667.42, 1926.1) * mm, "end": v(-1645.03, 1928.23) * mm});
            skLineSegment(sketch, "E1701", {"start": v(-1645.03, 1928.23) * mm, "end": v(-1622.6, 1930.06) * mm});
            skLineSegment(sketch, "E1702", {"start": v(-1622.6, 1930.06) * mm, "end": v(-1600.14, 1931.6) * mm});
            skLineSegment(sketch, "E1703", {"start": v(-1600.14, 1931.6) * mm, "end": v(-1577.65, 1932.86) * mm});
            skLineSegment(sketch, "E1704", {"start": v(-1577.65, 1932.86) * mm, "end": v(-1555.14, 1933.83) * mm});
            skLineSegment(sketch, "E1705", {"start": v(-1555.14, 1933.83) * mm, "end": v(-1532.6, 1934.5) * mm});
            skLineSegment(sketch, "E1706", {"start": v(-1532.6, 1934.5) * mm, "end": v(-1510.04, 1934.9) * mm});
            skLineSegment(sketch, "E1707", {"start": v(-1510.04, 1934.9) * mm, "end": v(-1487.47, 1935) * mm});
            skLineSegment(sketch, "E1708", {"start": v(-1487.47, 1935) * mm, "end": v(-1464.89, 1934.82) * mm});
            skLineSegment(sketch, "E1709", {"start": v(-1464.89, 1934.82) * mm, "end": v(-1442.3, 1934.35) * mm});
            skLineSegment(sketch, "E1710", {"start": v(-1442.3, 1934.35) * mm, "end": v(-1419.71, 1933.6) * mm});
            skLineSegment(sketch, "E1711", {"start": v(-1419.71, 1933.6) * mm, "end": v(-1397.12, 1932.54) * mm});
            skLineSegment(sketch, "E1712", {"start": v(-1397.12, 1932.54) * mm, "end": v(-1374.54, 1931.2) * mm});
            skLineSegment(sketch, "E1713", {"start": v(-1374.54, 1931.2) * mm, "end": v(-1351.97, 1929.58) * mm});
            skLineSegment(sketch, "E1714", {"start": v(-1351.97, 1929.58) * mm, "end": v(-1329.4, 1927.67) * mm});
            skLineSegment(sketch, "E1715", {"start": v(-1329.4, 1927.67) * mm, "end": v(-1306.86, 1925.47) * mm});
            skLineSegment(sketch, "E1716", {"start": v(-1306.86, 1925.47) * mm, "end": v(-1284.34, 1922.98) * mm});
            skLineSegment(sketch, "E1717", {"start": v(-1284.34, 1922.98) * mm, "end": v(-1261.84, 1920.2) * mm});
            skLineSegment(sketch, "E1718", {"start": v(-1261.84, 1920.2) * mm, "end": v(-1239.38, 1917.14) * mm});
            skLineSegment(sketch, "E1719", {"start": v(-1239.38, 1917.14) * mm, "end": v(-1216.94, 1913.78) * mm});
            skLineSegment(sketch, "E1720", {"start": v(-1216.94, 1913.78) * mm, "end": v(-1194.54, 1910.14) * mm});
            skLineSegment(sketch, "E1721", {"start": v(-1194.54, 1910.14) * mm, "end": v(-1172.18, 1906.21) * mm});
            skLineSegment(sketch, "E1722", {"start": v(-1172.18, 1906.21) * mm, "end": v(-1149.87, 1902) * mm});
            skLineSegment(sketch, "E1723", {"start": v(-1149.87, 1902) * mm, "end": v(-1127.6, 1897.48) * mm});
            skLineSegment(sketch, "E1724", {"start": v(-1127.6, 1897.48) * mm, "end": v(-1105.39, 1892.69) * mm});
            skLineSegment(sketch, "E1725", {"start": v(-1105.39, 1892.69) * mm, "end": v(-1083.23, 1887.6) * mm});
            skLineSegment(sketch, "E1726", {"start": v(-1083.23, 1887.6) * mm, "end": v(-1061.13, 1882.23) * mm});
            skLineSegment(sketch, "E1727", {"start": v(-1061.13, 1882.23) * mm, "end": v(-1039.1, 1876.56) * mm});
            skLineSegment(sketch, "E1728", {"start": v(-1039.1, 1876.56) * mm, "end": v(-1017.14, 1870.61) * mm});
            skLineSegment(sketch, "E1729", {"start": v(-1017.14, 1870.61) * mm, "end": v(-995.24, 1864.37) * mm});
            skLineSegment(sketch, "E1730", {"start": v(-995.24, 1864.37) * mm, "end": v(-973.42, 1857.84) * mm});
            skLineSegment(sketch, "E1731", {"start": v(-973.42, 1857.84) * mm, "end": v(-951.69, 1851.02) * mm});
            skLineSegment(sketch, "E1732", {"start": v(-951.69, 1851.02) * mm, "end": v(-930.03, 1843.91) * mm});
            skLineSegment(sketch, "E1733", {"start": v(-930.03, 1843.91) * mm, "end": v(-908.47, 1836.52) * mm});
            skLineSegment(sketch, "E1734", {"start": v(-908.47, 1836.52) * mm, "end": v(-887, 1828.83) * mm});
            skLineSegment(sketch, "E1735", {"start": v(-887, 1828.83) * mm, "end": v(-865.61, 1820.86) * mm});
            skLineSegment(sketch, "E1736", {"start": v(-865.61, 1820.86) * mm, "end": v(-844.33, 1812.6) * mm});
            skLineSegment(sketch, "E1737", {"start": v(-844.33, 1812.6) * mm, "end": v(-823.16, 1804.04) * mm});
            skLineSegment(sketch, "E1738", {"start": v(-823.16, 1804.04) * mm, "end": v(-802.09, 1795.2) * mm});
            skLineSegment(sketch, "E1739", {"start": v(-802.09, 1795.2) * mm, "end": v(-781.13, 1786.07) * mm});
            skLineSegment(sketch, "E1740", {"start": v(-781.13, 1786.07) * mm, "end": v(-760.28, 1776.65) * mm});
            skLineSegment(sketch, "E1741", {"start": v(-760.28, 1776.65) * mm, "end": v(-739.56, 1766.94) * mm});
            skLineSegment(sketch, "E1742", {"start": v(-739.56, 1766.94) * mm, "end": v(-718.95, 1756.94) * mm});
            skLineSegment(sketch, "E1743", {"start": v(-718.95, 1756.94) * mm, "end": v(-698.48, 1746.65) * mm});
            skLineSegment(sketch, "E1744", {"start": v(-698.48, 1746.65) * mm, "end": v(-678.13, 1736.08) * mm});
            skLineSegment(sketch, "E1745", {"start": v(-678.13, 1736.08) * mm, "end": v(-657.92, 1725.21) * mm});
            skLineSegment(sketch, "E1746", {"start": v(-657.92, 1725.21) * mm, "end": v(-637.85, 1714.06) * mm});
            skLineSegment(sketch, "E1747", {"start": v(-637.85, 1714.06) * mm, "end": v(-617.92, 1702.61) * mm});
            skLineSegment(sketch, "E1748", {"start": v(702.88, -2716.99) * mm, "end": v(702.88, -1192.99) * mm});
            skLineSegment(sketch, "E1749", {"start": v(702.88, -1192.99) * mm, "end": v(729.45, -1188.37) * mm});
            skLineSegment(sketch, "E1750", {"start": v(729.45, -1188.37) * mm, "end": v(754.61, -1182.75) * mm});
            skLineSegment(sketch, "E1751", {"start": v(754.61, -1182.75) * mm, "end": v(778.4, -1176.14) * mm});
            skLineSegment(sketch, "E1752", {"start": v(778.4, -1176.14) * mm, "end": v(800.86, -1168.6) * mm});
            skLineSegment(sketch, "E1753", {"start": v(800.86, -1168.6) * mm, "end": v(822.01, -1160.13) * mm});
            skLineSegment(sketch, "E1754", {"start": v(822.01, -1160.13) * mm, "end": v(841.9, -1150.78) * mm});
            skLineSegment(sketch, "E1755", {"start": v(841.9, -1150.78) * mm, "end": v(860.58, -1140.57) * mm});
            skLineSegment(sketch, "E1756", {"start": v(860.58, -1140.57) * mm, "end": v(878.07, -1129.53) * mm});
            skLineSegment(sketch, "E1757", {"start": v(878.07, -1129.53) * mm, "end": v(894.4, -1117.7) * mm});
            skLineSegment(sketch, "E1758", {"start": v(894.4, -1117.7) * mm, "end": v(909.63, -1105.08) * mm});
            skLineSegment(sketch, "E1759", {"start": v(909.63, -1105.08) * mm, "end": v(923.79, -1091.73) * mm});
            skLineSegment(sketch, "E1760", {"start": v(923.79, -1091.73) * mm, "end": v(936.9, -1077.66) * mm});
            skLineSegment(sketch, "E1761", {"start": v(936.9, -1077.66) * mm, "end": v(949.03, -1062.92) * mm});
            skLineSegment(sketch, "E1762", {"start": v(949.03, -1062.92) * mm, "end": v(960.18, -1047.52) * mm});
            skLineSegment(sketch, "E1763", {"start": v(960.18, -1047.52) * mm, "end": v(970.41, -1031.5) * mm});
            skLineSegment(sketch, "E1764", {"start": v(970.41, -1031.5) * mm, "end": v(979.76, -1014.87) * mm});
            skLineSegment(sketch, "E1765", {"start": v(979.76, -1014.87) * mm, "end": v(988.26, -997.69) * mm});
            skLineSegment(sketch, "E1766", {"start": v(988.26, -997.69) * mm, "end": v(995.94, -979.96) * mm});
            skLineSegment(sketch, "E1767", {"start": v(995.94, -979.96) * mm, "end": v(1002.86, -961.73) * mm});
            skLineSegment(sketch, "E1768", {"start": v(1002.86, -961.73) * mm, "end": v(1009.03, -943.03) * mm});
            skLineSegment(sketch, "E1769", {"start": v(1009.03, -943.03) * mm, "end": v(1014.5, -923.87) * mm});
            skLineSegment(sketch, "E1770", {"start": v(1014.5, -923.87) * mm, "end": v(1019.31, -904.3) * mm});
            skLineSegment(sketch, "E1771", {"start": v(1019.31, -904.3) * mm, "end": v(1023.5, -884.33) * mm});
            skLineSegment(sketch, "E1772", {"start": v(1023.5, -884.33) * mm, "end": v(1027.1, -864) * mm});
            skLineSegment(sketch, "E1773", {"start": v(1027.1, -864) * mm, "end": v(1030.15, -843.34) * mm});
            skLineSegment(sketch, "E1774", {"start": v(1030.15, -843.34) * mm, "end": v(1032.68, -822.38) * mm});
            skLineSegment(sketch, "E1775", {"start": v(1032.68, -822.38) * mm, "end": v(1034.74, -801.15) * mm});
            skLineSegment(sketch, "E1776", {"start": v(1034.74, -801.15) * mm, "end": v(1036.36, -779.67) * mm});
            skLineSegment(sketch, "E1777", {"start": v(1036.36, -779.67) * mm, "end": v(1037.58, -757.97) * mm});
            skLineSegment(sketch, "E1778", {"start": v(1037.58, -757.97) * mm, "end": v(1038.44, -736.1) * mm});
            skLineSegment(sketch, "E1779", {"start": v(1038.44, -736.1) * mm, "end": v(1038.97, -714.06) * mm});
            skLineSegment(sketch, "E1780", {"start": v(1038.97, -714.06) * mm, "end": v(1039.2, -691.9) * mm});
            skLineSegment(sketch, "E1781", {"start": v(1039.2, -691.9) * mm, "end": v(1039.2, -669.64) * mm});
            skLineSegment(sketch, "E1782", {"start": v(1039.2, -669.64) * mm, "end": v(1038.97, -647.32) * mm});
            skLineSegment(sketch, "E1783", {"start": v(1038.97, -647.32) * mm, "end": v(1038.58, -624.95) * mm});
            skLineSegment(sketch, "E1784", {"start": v(1038.58, -624.95) * mm, "end": v(1038.03, -602.58) * mm});
            skLineSegment(sketch, "E1785", {"start": v(1038.03, -602.58) * mm, "end": v(1037.4, -580.22) * mm});
            skLineSegment(sketch, "E1786", {"start": v(1037.4, -580.22) * mm, "end": v(1036.69, -557.91) * mm});
            skLineSegment(sketch, "E1787", {"start": v(1036.69, -557.91) * mm, "end": v(1035.95, -535.69) * mm});
            skLineSegment(sketch, "E1788", {"start": v(1035.95, -535.69) * mm, "end": v(1035.23, -513.56) * mm});
            skLineSegment(sketch, "E1789", {"start": v(1035.23, -513.56) * mm, "end": v(1034.56, -491.58) * mm});
            skLineSegment(sketch, "E1790", {"start": v(1034.56, -491.58) * mm, "end": v(1033.97, -469.76) * mm});
            skLineSegment(sketch, "E1791", {"start": v(1033.97, -469.76) * mm, "end": v(1033.5, -448.13) * mm});
            skLineSegment(sketch, "E1792", {"start": v(1033.5, -448.13) * mm, "end": v(1033.2, -426.74) * mm});
            skLineSegment(sketch, "E1793", {"start": v(1033.2, -426.74) * mm, "end": v(1033.08, -405.59) * mm});
            skLineSegment(sketch, "E1794", {"start": v(1033.08, -405.59) * mm, "end": v(1033.08, 458.01) * mm});
            skLineSegment(sketch, "E1795", {"start": v(1033.08, 458.01) * mm, "end": v(1033.07, 483.57) * mm});
            skLineSegment(sketch, "E1796", {"start": v(1033.07, 483.57) * mm, "end": v(1033.03, 509.03) * mm});
            skLineSegment(sketch, "E1797", {"start": v(1033.03, 509.03) * mm, "end": v(1032.95, 534.4) * mm});
            skLineSegment(sketch, "E1798", {"start": v(1032.95, 534.4) * mm, "end": v(1032.82, 559.67) * mm});
            skLineSegment(sketch, "E1799", {"start": v(1032.82, 559.67) * mm, "end": v(1032.6, 584.84) * mm});
            skLineSegment(sketch, "E1800", {"start": v(1032.6, 584.84) * mm, "end": v(1032.3, 609.91) * mm});
            skLineSegment(sketch, "E1801", {"start": v(1032.3, 609.91) * mm, "end": v(1031.9, 634.88) * mm});
            skLineSegment(sketch, "E1802", {"start": v(1031.9, 634.88) * mm, "end": v(1031.4, 659.73) * mm});
            skLineSegment(sketch, "E1803", {"start": v(1031.4, 659.73) * mm, "end": v(1030.74, 684.47) * mm});
            skLineSegment(sketch, "E1804", {"start": v(1030.74, 684.47) * mm, "end": v(1029.95, 709.1) * mm});
            skLineSegment(sketch, "E1805", {"start": v(1029.95, 709.1) * mm, "end": v(1028.99, 733.62) * mm});
            skLineSegment(sketch, "E1806", {"start": v(1028.99, 733.62) * mm, "end": v(1027.86, 758) * mm});
            skLineSegment(sketch, "E1807", {"start": v(1027.86, 758) * mm, "end": v(1026.53, 782.27) * mm});
            skLineSegment(sketch, "E1808", {"start": v(1026.53, 782.27) * mm, "end": v(1025, 806.42) * mm});
            skLineSegment(sketch, "E1809", {"start": v(1025, 806.42) * mm, "end": v(1023.25, 830.43) * mm});
            skLineSegment(sketch, "E1810", {"start": v(1023.25, 830.43) * mm, "end": v(1021.26, 854.3) * mm});
            skLineSegment(sketch, "E1811", {"start": v(1021.26, 854.3) * mm, "end": v(1019.02, 878.06) * mm});
            skLineSegment(sketch, "E1812", {"start": v(1019.02, 878.06) * mm, "end": v(1016.51, 901.66) * mm});
            skLineSegment(sketch, "E1813", {"start": v(1016.51, 901.66) * mm, "end": v(1013.73, 925.13) * mm});
            skLineSegment(sketch, "E1814", {"start": v(1013.73, 925.13) * mm, "end": v(1010.65, 948.46) * mm});
            skLineSegment(sketch, "E1815", {"start": v(1010.65, 948.46) * mm, "end": v(1007.25, 971.63) * mm});
            skLineSegment(sketch, "E1816", {"start": v(1007.25, 971.63) * mm, "end": v(1003.54, 994.66) * mm});
            skLineSegment(sketch, "E1817", {"start": v(1003.54, 994.66) * mm, "end": v(999.48, 1017.54) * mm});
            skLineSegment(sketch, "E1818", {"start": v(999.48, 1017.54) * mm, "end": v(995.07, 1040.26) * mm});
            skLineSegment(sketch, "E1819", {"start": v(995.07, 1040.26) * mm, "end": v(990.3, 1062.82) * mm});
            skLineSegment(sketch, "E1820", {"start": v(990.3, 1062.82) * mm, "end": v(985.12, 1085.23) * mm});
            skLineSegment(sketch, "E1821", {"start": v(985.12, 1085.23) * mm, "end": v(979.56, 1107.46) * mm});
            skLineSegment(sketch, "E1822", {"start": v(979.56, 1107.46) * mm, "end": v(973.58, 1129.53) * mm});
            skLineSegment(sketch, "E1823", {"start": v(973.58, 1129.53) * mm, "end": v(967.17, 1151.44) * mm});
            skLineSegment(sketch, "E1824", {"start": v(967.17, 1151.44) * mm, "end": v(960.32, 1173.17) * mm});
            skLineSegment(sketch, "E1825", {"start": v(960.32, 1173.17) * mm, "end": v(953, 1194.72) * mm});
            skLineSegment(sketch, "E1826", {"start": v(953, 1194.72) * mm, "end": v(945.22, 1216.1) * mm});
            skLineSegment(sketch, "E1827", {"start": v(945.22, 1216.1) * mm, "end": v(936.95, 1237.29) * mm});
            skLineSegment(sketch, "E1828", {"start": v(936.95, 1237.29) * mm, "end": v(928.17, 1258.3) * mm});
            skLineSegment(sketch, "E1829", {"start": v(928.17, 1258.3) * mm, "end": v(918.88, 1279.12) * mm});
            skLineSegment(sketch, "E1830", {"start": v(918.88, 1279.12) * mm, "end": v(909.05, 1299.75) * mm});
            skLineSegment(sketch, "E1831", {"start": v(909.05, 1299.75) * mm, "end": v(898.67, 1320.2) * mm});
            skLineSegment(sketch, "E1832", {"start": v(898.67, 1320.2) * mm, "end": v(887.74, 1340.43) * mm});
            skLineSegment(sketch, "E1833", {"start": v(887.74, 1340.43) * mm, "end": v(876.22, 1360.48) * mm});
            skLineSegment(sketch, "E1834", {"start": v(876.22, 1360.48) * mm, "end": v(864.11, 1380.32) * mm});
            skLineSegment(sketch, "E1835", {"start": v(864.11, 1380.32) * mm, "end": v(851.4, 1399.96) * mm});
            skLineSegment(sketch, "E1836", {"start": v(851.4, 1399.96) * mm, "end": v(838.06, 1419.4) * mm});
            skLineSegment(sketch, "E1837", {"start": v(838.06, 1419.4) * mm, "end": v(824.08, 1438.62) * mm});
            skLineSegment(sketch, "E1838", {"start": v(824.08, 1438.62) * mm, "end": v(809.45, 1457.62) * mm});
            skLineSegment(sketch, "E1839", {"start": v(809.45, 1457.62) * mm, "end": v(794.16, 1476.42) * mm});
            skLineSegment(sketch, "E1840", {"start": v(794.16, 1476.42) * mm, "end": v(778.19, 1494.99) * mm});
            skLineSegment(sketch, "E1841", {"start": v(778.19, 1494.99) * mm, "end": v(761.51, 1513.34) * mm});
            skLineSegment(sketch, "E1842", {"start": v(761.51, 1513.34) * mm, "end": v(744.13, 1531.47) * mm});
            skLineSegment(sketch, "E1843", {"start": v(744.13, 1531.47) * mm, "end": v(726.02, 1549.36) * mm});
            skLineSegment(sketch, "E1844", {"start": v(726.02, 1549.36) * mm, "end": v(707.17, 1567.03) * mm});
            skLineSegment(sketch, "E1845", {"start": v(707.17, 1567.03) * mm, "end": v(687.56, 1584.46) * mm});
            skLineSegment(sketch, "E1846", {"start": v(687.56, 1584.46) * mm, "end": v(667.19, 1601.66) * mm});
            skLineSegment(sketch, "E1847", {"start": v(667.19, 1601.66) * mm, "end": v(646.02, 1618.62) * mm});
            skLineSegment(sketch, "E1848", {"start": v(646.02, 1618.62) * mm, "end": v(624.06, 1635.34) * mm});
            skLineSegment(sketch, "E1849", {"start": v(624.06, 1635.34) * mm, "end": v(601.28, 1651.81) * mm});
            skLineSegment(sketch, "E1850", {"start": v(601.28, 1651.81) * mm, "end": v(601.28, 1702.61) * mm});
            skLineSegment(sketch, "E1851", {"start": v(601.28, 1702.61) * mm, "end": v(623.75, 1714.29) * mm});
            skLineSegment(sketch, "E1852", {"start": v(623.75, 1714.29) * mm, "end": v(646.34, 1725.74) * mm});
            skLineSegment(sketch, "E1853", {"start": v(646.34, 1725.74) * mm, "end": v(669.02, 1736.97) * mm});
            skLineSegment(sketch, "E1854", {"start": v(669.02, 1736.97) * mm, "end": v(691.82, 1747.96) * mm});
            skLineSegment(sketch, "E1855", {"start": v(691.82, 1747.96) * mm, "end": v(714.72, 1758.7) * mm});
            skLineSegment(sketch, "E1856", {"start": v(714.72, 1758.7) * mm, "end": v(737.72, 1769.2) * mm});
            skLineSegment(sketch, "E1857", {"start": v(737.72, 1769.2) * mm, "end": v(760.82, 1779.46) * mm});
            skLineSegment(sketch, "E1858", {"start": v(760.82, 1779.46) * mm, "end": v(784.02, 1789.47) * mm});
            skLineSegment(sketch, "E1859", {"start": v(784.02, 1789.47) * mm, "end": v(807.31, 1799.21) * mm});
            skLineSegment(sketch, "E1860", {"start": v(807.31, 1799.21) * mm, "end": v(830.7, 1808.7) * mm});
            skLineSegment(sketch, "E1861", {"start": v(830.7, 1808.7) * mm, "end": v(854.18, 1817.9) * mm});
            skLineSegment(sketch, "E1862", {"start": v(854.18, 1817.9) * mm, "end": v(877.75, 1826.85) * mm});
            skLineSegment(sketch, "E1863", {"start": v(877.75, 1826.85) * mm, "end": v(901.4, 1835.52) * mm});
            skLineSegment(sketch, "E1864", {"start": v(901.4, 1835.52) * mm, "end": v(925.15, 1843.91) * mm});
            skLineSegment(sketch, "E1865", {"start": v(925.15, 1843.91) * mm, "end": v(948.97, 1852.02) * mm});
            skLineSegment(sketch, "E1866", {"start": v(948.97, 1852.02) * mm, "end": v(972.88, 1859.83) * mm});
            skLineSegment(sketch, "E1867", {"start": v(972.88, 1859.83) * mm, "end": v(996.87, 1867.35) * mm});
            skLineSegment(sketch, "E1868", {"start": v(996.87, 1867.35) * mm, "end": v(1020.94, 1874.58) * mm});
            skLineSegment(sketch, "E1869", {"start": v(1020.94, 1874.58) * mm, "end": v(1045.08, 1881.5) * mm});
            skLineSegment(sketch, "E1870", {"start": v(1045.08, 1881.5) * mm, "end": v(1069.3, 1888.11) * mm});
            skLineSegment(sketch, "E1871", {"start": v(1069.3, 1888.11) * mm, "end": v(1093.59, 1894.42) * mm});
            skLineSegment(sketch, "E1872", {"start": v(1093.59, 1894.42) * mm, "end": v(1117.95, 1900.4) * mm});
            skLineSegment(sketch, "E1873", {"start": v(1117.95, 1900.4) * mm, "end": v(1142.38, 1906.07) * mm});
            skLineSegment(sketch, "E1874", {"start": v(1142.38, 1906.07) * mm, "end": v(1166.87, 1911.41) * mm});
            skLineSegment(sketch, "E1875", {"start": v(1166.87, 1911.41) * mm, "end": v(1191.43, 1916.42) * mm});
            skLineSegment(sketch, "E1876", {"start": v(1191.43, 1916.42) * mm, "end": v(1216.05, 1921.1) * mm});
            skLineSegment(sketch, "E1877", {"start": v(1216.05, 1921.1) * mm, "end": v(1240.73, 1925.44) * mm});
            skLineSegment(sketch, "E1878", {"start": v(1240.73, 1925.44) * mm, "end": v(1265.46, 1929.44) * mm});
            skLineSegment(sketch, "E1879", {"start": v(1265.46, 1929.44) * mm, "end": v(1290.26, 1933.1) * mm});
            skLineSegment(sketch, "E1880", {"start": v(1290.26, 1933.1) * mm, "end": v(1315.1, 1936.4) * mm});
            skLineSegment(sketch, "E1881", {"start": v(1315.1, 1936.4) * mm, "end": v(1340.01, 1939.34) * mm});
            skLineSegment(sketch, "E1882", {"start": v(1340.01, 1939.34) * mm, "end": v(1364.96, 1941.92) * mm});
            skLineSegment(sketch, "E1883", {"start": v(1364.96, 1941.92) * mm, "end": v(1389.96, 1944.14) * mm});
            skLineSegment(sketch, "E1884", {"start": v(1389.96, 1944.14) * mm, "end": v(1415.01, 1945.99) * mm});
            skLineSegment(sketch, "E1885", {"start": v(1415.01, 1945.99) * mm, "end": v(1440.1, 1947.46) * mm});
            skLineSegment(sketch, "E1886", {"start": v(1440.1, 1947.46) * mm, "end": v(1465.24, 1948.56) * mm});
            skLineSegment(sketch, "E1887", {"start": v(1465.24, 1948.56) * mm, "end": v(1490.41, 1949.27) * mm});
            skLineSegment(sketch, "E1888", {"start": v(1490.41, 1949.27) * mm, "end": v(1515.63, 1949.6) * mm});
            skLineSegment(sketch, "E1889", {"start": v(1515.63, 1949.6) * mm, "end": v(1540.88, 1949.53) * mm});
            skLineSegment(sketch, "E1890", {"start": v(1540.88, 1949.53) * mm, "end": v(1566.16, 1949.07) * mm});
            skLineSegment(sketch, "E1891", {"start": v(1566.16, 1949.07) * mm, "end": v(1591.48, 1948.2) * mm});
            skLineSegment(sketch, "E1892", {"start": v(1591.48, 1948.2) * mm, "end": v(1616.82, 1946.94) * mm});
            skLineSegment(sketch, "E1893", {"start": v(1616.82, 1946.94) * mm, "end": v(1642.2, 1945.26) * mm});
            skLineSegment(sketch, "E1894", {"start": v(1642.2, 1945.26) * mm, "end": v(1667.6, 1943.17) * mm});
            skLineSegment(sketch, "E1895", {"start": v(1667.6, 1943.17) * mm, "end": v(1693.03, 1940.66) * mm});
            skLineSegment(sketch, "E1896", {"start": v(1693.03, 1940.66) * mm, "end": v(1718.49, 1937.72) * mm});
            skLineSegment(sketch, "E1897", {"start": v(1718.49, 1937.72) * mm, "end": v(1743.96, 1934.36) * mm});
            skLineSegment(sketch, "E1898", {"start": v(1743.96, 1934.36) * mm, "end": v(1769.45, 1930.57) * mm});
            skLineSegment(sketch, "E1899", {"start": v(1769.45, 1930.57) * mm, "end": v(1794.96, 1926.34) * mm});
            skLineSegment(sketch, "E1900", {"start": v(1794.96, 1926.34) * mm, "end": v(1820.48, 1921.66) * mm});
            skLineSegment(sketch, "E1901", {"start": v(1820.48, 1921.66) * mm, "end": v(1844.72, 1916.82) * mm});
            skLineSegment(sketch, "E1902", {"start": v(1844.72, 1916.82) * mm, "end": v(1868.76, 1911.6) * mm});
            skLineSegment(sketch, "E1903", {"start": v(1868.76, 1911.6) * mm, "end": v(1892.61, 1906.04) * mm});
            skLineSegment(sketch, "E1904", {"start": v(1892.61, 1906.04) * mm, "end": v(1916.26, 1900.11) * mm});
            skLineSegment(sketch, "E1905", {"start": v(1916.26, 1900.11) * mm, "end": v(1939.72, 1893.84) * mm});
            skLineSegment(sketch, "E1906", {"start": v(1939.72, 1893.84) * mm, "end": v(1962.97, 1887.21) * mm});
            skLineSegment(sketch, "E1907", {"start": v(1962.97, 1887.21) * mm, "end": v(1986.02, 1880.25) * mm});
            skLineSegment(sketch, "E1908", {"start": v(1986.02, 1880.25) * mm, "end": v(2008.87, 1872.94) * mm});
            skLineSegment(sketch, "E1909", {"start": v(2008.87, 1872.94) * mm, "end": v(2031.5, 1865.29) * mm});
            skLineSegment(sketch, "E1910", {"start": v(2031.5, 1865.29) * mm, "end": v(2053.94, 1857.3) * mm});
            skLineSegment(sketch, "E1911", {"start": v(2053.94, 1857.3) * mm, "end": v(2076.17, 1849) * mm});
            skLineSegment(sketch, "E1912", {"start": v(2076.17, 1849) * mm, "end": v(2098.19, 1840.36) * mm});
            skLineSegment(sketch, "E1913", {"start": v(2098.19, 1840.36) * mm, "end": v(2120, 1831.4) * mm});
            skLineSegment(sketch, "E1914", {"start": v(2120, 1831.4) * mm, "end": v(2141.6, 1822.11) * mm});
            skLineSegment(sketch, "E1915", {"start": v(2141.6, 1822.11) * mm, "end": v(2162.98, 1812.52) * mm});
            skLineSegment(sketch, "E1916", {"start": v(2162.98, 1812.52) * mm, "end": v(2184.14, 1802.6) * mm});
            skLineSegment(sketch, "E1917", {"start": v(2184.14, 1802.6) * mm, "end": v(2205.1, 1792.39) * mm});
            skLineSegment(sketch, "E1918", {"start": v(2205.1, 1792.39) * mm, "end": v(2225.83, 1781.86) * mm});
            skLineSegment(sketch, "E1919", {"start": v(2225.83, 1781.86) * mm, "end": v(2246.35, 1771.04) * mm});
            skLineSegment(sketch, "E1920", {"start": v(2246.35, 1771.04) * mm, "end": v(2266.64, 1759.91) * mm});
            skLineSegment(sketch, "E1921", {"start": v(2266.64, 1759.91) * mm, "end": v(2286.71, 1748.49) * mm});
            skLineSegment(sketch, "E1922", {"start": v(2286.71, 1748.49) * mm, "end": v(2306.56, 1736.78) * mm});
            skLineSegment(sketch, "E1923", {"start": v(2306.56, 1736.78) * mm, "end": v(2326.19, 1724.78) * mm});
            skLineSegment(sketch, "E1924", {"start": v(2326.19, 1724.78) * mm, "end": v(2345.59, 1712.5) * mm});
            skLineSegment(sketch, "E1925", {"start": v(2345.59, 1712.5) * mm, "end": v(2364.76, 1699.93) * mm});
            skLineSegment(sketch, "E1926", {"start": v(2364.76, 1699.93) * mm, "end": v(2383.7, 1687.09) * mm});
            skLineSegment(sketch, "E1927", {"start": v(2383.7, 1687.09) * mm, "end": v(2402.41, 1673.97) * mm});
            skLineSegment(sketch, "E1928", {"start": v(2402.41, 1673.97) * mm, "end": v(2420.9, 1660.59) * mm});
            skLineSegment(sketch, "E1929", {"start": v(2420.9, 1660.59) * mm, "end": v(2439.14, 1646.94) * mm});
            skLineSegment(sketch, "E1930", {"start": v(2439.14, 1646.94) * mm, "end": v(2457.15, 1633.02) * mm});
            skLineSegment(sketch, "E1931", {"start": v(2457.15, 1633.02) * mm, "end": v(2474.93, 1618.85) * mm});
            skLineSegment(sketch, "E1932", {"start": v(2474.93, 1618.85) * mm, "end": v(2492.47, 1604.42) * mm});
            skLineSegment(sketch, "E1933", {"start": v(2492.47, 1604.42) * mm, "end": v(2509.77, 1589.74) * mm});
            skLineSegment(sketch, "E1934", {"start": v(2509.77, 1589.74) * mm, "end": v(2526.83, 1574.81) * mm});
            skLineSegment(sketch, "E1935", {"start": v(2526.83, 1574.81) * mm, "end": v(2543.64, 1559.64) * mm});
            skLineSegment(sketch, "E1936", {"start": v(2543.64, 1559.64) * mm, "end": v(2560.22, 1544.22) * mm});
            skLineSegment(sketch, "E1937", {"start": v(2560.22, 1544.22) * mm, "end": v(2576.55, 1528.56) * mm});
            skLineSegment(sketch, "E1938", {"start": v(2576.55, 1528.56) * mm, "end": v(2592.63, 1512.67) * mm});
            skLineSegment(sketch, "E1939", {"start": v(2592.63, 1512.67) * mm, "end": v(2608.47, 1496.56) * mm});
            skLineSegment(sketch, "E1940", {"start": v(2608.47, 1496.56) * mm, "end": v(2624.06, 1480.2) * mm});
            skLineSegment(sketch, "E1941", {"start": v(2624.06, 1480.2) * mm, "end": v(2639.4, 1463.64) * mm});
            skLineSegment(sketch, "E1942", {"start": v(2639.4, 1463.64) * mm, "end": v(2654.48, 1446.85) * mm});
            skLineSegment(sketch, "E1943", {"start": v(2654.48, 1446.85) * mm, "end": v(2669.31, 1429.84) * mm});
            skLineSegment(sketch, "E1944", {"start": v(2669.31, 1429.84) * mm, "end": v(2683.89, 1412.62) * mm});
            skLineSegment(sketch, "E1945", {"start": v(2683.89, 1412.62) * mm, "end": v(2698.21, 1395.19) * mm});
            skLineSegment(sketch, "E1946", {"start": v(2698.21, 1395.19) * mm, "end": v(2712.28, 1377.55) * mm});
            skLineSegment(sketch, "E1947", {"start": v(2712.28, 1377.55) * mm, "end": v(2726.08, 1359.71) * mm});
            skLineSegment(sketch, "E1948", {"start": v(2726.08, 1359.71) * mm, "end": v(2739.63, 1341.68) * mm});
            skLineSegment(sketch, "E1949", {"start": v(2739.63, 1341.68) * mm, "end": v(2752.91, 1323.44) * mm});
            skLineSegment(sketch, "E1950", {"start": v(2752.91, 1323.44) * mm, "end": v(2765.93, 1305.02) * mm});
            skLineSegment(sketch, "E1951", {"start": v(2765.93, 1305.02) * mm, "end": v(2778.69, 1286.4) * mm});
            skLineSegment(sketch, "E1952", {"start": v(2778.69, 1286.4) * mm, "end": v(2791.18, 1267.6) * mm});
            skLineSegment(sketch, "E1953", {"start": v(2791.18, 1267.6) * mm, "end": v(2803.4, 1248.63) * mm});
            skLineSegment(sketch, "E1954", {"start": v(2803.4, 1248.63) * mm, "end": v(2815.36, 1229.48) * mm});
            skLineSegment(sketch, "E1955", {"start": v(2815.36, 1229.48) * mm, "end": v(2827.04, 1210.15) * mm});
            skLineSegment(sketch, "E1956", {"start": v(2827.04, 1210.15) * mm, "end": v(2838.45, 1190.65) * mm});
            skLineSegment(sketch, "E1957", {"start": v(2838.45, 1190.65) * mm, "end": v(2849.6, 1170.98) * mm});
            skLineSegment(sketch, "E1958", {"start": v(2849.6, 1170.98) * mm, "end": v(2860.46, 1151.15) * mm});
            skLineSegment(sketch, "E1959", {"start": v(2860.46, 1151.15) * mm, "end": v(2871.05, 1131.16) * mm});
            skLineSegment(sketch, "E1960", {"start": v(2871.05, 1131.16) * mm, "end": v(2881.36, 1111.01) * mm});
            skLineSegment(sketch, "E1961", {"start": v(2881.36, 1111.01) * mm, "end": v(2891.39, 1090.72) * mm});
            skLineSegment(sketch, "E1962", {"start": v(2891.39, 1090.72) * mm, "end": v(2901.14, 1070.27) * mm});
            skLineSegment(sketch, "E1963", {"start": v(2901.14, 1070.27) * mm, "end": v(2910.61, 1049.68) * mm});
            skLineSegment(sketch, "E1964", {"start": v(2910.61, 1049.68) * mm, "end": v(2919.8, 1028.94) * mm});
            skLineSegment(sketch, "E1965", {"start": v(2919.8, 1028.94) * mm, "end": v(2928.7, 1008.07) * mm});
            skLineSegment(sketch, "E1966", {"start": v(2928.7, 1008.07) * mm, "end": v(2937.32, 987.06) * mm});
            skLineSegment(sketch, "E1967", {"start": v(2937.32, 987.06) * mm, "end": v(2945.65, 965.92) * mm});
            skLineSegment(sketch, "E1968", {"start": v(2945.65, 965.92) * mm, "end": v(2953.7, 944.65) * mm});
            skLineSegment(sketch, "E1969", {"start": v(2953.7, 944.65) * mm, "end": v(2961.45, 923.26) * mm});
            skLineSegment(sketch, "E1970", {"start": v(2961.45, 923.26) * mm, "end": v(2968.9, 901.75) * mm});
            skLineSegment(sketch, "E1971", {"start": v(2968.9, 901.75) * mm, "end": v(2976.07, 880.12) * mm});
            skLineSegment(sketch, "E1972", {"start": v(2976.07, 880.12) * mm, "end": v(2982.95, 858.38) * mm});
            skLineSegment(sketch, "E1973", {"start": v(2982.95, 858.38) * mm, "end": v(2989.53, 836.53) * mm});
            skLineSegment(sketch, "E1974", {"start": v(2989.53, 836.53) * mm, "end": v(2995.8, 814.57) * mm});
            skLineSegment(sketch, "E1975", {"start": v(2995.8, 814.57) * mm, "end": v(3001.79, 792.5) * mm});
            skLineSegment(sketch, "E1976", {"start": v(3001.79, 792.5) * mm, "end": v(3007.47, 770.34) * mm});
            skLineSegment(sketch, "E1977", {"start": v(3007.47, 770.34) * mm, "end": v(3012.85, 748.09) * mm});
            skLineSegment(sketch, "E1978", {"start": v(3012.85, 748.09) * mm, "end": v(3017.93, 725.74) * mm});
            skLineSegment(sketch, "E1979", {"start": v(3017.93, 725.74) * mm, "end": v(3022.7, 703.3) * mm});
            skLineSegment(sketch, "E1980", {"start": v(3022.7, 703.3) * mm, "end": v(3027.16, 680.78) * mm});
            skLineSegment(sketch, "E1981", {"start": v(3027.16, 680.78) * mm, "end": v(3031.32, 658.17) * mm});
            skLineSegment(sketch, "E1982", {"start": v(3031.32, 658.17) * mm, "end": v(3035.18, 635.5) * mm});
            skLineSegment(sketch, "E1983", {"start": v(3035.18, 635.5) * mm, "end": v(3038.72, 612.74) * mm});
            skLineSegment(sketch, "E1984", {"start": v(3038.72, 612.74) * mm, "end": v(3041.95, 589.91) * mm});
            skLineSegment(sketch, "E1985", {"start": v(3041.95, 589.91) * mm, "end": v(3044.86, 567.02) * mm});
            skLineSegment(sketch, "E1986", {"start": v(3044.86, 567.02) * mm, "end": v(3047.47, 544.06) * mm});
            skLineSegment(sketch, "E1987", {"start": v(3047.47, 544.06) * mm, "end": v(3049.75, 521.04) * mm});
            skLineSegment(sketch, "E1988", {"start": v(3049.75, 521.04) * mm, "end": v(3051.72, 497.97) * mm});
            skLineSegment(sketch, "E1989", {"start": v(3051.72, 497.97) * mm, "end": v(3053.37, 474.84) * mm});
            skLineSegment(sketch, "E1990", {"start": v(3053.37, 474.84) * mm, "end": v(3054.7, 451.66) * mm});
            skLineSegment(sketch, "E1991", {"start": v(3054.7, 451.66) * mm, "end": v(3055.72, 428.44) * mm});
            skLineSegment(sketch, "E1992", {"start": v(3055.72, 428.44) * mm, "end": v(3056.4, 405.18) * mm});
            skLineSegment(sketch, "E1993", {"start": v(3056.4, 405.18) * mm, "end": v(3056.77, 381.87) * mm});
            skLineSegment(sketch, "E1994", {"start": v(3056.77, 381.87) * mm, "end": v(3056.8, 358.53) * mm});
            skLineSegment(sketch, "E1995", {"start": v(3056.8, 358.53) * mm, "end": v(3056.51, 335.16) * mm});
            skLineSegment(sketch, "E1996", {"start": v(3056.51, 335.16) * mm, "end": v(3055.9, 311.76) * mm});
            skLineSegment(sketch, "E1997", {"start": v(3055.9, 311.76) * mm, "end": v(3054.95, 288.34) * mm});
            skLineSegment(sketch, "E1998", {"start": v(3054.95, 288.34) * mm, "end": v(3053.67, 264.9) * mm});
            skLineSegment(sketch, "E1999", {"start": v(3053.67, 264.9) * mm, "end": v(3052.05, 241.43) * mm});
            skLineSegment(sketch, "E2000", {"start": v(3052.05, 241.43) * mm, "end": v(3050.1, 217.96) * mm});
            skLineSegment(sketch, "E2001", {"start": v(3050.1, 217.96) * mm, "end": v(3047.82, 194.47) * mm});
            skLineSegment(sketch, "E2002", {"start": v(3047.82, 194.47) * mm, "end": v(3045.2, 170.98) * mm});
            skLineSegment(sketch, "E2003", {"start": v(3045.2, 170.98) * mm, "end": v(3042.25, 147.48) * mm});
            skLineSegment(sketch, "E2004", {"start": v(3042.25, 147.48) * mm, "end": v(3038.95, 123.99) * mm});
            skLineSegment(sketch, "E2005", {"start": v(3038.95, 123.99) * mm, "end": v(3035.31, 100.5) * mm});
            skLineSegment(sketch, "E2006", {"start": v(3035.31, 100.5) * mm, "end": v(3031.33, 77.01) * mm});
            skLineSegment(sketch, "E2007", {"start": v(3031.33, 77.01) * mm, "end": v(3026.72, 52.78) * mm});
            skLineSegment(sketch, "E2008", {"start": v(3026.72, 52.78) * mm, "end": v(3021.5, 28.72) * mm});
            skLineSegment(sketch, "E2009", {"start": v(3021.5, 28.72) * mm, "end": v(3015.69, 4.8) * mm});
            skLineSegment(sketch, "E2010", {"start": v(3015.69, 4.8) * mm, "end": v(3009.3, -18.94) * mm});
            skLineSegment(sketch, "E2011", {"start": v(3009.3, -18.94) * mm, "end": v(3002.35, -42.53) * mm});
            skLineSegment(sketch, "E2012", {"start": v(3002.35, -42.53) * mm, "end": v(2994.85, -65.97) * mm});
            skLineSegment(sketch, "E2013", {"start": v(2994.85, -65.97) * mm, "end": v(2986.83, -89.25) * mm});
            skLineSegment(sketch, "E2014", {"start": v(2986.83, -89.25) * mm, "end": v(2978.28, -112.38) * mm});
            skLineSegment(sketch, "E2015", {"start": v(2978.28, -112.38) * mm, "end": v(2969.25, -135.36) * mm});
            skLineSegment(sketch, "E2016", {"start": v(2969.25, -135.36) * mm, "end": v(2959.72, -158.18) * mm});
            skLineSegment(sketch, "E2017", {"start": v(2959.72, -158.18) * mm, "end": v(2949.74, -180.85) * mm});
            skLineSegment(sketch, "E2018", {"start": v(2949.74, -180.85) * mm, "end": v(2939.3, -203.37) * mm});
            skLineSegment(sketch, "E2019", {"start": v(2939.3, -203.37) * mm, "end": v(2928.43, -225.74) * mm});
            skLineSegment(sketch, "E2020", {"start": v(2928.43, -225.74) * mm, "end": v(2917.13, -247.96) * mm});
            skLineSegment(sketch, "E2021", {"start": v(2917.13, -247.96) * mm, "end": v(2905.44, -270.04) * mm});
            skLineSegment(sketch, "E2022", {"start": v(2905.44, -270.04) * mm, "end": v(2893.36, -291.97) * mm});
            skLineSegment(sketch, "E2023", {"start": v(2893.36, -291.97) * mm, "end": v(2880.9, -313.75) * mm});
            skLineSegment(sketch, "E2024", {"start": v(2880.9, -313.75) * mm, "end": v(2868.1, -335.38) * mm});
            skLineSegment(sketch, "E2025", {"start": v(2868.1, -335.38) * mm, "end": v(2854.95, -356.87) * mm});
            skLineSegment(sketch, "E2026", {"start": v(2854.95, -356.87) * mm, "end": v(2841.48, -378.22) * mm});
            skLineSegment(sketch, "E2027", {"start": v(2841.48, -378.22) * mm, "end": v(2827.7, -399.43) * mm});
            skLineSegment(sketch, "E2028", {"start": v(2827.7, -399.43) * mm, "end": v(2813.62, -420.5) * mm});
            skLineSegment(sketch, "E2029", {"start": v(2813.62, -420.5) * mm, "end": v(2799.27, -441.42) * mm});
            skLineSegment(sketch, "E2030", {"start": v(2799.27, -441.42) * mm, "end": v(2784.66, -462.2) * mm});
            skLineSegment(sketch, "E2031", {"start": v(2784.66, -462.2) * mm, "end": v(2769.8, -482.85) * mm});
            skLineSegment(sketch, "E2032", {"start": v(2769.8, -482.85) * mm, "end": v(2754.73, -503.35) * mm});
            skLineSegment(sketch, "E2033", {"start": v(2754.73, -503.35) * mm, "end": v(2739.43, -523.72) * mm});
            skLineSegment(sketch, "E2034", {"start": v(2739.43, -523.72) * mm, "end": v(2723.94, -543.96) * mm});
            skLineSegment(sketch, "E2035", {"start": v(2723.94, -543.96) * mm, "end": v(2708.27, -564.06) * mm});
            skLineSegment(sketch, "E2036", {"start": v(2708.27, -564.06) * mm, "end": v(2692.43, -584.02) * mm});
            skLineSegment(sketch, "E2037", {"start": v(2692.43, -584.02) * mm, "end": v(2676.44, -603.85) * mm});
            skLineSegment(sketch, "E2038", {"start": v(2676.44, -603.85) * mm, "end": v(2660.32, -623.55) * mm});
            skLineSegment(sketch, "E2039", {"start": v(2660.32, -623.55) * mm, "end": v(2644.08, -643.11) * mm});
            skLineSegment(sketch, "E2040", {"start": v(2644.08, -643.11) * mm, "end": v(2627.74, -662.55) * mm});
            skLineSegment(sketch, "E2041", {"start": v(2627.74, -662.55) * mm, "end": v(2611.31, -681.86) * mm});
            skLineSegment(sketch, "E2042", {"start": v(2611.31, -681.86) * mm, "end": v(2594.81, -701.03) * mm});
            skLineSegment(sketch, "E2043", {"start": v(2594.81, -701.03) * mm, "end": v(2578.26, -720.08) * mm});
            skLineSegment(sketch, "E2044", {"start": v(2578.26, -720.08) * mm, "end": v(2561.67, -739) * mm});
            skLineSegment(sketch, "E2045", {"start": v(2561.67, -739) * mm, "end": v(2545.06, -757.8) * mm});
            skLineSegment(sketch, "E2046", {"start": v(2545.06, -757.8) * mm, "end": v(2528.44, -776.47) * mm});
            skLineSegment(sketch, "E2047", {"start": v(2528.44, -776.47) * mm, "end": v(2511.83, -795) * mm});
            skLineSegment(sketch, "E2048", {"start": v(2511.83, -795) * mm, "end": v(2495.25, -813.43) * mm});
            skLineSegment(sketch, "E2049", {"start": v(2495.25, -813.43) * mm, "end": v(2478.7, -831.73) * mm});
            skLineSegment(sketch, "E2050", {"start": v(2478.7, -831.73) * mm, "end": v(2462.21, -849.9) * mm});
            skLineSegment(sketch, "E2051", {"start": v(2462.21, -849.9) * mm, "end": v(2445.8, -867.96) * mm});
            skLineSegment(sketch, "E2052", {"start": v(2445.8, -867.96) * mm, "end": v(2429.47, -885.9) * mm});
            skLineSegment(sketch, "E2053", {"start": v(2429.47, -885.9) * mm, "end": v(2413.25, -903.71) * mm});
            skLineSegment(sketch, "E2054", {"start": v(2413.25, -903.71) * mm, "end": v(2397.15, -921.41) * mm});
            skLineSegment(sketch, "E2055", {"start": v(2397.15, -921.41) * mm, "end": v(2381.18, -938.99) * mm});
            skLineSegment(sketch, "E2056", {"start": v(2381.18, -938.99) * mm, "end": v(2363.84, -958.09) * mm});
            skLineSegment(sketch, "E2057", {"start": v(2363.84, -958.09) * mm, "end": v(2346.49, -977.16) * mm});
            skLineSegment(sketch, "E2058", {"start": v(2346.49, -977.16) * mm, "end": v(2329.1, -996.22) * mm});
            skLineSegment(sketch, "E2059", {"start": v(2329.1, -996.22) * mm, "end": v(2311.71, -1015.26) * mm});
            skLineSegment(sketch, "E2060", {"start": v(2311.71, -1015.26) * mm, "end": v(2294.3, -1034.29) * mm});
            skLineSegment(sketch, "E2061", {"start": v(2294.3, -1034.29) * mm, "end": v(2276.87, -1053.3) * mm});
            skLineSegment(sketch, "E2062", {"start": v(2276.87, -1053.3) * mm, "end": v(2259.43, -1072.3) * mm});
            skLineSegment(sketch, "E2063", {"start": v(2259.43, -1072.3) * mm, "end": v(2241.97, -1091.28) * mm});
            skLineSegment(sketch, "E2064", {"start": v(2241.97, -1091.28) * mm, "end": v(2224.5, -1110.25) * mm});
            skLineSegment(sketch, "E2065", {"start": v(2224.5, -1110.25) * mm, "end": v(2207, -1129.2) * mm});
            skLineSegment(sketch, "E2066", {"start": v(2207, -1129.2) * mm, "end": v(2189.5, -1148.15) * mm});
            skLineSegment(sketch, "E2067", {"start": v(2189.5, -1148.15) * mm, "end": v(2172, -1167.08) * mm});
            skLineSegment(sketch, "E2068", {"start": v(2172, -1167.08) * mm, "end": v(2154.47, -1186) * mm});
            skLineSegment(sketch, "E2069", {"start": v(2154.47, -1186) * mm, "end": v(2136.93, -1204.92) * mm});
            skLineSegment(sketch, "E2070", {"start": v(2136.93, -1204.92) * mm, "end": v(2119.39, -1223.82) * mm});
            skLineSegment(sketch, "E2071", {"start": v(2119.39, -1223.82) * mm, "end": v(2101.83, -1242.71) * mm});
            skLineSegment(sketch, "E2072", {"start": v(2101.83, -1242.71) * mm, "end": v(2084.27, -1261.6) * mm});
            skLineSegment(sketch, "E2073", {"start": v(2084.27, -1261.6) * mm, "end": v(2066.7, -1280.48) * mm});
            skLineSegment(sketch, "E2074", {"start": v(2066.7, -1280.48) * mm, "end": v(2049.12, -1299.35) * mm});
            skLineSegment(sketch, "E2075", {"start": v(2049.12, -1299.35) * mm, "end": v(2031.54, -1318.22) * mm});
            skLineSegment(sketch, "E2076", {"start": v(2031.54, -1318.22) * mm, "end": v(2013.96, -1337.09) * mm});
            skLineSegment(sketch, "E2077", {"start": v(2013.96, -1337.09) * mm, "end": v(1996.36, -1355.95) * mm});
            skLineSegment(sketch, "E2078", {"start": v(1996.36, -1355.95) * mm, "end": v(1978.77, -1374.8) * mm});
            skLineSegment(sketch, "E2079", {"start": v(1978.77, -1374.8) * mm, "end": v(1961.17, -1393.65) * mm});
            skLineSegment(sketch, "E2080", {"start": v(1961.17, -1393.65) * mm, "end": v(1943.57, -1412.5) * mm});
            skLineSegment(sketch, "E2081", {"start": v(1943.57, -1412.5) * mm, "end": v(1925.97, -1431.35) * mm});
            skLineSegment(sketch, "E2082", {"start": v(1925.97, -1431.35) * mm, "end": v(1908.36, -1450.2) * mm});
            skLineSegment(sketch, "E2083", {"start": v(1908.36, -1450.2) * mm, "end": v(1890.76, -1469.05) * mm});
            skLineSegment(sketch, "E2084", {"start": v(1890.76, -1469.05) * mm, "end": v(1873.16, -1487.9) * mm});
            skLineSegment(sketch, "E2085", {"start": v(1873.16, -1487.9) * mm, "end": v(1855.56, -1506.75) * mm});
            skLineSegment(sketch, "E2086", {"start": v(1855.56, -1506.75) * mm, "end": v(1837.96, -1525.6) * mm});
            skLineSegment(sketch, "E2087", {"start": v(1837.96, -1525.6) * mm, "end": v(1820.37, -1544.45) * mm});
            skLineSegment(sketch, "E2088", {"start": v(1820.37, -1544.45) * mm, "end": v(1802.78, -1563.3) * mm});
            skLineSegment(sketch, "E2089", {"start": v(1802.78, -1563.3) * mm, "end": v(1785.2, -1582.17) * mm});
            skLineSegment(sketch, "E2090", {"start": v(1785.2, -1582.17) * mm, "end": v(1767.61, -1601.03) * mm});
            skLineSegment(sketch, "E2091", {"start": v(1767.61, -1601.03) * mm, "end": v(1750.04, -1619.9) * mm});
            skLineSegment(sketch, "E2092", {"start": v(1750.04, -1619.9) * mm, "end": v(1732.48, -1638.78) * mm});
            skLineSegment(sketch, "E2093", {"start": v(1732.48, -1638.78) * mm, "end": v(1714.92, -1657.66) * mm});
            skLineSegment(sketch, "E2094", {"start": v(1714.92, -1657.66) * mm, "end": v(1697.37, -1676.56) * mm});
            skLineSegment(sketch, "E2095", {"start": v(1697.37, -1676.56) * mm, "end": v(1679.83, -1695.46) * mm});
            skLineSegment(sketch, "E2096", {"start": v(1679.83, -1695.46) * mm, "end": v(1662.3, -1714.37) * mm});
            skLineSegment(sketch, "E2097", {"start": v(1662.3, -1714.37) * mm, "end": v(1644.78, -1733.28) * mm});
            skLineSegment(sketch, "E2098", {"start": v(1644.78, -1733.28) * mm, "end": v(1627.27, -1752.21) * mm});
            skLineSegment(sketch, "E2099", {"start": v(1627.27, -1752.21) * mm, "end": v(1609.78, -1771.15) * mm});
            skLineSegment(sketch, "E2100", {"start": v(1609.78, -1771.15) * mm, "end": v(1592.3, -1790.1) * mm});
            skLineSegment(sketch, "E2101", {"start": v(1592.3, -1790.1) * mm, "end": v(1574.83, -1809.06) * mm});
            skLineSegment(sketch, "E2102", {"start": v(1574.83, -1809.06) * mm, "end": v(1557.38, -1828.04) * mm});
            skLineSegment(sketch, "E2103", {"start": v(1557.38, -1828.04) * mm, "end": v(1539.94, -1847.03) * mm});
            skLineSegment(sketch, "E2104", {"start": v(1539.94, -1847.03) * mm, "end": v(1522.52, -1866.03) * mm});
            skLineSegment(sketch, "E2105", {"start": v(1522.52, -1866.03) * mm, "end": v(1505.12, -1885.05) * mm});
            skLineSegment(sketch, "E2106", {"start": v(1505.12, -1885.05) * mm, "end": v(1487.74, -1904.08) * mm});
            skLineSegment(sketch, "E2107", {"start": v(1487.74, -1904.08) * mm, "end": v(1470.37, -1923.13) * mm});
            skLineSegment(sketch, "E2108", {"start": v(1470.37, -1923.13) * mm, "end": v(1453.02, -1942.2) * mm});
            skLineSegment(sketch, "E2109", {"start": v(1453.02, -1942.2) * mm, "end": v(1435.7, -1961.29) * mm});
            skLineSegment(sketch, "E2110", {"start": v(1435.7, -1961.29) * mm, "end": v(1418.4, -1980.39) * mm});
            skLineSegment(sketch, "E2111", {"start": v(1418.4, -1980.39) * mm, "end": v(1401.9, -1998.7) * mm});
            skLineSegment(sketch, "E2112", {"start": v(1401.9, -1998.7) * mm, "end": v(1385.39, -2017.22) * mm});
            skLineSegment(sketch, "E2113", {"start": v(1385.39, -2017.22) * mm, "end": v(1368.83, -2035.94) * mm});
            skLineSegment(sketch, "E2114", {"start": v(1368.83, -2035.94) * mm, "end": v(1352.24, -2054.84) * mm});
            skLineSegment(sketch, "E2115", {"start": v(1352.24, -2054.84) * mm, "end": v(1335.6, -2073.91) * mm});
            skLineSegment(sketch, "E2116", {"start": v(1335.6, -2073.91) * mm, "end": v(1318.9, -2093.13) * mm});
            skLineSegment(sketch, "E2117", {"start": v(1318.9, -2093.13) * mm, "end": v(1302.16, -2112.47) * mm});
            skLineSegment(sketch, "E2118", {"start": v(1302.16, -2112.47) * mm, "end": v(1285.37, -2131.93) * mm});
            skLineSegment(sketch, "E2119", {"start": v(1285.37, -2131.93) * mm, "end": v(1268.52, -2151.49) * mm});
            skLineSegment(sketch, "E2120", {"start": v(1268.52, -2151.49) * mm, "end": v(1251.62, -2171.13) * mm});
            skLineSegment(sketch, "E2121", {"start": v(1251.62, -2171.13) * mm, "end": v(1234.65, -2190.84) * mm});
            skLineSegment(sketch, "E2122", {"start": v(1234.65, -2190.84) * mm, "end": v(1217.62, -2210.59) * mm});
            skLineSegment(sketch, "E2123", {"start": v(1217.62, -2210.59) * mm, "end": v(1200.52, -2230.38) * mm});
            skLineSegment(sketch, "E2124", {"start": v(1200.52, -2230.38) * mm, "end": v(1183.35, -2250.18) * mm});
            skLineSegment(sketch, "E2125", {"start": v(1183.35, -2250.18) * mm, "end": v(1166.1, -2269.99) * mm});
            skLineSegment(sketch, "E2126", {"start": v(1166.1, -2269.99) * mm, "end": v(1148.78, -2289.78) * mm});
            skLineSegment(sketch, "E2127", {"start": v(1148.78, -2289.78) * mm, "end": v(1131.38, -2309.53) * mm});
            skLineSegment(sketch, "E2128", {"start": v(1131.38, -2309.53) * mm, "end": v(1113.9, -2329.24) * mm});
            skLineSegment(sketch, "E2129", {"start": v(1113.9, -2329.24) * mm, "end": v(1096.34, -2348.88) * mm});
            skLineSegment(sketch, "E2130", {"start": v(1096.34, -2348.88) * mm, "end": v(1078.69, -2368.44) * mm});
            skLineSegment(sketch, "E2131", {"start": v(1078.69, -2368.44) * mm, "end": v(1060.95, -2387.9) * mm});
            skLineSegment(sketch, "E2132", {"start": v(1060.95, -2387.9) * mm, "end": v(1043.11, -2407.24) * mm});
            skLineSegment(sketch, "E2133", {"start": v(1043.11, -2407.24) * mm, "end": v(1025.18, -2426.45) * mm});
            skLineSegment(sketch, "E2134", {"start": v(1025.18, -2426.45) * mm, "end": v(1007.15, -2445.51) * mm});
            skLineSegment(sketch, "E2135", {"start": v(1007.15, -2445.51) * mm, "end": v(989.02, -2464.41) * mm});
            skLineSegment(sketch, "E2136", {"start": v(989.02, -2464.41) * mm, "end": v(970.79, -2483.13) * mm});
            skLineSegment(sketch, "E2137", {"start": v(970.79, -2483.13) * mm, "end": v(952.44, -2501.65) * mm});
            skLineSegment(sketch, "E2138", {"start": v(952.44, -2501.65) * mm, "end": v(933.99, -2519.96) * mm});
            skLineSegment(sketch, "E2139", {"start": v(933.99, -2519.96) * mm, "end": v(915.42, -2538.04) * mm});
            skLineSegment(sketch, "E2140", {"start": v(915.42, -2538.04) * mm, "end": v(896.74, -2555.87) * mm});
            skLineSegment(sketch, "E2141", {"start": v(896.74, -2555.87) * mm, "end": v(877.93, -2573.44) * mm});
            skLineSegment(sketch, "E2142", {"start": v(877.93, -2573.44) * mm, "end": v(859, -2590.73) * mm});
            skLineSegment(sketch, "E2143", {"start": v(859, -2590.73) * mm, "end": v(839.96, -2607.72) * mm});
            skLineSegment(sketch, "E2144", {"start": v(839.96, -2607.72) * mm, "end": v(820.78, -2624.4) * mm});
            skLineSegment(sketch, "E2145", {"start": v(820.78, -2624.4) * mm, "end": v(801.47, -2640.75) * mm});
            skLineSegment(sketch, "E2146", {"start": v(801.47, -2640.75) * mm, "end": v(782.04, -2656.75) * mm});
            skLineSegment(sketch, "E2147", {"start": v(782.04, -2656.75) * mm, "end": v(762.46, -2672.4) * mm});
            skLineSegment(sketch, "E2148", {"start": v(762.46, -2672.4) * mm, "end": v(742.74, -2687.66) * mm});
            skLineSegment(sketch, "E2149", {"start": v(742.74, -2687.66) * mm, "end": v(722.88, -2702.53) * mm});
            skLineSegment(sketch, "E2150", {"start": v(722.88, -2702.53) * mm, "end": v(702.88, -2716.99) * mm});
            skSolve(sketch);
        }
        {
            var Q0;
            Q0=makeQuery(id+"F0.imprint","IMPRINT",FACE,{"disambiguationData":[TD([[makeQuery(id+"F0.imprint","IMPRINT",EDGE,{"derivedFrom":sQuery(id+"F0.wireOp",EDGE,"E0")}),1.0]])]});
            var Q1;
            Q1=makeQuery(id+"F0.imprint","IMPRINT",FACE,{"disambiguationData":[TD([[makeQuery(id+"F0.imprint","IMPRINT",EDGE,{"derivedFrom":sQuery(id+"F0.wireOp",EDGE,"E1345")}),-1.0]])]});
            extrude(context, id + "F1", {"entities" : qUnion([Q0, Q1]), "oppositeDirection" : true, "depth" : 25.4 * mm, "offsetDistance" : 25.4 * mm});
        }
    });
